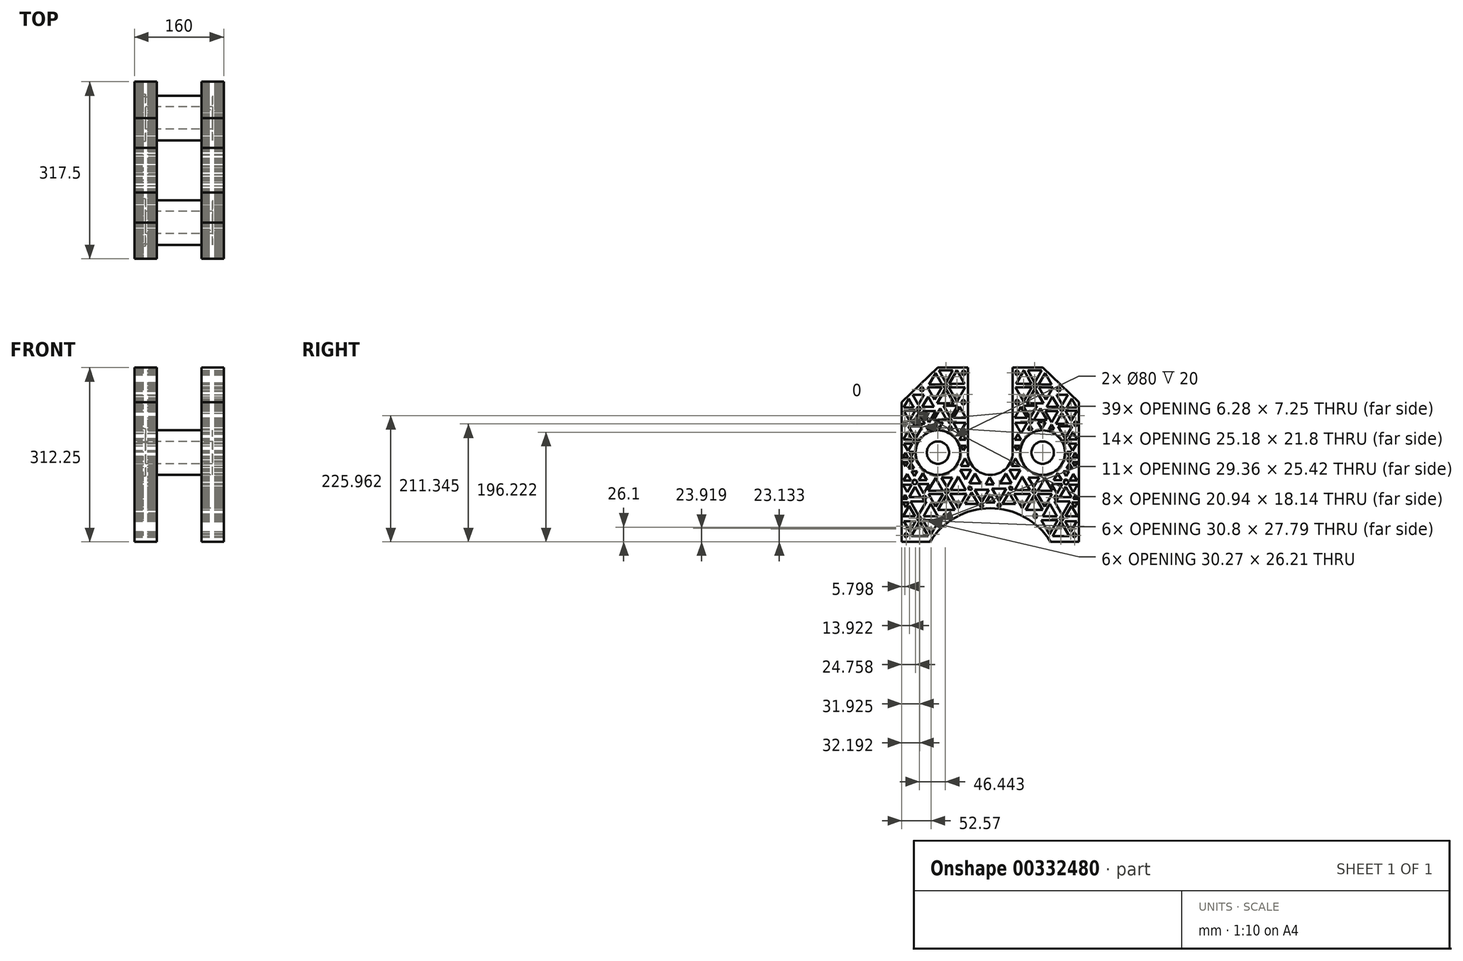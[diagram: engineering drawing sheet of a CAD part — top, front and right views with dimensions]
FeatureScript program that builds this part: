
annotation { "Feature Type Name" : "Feature", "Feature Type Description" : "" }
export const myFeature = defineFeature(function(context is Context, id is Id, definition is map)
    precondition{}
    {
        {
            var Q0;
            Q0=qCreatedBy(makeId("Right.planeOp"),FACE);
            var sketch = newSketch(context, id + "F0", { "sketchPlane" : qUnion([Q0])});
            skLineSegment(sketch, "E0", {"start": v(-158.75, 0) * mm, "end": v(-158.75, 250) * mm});
            skLineSegment(sketch, "E1", {"start": v(-158.75, 250) * mm, "end": v(-93.75, 312.25) * mm});
            skLineSegment(sketch, "E2.MirrorCS", {"start": v(158.75, 250) * mm, "end": v(93.75, 312.25) * mm});
            skLineSegment(sketch, "E3.MirrorCS", {"start": v(158.75, 0) * mm, "end": v(158.75, 250) * mm});
            skLineSegment(sketch, "E4", {"start": v(-158.75, 0) * mm, "end": v(-107.95, 0) * mm});
            skArc(sketch, "E5", {"start": v(107.95, 0) * mm, "mid": v(0, 60.1) * mm, "end": v(-107.95, 0) * mm});
            skLineSegment(sketch, "E6", {"start": v(107.95, 0) * mm, "end": v(158.75, 0) * mm});
            skLineSegment(sketch, "E7", {"start": v(-93.75, 312.25) * mm, "end": v(-40, 312.25) * mm});
            skLineSegment(sketch, "E8", {"start": v(-40, 312.25) * mm, "end": v(-40, 159.85) * mm});
            skArc(sketch, "E9", {"start": v(-40, 159.85) * mm, "mid": v(0, 119.85) * mm, "end": v(40, 159.85) * mm});
            skLineSegment(sketch, "E10", {"start": v(40, 159.85) * mm, "end": v(40, 312.25) * mm});
            skLineSegment(sketch, "E11", {"start": v(40, 312.25) * mm, "end": v(93.75, 312.25) * mm});
            skCircle(sketch, "E12", {"center": v(93.75, 159.85) * mm, "radius": 40 * mm});
            skCircle(sketch, "E13", {"center": v(-93.75, 159.85) * mm, "radius": 40 * mm});
            skSolve(sketch);
        }
        {
            var Q0;
            Q0=makeQuery(id+"F0.imprint","IMPRINT",FACE,{"disambiguationData":[TD([[makeQuery(id+"F0.imprint","IMPRINT",EDGE,{"derivedFrom":sQuery(id+"F0.wireOp",EDGE,"E0")}),-1.0]])]});
            extrude(context, id + "F1", {"entities" : qUnion([Q0]), "endBound" : BoundingType.SYMMETRIC, "depth" : 160 * mm});
        }
        {
            var Q0;
            Q0=makeQuery(id+"F1.opExtrude","SWEPT_FACE",FACE,{"disambiguationData":[OSD([sQuery(id+"F0.wireOp",EDGE,"E3.MirrorCS")])]});
            var sketch = newSketch(context, id + "F2", { "sketchPlane" : qUnion([Q0])});
            skLineSegment(sketch, "E14.bottom", {"start": v(-40, 0) * mm, "end": v(40, 0) * mm});
            skLineSegment(sketch, "E14.top", {"start": v(-40, 330.24) * mm, "end": v(40, 330.24) * mm});
            skLineSegment(sketch, "E14.left", {"start": v(-40, 0) * mm, "end": v(-40, 330.24) * mm});
            skLineSegment(sketch, "E14.right", {"start": v(40, 0) * mm, "end": v(40, 330.24) * mm});
            skSolve(sketch);
        }
        {
            var Q0;
            {var subQ0=sQuery(id+"F2.wireOp",EDGE,"E14.bottom");Q0=makeQuery(id+"F2.imprint","IMPRINT",FACE,{"disambiguationData":[TD([[makeQuery(id+"F2.imprint","IMPRINT",EDGE,{"derivedFrom":subQ0}),1.0]])]});}
            var Q1;
            {var subQ0=sQuery(id+"F2.wireOp",EDGE,"E14.top");Q1=makeQuery(id+"F2.imprint","IMPRINT",FACE,{"disambiguationData":[TD([[makeQuery(id+"F2.imprint","IMPRINT",EDGE,{"derivedFrom":subQ0}),-1.0]])]});}
            extrude(context, id + "F3", {"entities" : qUnion([Q0, Q1]), "operationType" : NewBodyOperationType.REMOVE, "oppositeDirection" : true, "depth" : 414.02 * mm});
        }
        {
            var Q0;
            Q0=makeQuery(id+"F1.opExtrude","CAP_FACE",FACE,{"disambiguationData":[OSD([sQuery(id+"F0.wireOp",EDGE,"E0"),sQuery(id+"F0.wireOp",EDGE,"E1"),sQuery(id+"F0.wireOp",EDGE,"E2.MirrorCS"),sQuery(id+"F0.wireOp",EDGE,"E3.MirrorCS"),sQuery(id+"F0.wireOp",EDGE,"E4"),sQuery(id+"F0.wireOp",EDGE,"E5"),sQuery(id+"F0.wireOp",EDGE,"E6"),sQuery(id+"F0.wireOp",EDGE,"E7"),sQuery(id+"F0.wireOp",EDGE,"E8"),sQuery(id+"F0.wireOp",EDGE,"E9"),sQuery(id+"F0.wireOp",EDGE,"E10"),sQuery(id+"F0.wireOp",EDGE,"E11"),sQuery(id+"F0.wireOp",EDGE,"E12"),sQuery(id+"F0.wireOp",EDGE,"E13")])],"isStart":true});
            var sketch = newSketch(context, id + "F4", { "sketchPlane" : qUnion([Q0])});
            skCircle(sketch, "E15", {"center": v(-93.75, 159.85) * mm, "radius": 42.5 * mm});
            skCircle(sketch, "E16", {"center": v(-93.75, 159.85) * mm, "radius": 20 * mm});
            skCircle(sketch, "E17", {"center": v(93.75, 159.85) * mm, "radius": 42.5 * mm});
            skCircle(sketch, "E18", {"center": v(93.75, 159.85) * mm, "radius": 20 * mm});
            skSolve(sketch);
        }
        {
            var Q0;
            Q0=makeQuery(id+"F4.imprint","IMPRINT",FACE,{"disambiguationData":[TD([[makeQuery(id+"F4.imprint","IMPRINT",EDGE,{"derivedFrom":sQuery(id+"F4.wireOp",EDGE,"E16")}),-1.0]])]});
            var Q1;
            Q1=makeQuery(id+"F4.imprint","IMPRINT",FACE,{"disambiguationData":[TD([[makeQuery(id+"F4.imprint","IMPRINT",EDGE,{"derivedFrom":sQuery(id+"F4.wireOp",EDGE,"E18")}),-1.0]])]});
            extrude(context, id + "F5", {"entities" : qUnion([Q0, Q1]), "operationType" : NewBodyOperationType.ADD, "oppositeDirection" : true, "depth" : 140 * mm});
        }
        {
            var Q0;
            {var subQ0=sQuery(id+"F0.wireOp",EDGE,"E13");var subQ1=sQuery(id+"F0.wireOp",EDGE,"E12");Q0=makeQuery(id+"F5.boolean.opBoolean","MERGE",FACE,{"derivedFrom":[makeQuery(id+"F1.opExtrude","CAP_FACE",FACE,{"disambiguationData":[OSD([sQuery(id+"F0.wireOp",EDGE,"E0"),sQuery(id+"F0.wireOp",EDGE,"E1"),sQuery(id+"F0.wireOp",EDGE,"E2.MirrorCS"),sQuery(id+"F0.wireOp",EDGE,"E3.MirrorCS"),sQuery(id+"F0.wireOp",EDGE,"E4"),sQuery(id+"F0.wireOp",EDGE,"E5"),sQuery(id+"F0.wireOp",EDGE,"E6"),sQuery(id+"F0.wireOp",EDGE,"E7"),sQuery(id+"F0.wireOp",EDGE,"E8"),sQuery(id+"F0.wireOp",EDGE,"E9"),sQuery(id+"F0.wireOp",EDGE,"E10"),sQuery(id+"F0.wireOp",EDGE,"E11"),subQ1,subQ0])],"isStart":true}),makeQuery(id+"F5.opExtrude","CAP_FACE",FACE,{"disambiguationData":[OSD([subQ1,sQuery(id+"F4.wireOp",EDGE,"E16")])],"isStart":true}),makeQuery(id+"F5.opExtrude","CAP_FACE",FACE,{"disambiguationData":[OSD([subQ0,sQuery(id+"F4.wireOp",EDGE,"E18")])],"isStart":true})]});}
            var sketch = newSketch(context, id + "F6", { "sketchPlane" : qUnion([Q0])});
            skCircle(sketch, "E19", {"center": v(-93.75, 159.85) * mm, "radius": 42.5 * mm});
            skCircle(sketch, "E20", {"center": v(93.75, 159.85) * mm, "radius": 42.5 * mm});
            skSolve(sketch);
        }
        {
            var Q0;
            Q0=makeQuery(id+"F6.imprint","IMPRINT",FACE,{"disambiguationData":[TD([[makeQuery(id+"F6.imprint","IMPRINT",EDGE,{"derivedFrom":sQuery(id+"F6.wireOp",EDGE,"E19")}),1.0]])]});
            var Q1;
            Q1=makeQuery(id+"F6.imprint","IMPRINT",FACE,{"disambiguationData":[TD([[makeQuery(id+"F6.imprint","IMPRINT",EDGE,{"derivedFrom":sQuery(id+"F6.wireOp",EDGE,"E20")}),1.0]])]});
            extrude(context, id + "F7", {"entities" : qUnion([Q0, Q1]), "operationType" : NewBodyOperationType.REMOVE, "oppositeDirection" : true, "depth" : 20 * mm});
        }
        {
            var Q0;
            Q0=makeQuery(id+"F1.opExtrude","CAP_FACE",FACE,{"disambiguationData":[OSD([sQuery(id+"F0.wireOp",EDGE,"E0"),sQuery(id+"F0.wireOp",EDGE,"E1"),sQuery(id+"F0.wireOp",EDGE,"E2.MirrorCS"),sQuery(id+"F0.wireOp",EDGE,"E3.MirrorCS"),sQuery(id+"F0.wireOp",EDGE,"E4"),sQuery(id+"F0.wireOp",EDGE,"E5"),sQuery(id+"F0.wireOp",EDGE,"E6"),sQuery(id+"F0.wireOp",EDGE,"E7"),sQuery(id+"F0.wireOp",EDGE,"E8"),sQuery(id+"F0.wireOp",EDGE,"E9"),sQuery(id+"F0.wireOp",EDGE,"E10"),sQuery(id+"F0.wireOp",EDGE,"E11"),sQuery(id+"F0.wireOp",EDGE,"E12"),sQuery(id+"F0.wireOp",EDGE,"E13")])],"isStart":false});
            var sketch = newSketch(context, id + "F8", { "sketchPlane" : qUnion([Q0])});
            skCircle(sketch, "E21.cCircle", {"center": v(-106.18, 30.34) * mm, "radius": 8.47 * mm, "construction": true});
            skLineSegment(sketch, "E21.0", {"start": v(-91.5, 38.81) * mm, "end": v(-106.18, 13.39) * mm});
            skLineSegment(sketch, "E21.1", {"start": v(-106.18, 13.39) * mm, "end": v(-120.86, 38.81) * mm});
            skLineSegment(sketch, "E21.2", {"start": v(-120.86, 38.81) * mm, "end": v(-91.5, 38.81) * mm});
            skPoint(sketch, "E21.0.midPoint", {"position": v(-98.84, 26.1) * mm});
            skCircle(sketch, "E22.cCircle", {"center": v(-126.56, 18.76) * mm, "radius": 8.74 * mm, "construction": true});
            skLineSegment(sketch, "E22.0", {"start": v(-126.56, 36.24) * mm, "end": v(-111.42, 10.03) * mm});
            skLineSegment(sketch, "E22.1", {"start": v(-111.42, 10.03) * mm, "end": v(-141.7, 10.03) * mm});
            skLineSegment(sketch, "E22.2", {"start": v(-141.7, 10.03) * mm, "end": v(-126.56, 36.24) * mm});
            skPoint(sketch, "E22.0.midPoint", {"position": v(-119, 23.13) * mm});
            skCircle(sketch, "E23.cCircle", {"center": v(-144.4, 30.7) * mm, "radius": 6.05 * mm, "construction": true});
            skLineSegment(sketch, "E23.0", {"start": v(-133.92, 36.75) * mm, "end": v(-144.4, 18.62) * mm});
            skLineSegment(sketch, "E23.1", {"start": v(-144.4, 18.62) * mm, "end": v(-154.86, 36.75) * mm});
            skLineSegment(sketch, "E23.2", {"start": v(-154.86, 36.75) * mm, "end": v(-133.92, 36.75) * mm});
            skPoint(sketch, "E23.0.midPoint", {"position": v(-139.16, 27.69) * mm});
            skCircle(sketch, "E24.cCircle", {"center": v(-128.66, 64.11) * mm, "radius": 8.12 * mm, "construction": true});
            skLineSegment(sketch, "E24.0", {"start": v(-114.59, 72.24) * mm, "end": v(-128.66, 47.87) * mm});
            skLineSegment(sketch, "E24.1", {"start": v(-128.66, 47.87) * mm, "end": v(-142.73, 72.24) * mm});
            skLineSegment(sketch, "E24.2", {"start": v(-142.73, 72.24) * mm, "end": v(-114.59, 72.24) * mm});
            skPoint(sketch, "E24.0.midPoint", {"position": v(-121.62, 60.05) * mm});
            skCircle(sketch, "E25.cCircle", {"center": v(-145.4, 51.88) * mm, "radius": 6.25 * mm, "construction": true});
            skLineSegment(sketch, "E25.0", {"start": v(-145.4, 64.4) * mm, "end": v(-134.57, 45.63) * mm});
            skLineSegment(sketch, "E25.1", {"start": v(-134.57, 45.63) * mm, "end": v(-156.23, 45.63) * mm});
            skLineSegment(sketch, "E25.2", {"start": v(-156.23, 45.63) * mm, "end": v(-145.4, 64.4) * mm});
            skPoint(sketch, "E25.0.midPoint", {"position": v(-139.98, 55.01) * mm});
            skCircle(sketch, "E26.cCircle", {"center": v(-106.43, 53.23) * mm, "radius": 7.34 * mm, "construction": true});
            skLineSegment(sketch, "E26.0", {"start": v(-106.43, 67.9) * mm, "end": v(-93.72, 45.9) * mm});
            skLineSegment(sketch, "E26.1", {"start": v(-93.72, 45.9) * mm, "end": v(-119.14, 45.9) * mm});
            skLineSegment(sketch, "E26.2", {"start": v(-119.14, 45.9) * mm, "end": v(-106.43, 67.9) * mm});
            skPoint(sketch, "E26.0.midPoint", {"position": v(-100.08, 56.9) * mm});
            skCircle(sketch, "E27.cCircle", {"center": v(-57.15, 77.52) * mm, "radius": 8.47 * mm, "construction": true});
            skLineSegment(sketch, "E27.0", {"start": v(-42.47, 86) * mm, "end": v(-57.15, 60.57) * mm});
            skLineSegment(sketch, "E27.1", {"start": v(-57.15, 60.57) * mm, "end": v(-71.82, 86) * mm});
            skLineSegment(sketch, "E27.2", {"start": v(-71.82, 86) * mm, "end": v(-42.47, 86) * mm});
            skPoint(sketch, "E27.0.midPoint", {"position": v(-49.8, 73.28) * mm});
            skCircle(sketch, "E28.cCircle", {"center": v(-78.58, 65.64) * mm, "radius": 8.74 * mm, "construction": true});
            skLineSegment(sketch, "E28.0", {"start": v(-78.58, 83.12) * mm, "end": v(-63.45, 56.9) * mm});
            skLineSegment(sketch, "E28.1", {"start": v(-63.45, 56.9) * mm, "end": v(-93.72, 56.9) * mm});
            skLineSegment(sketch, "E28.2", {"start": v(-93.72, 56.9) * mm, "end": v(-78.58, 83.12) * mm});
            skPoint(sketch, "E28.0.midPoint", {"position": v(-71.02, 70) * mm});
            skCircle(sketch, "E29.cCircle", {"center": v(-97.56, 77.84) * mm, "radius": 7.63 * mm, "construction": true});
            skLineSegment(sketch, "E29.0", {"start": v(-84.34, 85.47) * mm, "end": v(-97.56, 62.57) * mm});
            skLineSegment(sketch, "E29.1", {"start": v(-97.56, 62.57) * mm, "end": v(-110.78, 85.47) * mm});
            skLineSegment(sketch, "E29.2", {"start": v(-110.78, 85.47) * mm, "end": v(-84.34, 85.47) * mm});
            skPoint(sketch, "E29.0.midPoint", {"position": v(-90.95, 74.02) * mm});
            skCircle(sketch, "E30.cCircle", {"center": v(-77.79, 109.6) * mm, "radius": 5.61 * mm, "construction": true});
            skLineSegment(sketch, "E30.0", {"start": v(-68.07, 115.21) * mm, "end": v(-77.79, 98.37) * mm});
            skLineSegment(sketch, "E30.1", {"start": v(-77.79, 98.37) * mm, "end": v(-87.51, 115.21) * mm});
            skLineSegment(sketch, "E30.2", {"start": v(-87.51, 115.21) * mm, "end": v(-68.07, 115.21) * mm});
            skPoint(sketch, "E30.0.midPoint", {"position": v(-72.93, 106.8) * mm});
            skCircle(sketch, "E31.cCircle", {"center": v(-97.92, 99.18) * mm, "radius": 7.55 * mm, "construction": true});
            skLineSegment(sketch, "E31.0", {"start": v(-97.92, 114.3) * mm, "end": v(-84.83, 91.63) * mm});
            skLineSegment(sketch, "E31.1", {"start": v(-84.83, 91.63) * mm, "end": v(-111, 91.63) * mm});
            skLineSegment(sketch, "E31.2", {"start": v(-111, 91.63) * mm, "end": v(-97.92, 114.3) * mm});
            skPoint(sketch, "E31.0.midPoint", {"position": v(-91.37, 102.96) * mm});
            skCircle(sketch, "E32.cCircle", {"center": v(-57.4, 100.41) * mm, "radius": 7.95 * mm, "construction": true});
            skLineSegment(sketch, "E32.0", {"start": v(-57.4, 116.32) * mm, "end": v(-43.62, 92.46) * mm});
            skLineSegment(sketch, "E32.1", {"start": v(-43.62, 92.46) * mm, "end": v(-71.17, 92.46) * mm});
            skLineSegment(sketch, "E32.2", {"start": v(-71.17, 92.46) * mm, "end": v(-57.4, 116.32) * mm});
            skPoint(sketch, "E32.0.midPoint", {"position": v(-50.51, 104.39) * mm});
            skCircle(sketch, "E33.cCircle", {"center": v(-119.35, 97.8) * mm, "radius": 5.63 * mm, "construction": true});
            skLineSegment(sketch, "E33.0", {"start": v(-109.59, 103.44) * mm, "end": v(-119.35, 86.53) * mm});
            skLineSegment(sketch, "E33.1", {"start": v(-119.35, 86.53) * mm, "end": v(-129.1, 103.44) * mm});
            skLineSegment(sketch, "E33.2", {"start": v(-129.1, 103.44) * mm, "end": v(-109.59, 103.44) * mm});
            skPoint(sketch, "E33.0.midPoint", {"position": v(-114.47, 94.98) * mm});
            skCircle(sketch, "E34.cCircle", {"center": v(-134.95, 86.23) * mm, "radius": 5.94 * mm, "construction": true});
            skLineSegment(sketch, "E34.0", {"start": v(-134.95, 98.11) * mm, "end": v(-124.66, 80.29) * mm});
            skLineSegment(sketch, "E34.1", {"start": v(-124.66, 80.29) * mm, "end": v(-145.24, 80.29) * mm});
            skLineSegment(sketch, "E34.2", {"start": v(-145.24, 80.29) * mm, "end": v(-134.95, 98.11) * mm});
            skPoint(sketch, "E34.0.midPoint", {"position": v(-129.8, 89.2) * mm});
            skCircle(sketch, "E35.cCircle", {"center": v(-148.63, 97.6) * mm, "radius": 4.36 * mm, "construction": true});
            skLineSegment(sketch, "E35.0", {"start": v(-141.07, 101.95) * mm, "end": v(-148.63, 88.87) * mm});
            skLineSegment(sketch, "E35.1", {"start": v(-148.63, 88.87) * mm, "end": v(-156.18, 101.95) * mm});
            skLineSegment(sketch, "E35.2", {"start": v(-156.18, 101.95) * mm, "end": v(-141.07, 101.95) * mm});
            skPoint(sketch, "E35.0.midPoint", {"position": v(-144.85, 95.41) * mm});
            skCircle(sketch, "E36.cCircle", {"center": v(-135.92, 123.34) * mm, "radius": 3.06 * mm, "construction": true});
            skLineSegment(sketch, "E36.0", {"start": v(-130.63, 126.4) * mm, "end": v(-135.92, 117.23) * mm});
            skLineSegment(sketch, "E36.1", {"start": v(-135.92, 117.23) * mm, "end": v(-141.22, 126.4) * mm});
            skLineSegment(sketch, "E36.2", {"start": v(-141.22, 126.4) * mm, "end": v(-130.63, 126.4) * mm});
            skPoint(sketch, "E36.0.midPoint", {"position": v(-133.28, 121.82) * mm});
            skCircle(sketch, "E37.cCircle", {"center": v(-148.8, 113.42) * mm, "radius": 3.86 * mm, "construction": true});
            skLineSegment(sketch, "E37.0", {"start": v(-148.8, 121.14) * mm, "end": v(-142.12, 109.55) * mm});
            skLineSegment(sketch, "E37.1", {"start": v(-142.12, 109.55) * mm, "end": v(-155.5, 109.55) * mm});
            skLineSegment(sketch, "E37.2", {"start": v(-155.5, 109.55) * mm, "end": v(-148.8, 121.14) * mm});
            skPoint(sketch, "E37.0.midPoint", {"position": v(-145.46, 115.35) * mm});
            skCircle(sketch, "E38.cCircle", {"center": v(-120.77, 114.42) * mm, "radius": 4.19 * mm, "construction": true});
            skLineSegment(sketch, "E38.0", {"start": v(-120.77, 122.8) * mm, "end": v(-113.52, 110.24) * mm});
            skLineSegment(sketch, "E38.1", {"start": v(-113.52, 110.24) * mm, "end": v(-128.03, 110.24) * mm});
            skLineSegment(sketch, "E38.2", {"start": v(-128.03, 110.24) * mm, "end": v(-120.77, 122.8) * mm});
            skPoint(sketch, "E38.0.midPoint", {"position": v(-117.15, 116.52) * mm});
            skCircle(sketch, "E39.cCircle", {"center": v(-59.74, 268.47) * mm, "radius": 8.47 * mm, "construction": true});
            skLineSegment(sketch, "E39.0", {"start": v(-45.06, 276.94) * mm, "end": v(-59.74, 251.52) * mm});
            skLineSegment(sketch, "E39.1", {"start": v(-59.74, 251.52) * mm, "end": v(-74.42, 276.94) * mm});
            skLineSegment(sketch, "E39.2", {"start": v(-74.42, 276.94) * mm, "end": v(-45.06, 276.94) * mm});
            skPoint(sketch, "E39.0.midPoint", {"position": v(-52.4, 264.23) * mm});
            skCircle(sketch, "E40.cCircle", {"center": v(-80.12, 256.9) * mm, "radius": 8.74 * mm, "construction": true});
            skLineSegment(sketch, "E40.0", {"start": v(-80.12, 274.37) * mm, "end": v(-64.98, 248.16) * mm});
            skLineSegment(sketch, "E40.1", {"start": v(-64.98, 248.16) * mm, "end": v(-95.25, 248.16) * mm});
            skLineSegment(sketch, "E40.2", {"start": v(-95.25, 248.16) * mm, "end": v(-80.12, 274.37) * mm});
            skPoint(sketch, "E40.0.midPoint", {"position": v(-72.55, 261.26) * mm});
            skCircle(sketch, "E41.cCircle", {"center": v(-99.62, 269.66) * mm, "radius": 7.46 * mm, "construction": true});
            skLineSegment(sketch, "E41.0", {"start": v(-86.7, 277.12) * mm, "end": v(-99.62, 254.73) * mm});
            skLineSegment(sketch, "E41.1", {"start": v(-99.62, 254.73) * mm, "end": v(-112.54, 277.12) * mm});
            skLineSegment(sketch, "E41.2", {"start": v(-112.54, 277.12) * mm, "end": v(-86.7, 277.12) * mm});
            skPoint(sketch, "E41.0.midPoint", {"position": v(-93.15, 265.93) * mm});
            skCircle(sketch, "E42.cCircle", {"center": v(-79.64, 299.81) * mm, "radius": 7.27 * mm, "construction": true});
            skLineSegment(sketch, "E42.0", {"start": v(-67.05, 307.08) * mm, "end": v(-79.64, 285.28) * mm});
            skLineSegment(sketch, "E42.1", {"start": v(-79.64, 285.28) * mm, "end": v(-92.22, 307.08) * mm});
            skLineSegment(sketch, "E42.2", {"start": v(-92.22, 307.08) * mm, "end": v(-67.05, 307.08) * mm});
            skPoint(sketch, "E42.0.midPoint", {"position": v(-73.34, 296.18) * mm});
            skCircle(sketch, "E43.cCircle", {"center": v(-98.1, 288.5) * mm, "radius": 6.73 * mm, "construction": true});
            skLineSegment(sketch, "E43.0", {"start": v(-98.1, 301.97) * mm, "end": v(-86.44, 281.77) * mm});
            skLineSegment(sketch, "E43.1", {"start": v(-86.44, 281.77) * mm, "end": v(-109.77, 281.77) * mm});
            skLineSegment(sketch, "E43.2", {"start": v(-109.77, 281.77) * mm, "end": v(-98.1, 301.97) * mm});
            skPoint(sketch, "E43.0.midPoint", {"position": v(-92.27, 291.87) * mm});
            skCircle(sketch, "E44.cCircle", {"center": v(-59.99, 291.36) * mm, "radius": 7.95 * mm, "construction": true});
            skLineSegment(sketch, "E44.0", {"start": v(-59.99, 307.26) * mm, "end": v(-46.22, 283.41) * mm});
            skLineSegment(sketch, "E44.1", {"start": v(-46.22, 283.41) * mm, "end": v(-73.76, 283.41) * mm});
            skLineSegment(sketch, "E44.2", {"start": v(-73.76, 283.41) * mm, "end": v(-59.99, 307.26) * mm});
            skPoint(sketch, "E44.0.midPoint", {"position": v(-53.1, 295.34) * mm});
            skCircle(sketch, "E45.cCircle", {"center": v(-109.8, 227.44) * mm, "radius": 6.72 * mm, "construction": true});
            skLineSegment(sketch, "E45.0", {"start": v(-98.15, 234.16) * mm, "end": v(-109.8, 213.99) * mm});
            skLineSegment(sketch, "E45.1", {"start": v(-109.8, 213.99) * mm, "end": v(-121.44, 234.16) * mm});
            skLineSegment(sketch, "E45.2", {"start": v(-121.44, 234.16) * mm, "end": v(-98.15, 234.16) * mm});
            skPoint(sketch, "E45.0.midPoint", {"position": v(-103.97, 224.08) * mm});
            skCircle(sketch, "E46.cCircle", {"center": v(-128.26, 218.01) * mm, "radius": 6.33 * mm, "construction": true});
            skLineSegment(sketch, "E46.0", {"start": v(-128.26, 230.68) * mm, "end": v(-117.3, 211.68) * mm});
            skLineSegment(sketch, "E46.1", {"start": v(-117.3, 211.68) * mm, "end": v(-139.24, 211.68) * mm});
            skLineSegment(sketch, "E46.2", {"start": v(-139.24, 211.68) * mm, "end": v(-128.26, 230.68) * mm});
            skPoint(sketch, "E46.0.midPoint", {"position": v(-122.78, 221.18) * mm});
            skCircle(sketch, "E47.cCircle", {"center": v(-144.83, 228.98) * mm, "radius": 6.05 * mm, "construction": true});
            skLineSegment(sketch, "E47.0", {"start": v(-134.36, 235.03) * mm, "end": v(-144.83, 216.9) * mm});
            skLineSegment(sketch, "E47.1", {"start": v(-144.83, 216.9) * mm, "end": v(-155.3, 235.03) * mm});
            skLineSegment(sketch, "E47.2", {"start": v(-155.3, 235.03) * mm, "end": v(-134.36, 235.03) * mm});
            skPoint(sketch, "E47.0.midPoint", {"position": v(-139.6, 225.96) * mm});
            skCircle(sketch, "E48.cCircle", {"center": v(-128.98, 257.41) * mm, "radius": 5.98 * mm, "construction": true});
            skLineSegment(sketch, "E48.0", {"start": v(-118.63, 263.4) * mm, "end": v(-128.98, 245.46) * mm});
            skLineSegment(sketch, "E48.1", {"start": v(-128.98, 245.46) * mm, "end": v(-139.33, 263.4) * mm});
            skLineSegment(sketch, "E48.2", {"start": v(-139.33, 263.4) * mm, "end": v(-118.63, 263.4) * mm});
            skPoint(sketch, "E48.0.midPoint", {"position": v(-123.8, 254.43) * mm});
            skCircle(sketch, "E49.cCircle", {"center": v(-146.09, 246.1) * mm, "radius": 5.22 * mm, "construction": true});
            skLineSegment(sketch, "E49.0", {"start": v(-146.09, 256.53) * mm, "end": v(-137.05, 240.88) * mm});
            skLineSegment(sketch, "E49.1", {"start": v(-137.05, 240.88) * mm, "end": v(-155.12, 240.88) * mm});
            skLineSegment(sketch, "E49.2", {"start": v(-155.12, 240.88) * mm, "end": v(-146.09, 256.53) * mm});
            skPoint(sketch, "E49.0.midPoint", {"position": v(-141.57, 248.7) * mm});
            skCircle(sketch, "E50.cCircle", {"center": v(-111.3, 247.8) * mm, "radius": 6.04 * mm, "construction": true});
            skLineSegment(sketch, "E50.0", {"start": v(-111.3, 259.88) * mm, "end": v(-100.83, 241.75) * mm});
            skLineSegment(sketch, "E50.1", {"start": v(-100.83, 241.75) * mm, "end": v(-121.77, 241.75) * mm});
            skLineSegment(sketch, "E50.2", {"start": v(-121.77, 241.75) * mm, "end": v(-111.3, 259.88) * mm});
            skPoint(sketch, "E50.0.midPoint", {"position": v(-106.07, 250.81) * mm});
            skCircle(sketch, "E51.cCircle", {"center": v(-127.93, 41.93) * mm, "radius": 3.14 * mm, "construction": true});
            skLineSegment(sketch, "E51.0", {"start": v(-124.8, 43.74) * mm, "end": v(-124.8, 40.12) * mm});
            skLineSegment(sketch, "E51.1", {"start": v(-124.8, 40.12) * mm, "end": v(-127.93, 38.3) * mm});
            skLineSegment(sketch, "E51.2", {"start": v(-127.93, 38.3) * mm, "end": v(-131.07, 40.12) * mm});
            skLineSegment(sketch, "E51.3", {"start": v(-131.07, 40.12) * mm, "end": v(-131.07, 43.74) * mm});
            skLineSegment(sketch, "E51.4", {"start": v(-131.07, 43.74) * mm, "end": v(-127.93, 45.55) * mm});
            skLineSegment(sketch, "E51.5", {"start": v(-127.93, 45.55) * mm, "end": v(-124.8, 43.74) * mm});
            skPoint(sketch, "E51.0.midPoint", {"position": v(-124.8, 41.93) * mm});
            skCircle(sketch, "E52.cCircle", {"center": v(-78.38, 90.8) * mm, "radius": 3.14 * mm, "construction": true});
            skLineSegment(sketch, "E52.0", {"start": v(-75.24, 92.6) * mm, "end": v(-75.24, 88.98) * mm});
            skLineSegment(sketch, "E52.1", {"start": v(-75.24, 88.98) * mm, "end": v(-78.38, 87.17) * mm});
            skLineSegment(sketch, "E52.2", {"start": v(-78.38, 87.17) * mm, "end": v(-81.51, 88.98) * mm});
            skLineSegment(sketch, "E52.3", {"start": v(-81.51, 88.98) * mm, "end": v(-81.51, 92.6) * mm});
            skLineSegment(sketch, "E52.4", {"start": v(-81.51, 92.6) * mm, "end": v(-78.38, 94.42) * mm});
            skLineSegment(sketch, "E52.5", {"start": v(-78.38, 94.42) * mm, "end": v(-75.24, 92.6) * mm});
            skPoint(sketch, "E52.0.midPoint", {"position": v(-75.24, 90.8) * mm});
            skCircle(sketch, "E53.cCircle", {"center": v(-135.55, 106.78) * mm, "radius": 3.82 * mm, "construction": true});
            skLineSegment(sketch, "E53.0", {"start": v(-131.73, 108.99) * mm, "end": v(-131.73, 104.57) * mm});
            skLineSegment(sketch, "E53.1", {"start": v(-131.73, 104.57) * mm, "end": v(-135.55, 102.37) * mm});
            skLineSegment(sketch, "E53.2", {"start": v(-135.55, 102.37) * mm, "end": v(-139.37, 104.57) * mm});
            skLineSegment(sketch, "E53.3", {"start": v(-139.37, 104.57) * mm, "end": v(-139.37, 108.99) * mm});
            skLineSegment(sketch, "E53.4", {"start": v(-139.37, 108.99) * mm, "end": v(-135.55, 111.2) * mm});
            skLineSegment(sketch, "E53.5", {"start": v(-135.55, 111.2) * mm, "end": v(-131.73, 108.99) * mm});
            skPoint(sketch, "E53.0.midPoint", {"position": v(-131.73, 106.78) * mm});
            skCircle(sketch, "E54.cCircle", {"center": v(-128.26, 238.37) * mm, "radius": 3.14 * mm, "construction": true});
            skLineSegment(sketch, "E54.0", {"start": v(-125.12, 240.18) * mm, "end": v(-125.12, 236.56) * mm});
            skLineSegment(sketch, "E54.1", {"start": v(-125.12, 236.56) * mm, "end": v(-128.26, 234.75) * mm});
            skLineSegment(sketch, "E54.2", {"start": v(-128.26, 234.75) * mm, "end": v(-131.4, 236.56) * mm});
            skLineSegment(sketch, "E54.3", {"start": v(-131.4, 236.56) * mm, "end": v(-131.4, 240.18) * mm});
            skLineSegment(sketch, "E54.4", {"start": v(-131.4, 240.18) * mm, "end": v(-128.26, 242) * mm});
            skLineSegment(sketch, "E54.5", {"start": v(-128.26, 242) * mm, "end": v(-125.12, 240.18) * mm});
            skPoint(sketch, "E54.0.midPoint", {"position": v(-125.12, 238.37) * mm});
            skCircle(sketch, "E55.cCircle", {"center": v(-80.47, 279.85) * mm, "radius": 3.14 * mm, "construction": true});
            skLineSegment(sketch, "E55.0", {"start": v(-77.33, 281.66) * mm, "end": v(-77.33, 278.04) * mm});
            skLineSegment(sketch, "E55.1", {"start": v(-77.33, 278.04) * mm, "end": v(-80.47, 276.23) * mm});
            skLineSegment(sketch, "E55.2", {"start": v(-80.47, 276.23) * mm, "end": v(-83.6, 278.04) * mm});
            skLineSegment(sketch, "E55.3", {"start": v(-83.6, 278.04) * mm, "end": v(-83.6, 281.66) * mm});
            skLineSegment(sketch, "E55.4", {"start": v(-83.6, 281.66) * mm, "end": v(-80.47, 283.47) * mm});
            skLineSegment(sketch, "E55.5", {"start": v(-80.47, 283.47) * mm, "end": v(-77.33, 281.66) * mm});
            skPoint(sketch, "E55.0.midPoint", {"position": v(-77.33, 279.85) * mm});
            skCircle(sketch, "E56.cCircle", {"center": v(-55.1, 206.8) * mm, "radius": 6.34 * mm, "construction": true});
            skLineSegment(sketch, "E56.0", {"start": v(-44.12, 213.14) * mm, "end": v(-55.1, 194.13) * mm});
            skLineSegment(sketch, "E56.1", {"start": v(-55.1, 194.13) * mm, "end": v(-66.06, 213.14) * mm});
            skLineSegment(sketch, "E56.2", {"start": v(-66.06, 213.14) * mm, "end": v(-44.12, 213.14) * mm});
            skPoint(sketch, "E56.0.midPoint", {"position": v(-49.6, 203.63) * mm});
            skCircle(sketch, "E57.cCircle", {"center": v(-71.28, 236.47) * mm, "radius": 7.27 * mm, "construction": true});
            skLineSegment(sketch, "E57.0", {"start": v(-58.69, 243.74) * mm, "end": v(-71.28, 221.93) * mm});
            skLineSegment(sketch, "E57.1", {"start": v(-71.28, 221.93) * mm, "end": v(-83.87, 243.74) * mm});
            skLineSegment(sketch, "E57.2", {"start": v(-83.87, 243.74) * mm, "end": v(-58.69, 243.74) * mm});
            skPoint(sketch, "E57.0.midPoint", {"position": v(-64.98, 232.83) * mm});
            skCircle(sketch, "E58.cCircle", {"center": v(-89.75, 225.16) * mm, "radius": 6.73 * mm, "construction": true});
            skLineSegment(sketch, "E58.0", {"start": v(-89.75, 238.63) * mm, "end": v(-78.08, 218.42) * mm});
            skLineSegment(sketch, "E58.1", {"start": v(-78.08, 218.42) * mm, "end": v(-101.41, 218.42) * mm});
            skLineSegment(sketch, "E58.2", {"start": v(-101.41, 218.42) * mm, "end": v(-89.75, 238.63) * mm});
            skPoint(sketch, "E58.0.midPoint", {"position": v(-83.92, 228.53) * mm});
            skCircle(sketch, "E59.cCircle", {"center": v(-54.84, 228.94) * mm, "radius": 6.48 * mm, "construction": true});
            skLineSegment(sketch, "E59.0", {"start": v(-54.84, 241.9) * mm, "end": v(-43.6, 222.46) * mm});
            skLineSegment(sketch, "E59.1", {"start": v(-43.6, 222.46) * mm, "end": v(-66.07, 222.46) * mm});
            skLineSegment(sketch, "E59.2", {"start": v(-66.07, 222.46) * mm, "end": v(-54.84, 241.9) * mm});
            skPoint(sketch, "E59.0.midPoint", {"position": v(-49.22, 232.18) * mm});
            skCircle(sketch, "E60.cCircle", {"center": v(-72.11, 216.5) * mm, "radius": 3.14 * mm, "construction": true});
            skLineSegment(sketch, "E60.0", {"start": v(-68.98, 218.31) * mm, "end": v(-68.98, 214.7) * mm});
            skLineSegment(sketch, "E60.1", {"start": v(-68.98, 214.7) * mm, "end": v(-72.11, 212.88) * mm});
            skLineSegment(sketch, "E60.2", {"start": v(-72.11, 212.88) * mm, "end": v(-75.25, 214.7) * mm});
            skLineSegment(sketch, "E60.3", {"start": v(-75.25, 214.7) * mm, "end": v(-75.25, 218.31) * mm});
            skLineSegment(sketch, "E60.4", {"start": v(-75.25, 218.31) * mm, "end": v(-72.11, 220.13) * mm});
            skLineSegment(sketch, "E60.5", {"start": v(-72.11, 220.13) * mm, "end": v(-68.98, 218.31) * mm});
            skPoint(sketch, "E60.0.midPoint", {"position": v(-68.98, 216.5) * mm});
            skCircle(sketch, "E61.cCircle", {"center": v(-147.37, 171.65) * mm, "radius": 4.24 * mm, "construction": true});
            skLineSegment(sketch, "E61.0", {"start": v(-140.03, 175.89) * mm, "end": v(-147.37, 163.17) * mm});
            skLineSegment(sketch, "E61.1", {"start": v(-147.37, 163.17) * mm, "end": v(-154.71, 175.89) * mm});
            skLineSegment(sketch, "E61.2", {"start": v(-154.71, 175.89) * mm, "end": v(-140.03, 175.89) * mm});
            skPoint(sketch, "E61.0.midPoint", {"position": v(-143.7, 169.53) * mm});
            skCircle(sketch, "E62.cCircle", {"center": v(-134, 199.86) * mm, "radius": 7.27 * mm, "construction": true});
            skLineSegment(sketch, "E62.0", {"start": v(-121.4, 207.12) * mm, "end": v(-134, 185.32) * mm});
            skLineSegment(sketch, "E62.1", {"start": v(-134, 185.32) * mm, "end": v(-146.58, 207.12) * mm});
            skLineSegment(sketch, "E62.2", {"start": v(-146.58, 207.12) * mm, "end": v(-121.4, 207.12) * mm});
            skPoint(sketch, "E62.0.midPoint", {"position": v(-127.7, 196.22) * mm});
            skCircle(sketch, "E63.cCircle", {"center": v(-148.04, 187.9) * mm, "radius": 4.45 * mm, "construction": true});
            skLineSegment(sketch, "E63.0", {"start": v(-148.04, 196.81) * mm, "end": v(-140.33, 183.46) * mm});
            skLineSegment(sketch, "E63.1", {"start": v(-140.33, 183.46) * mm, "end": v(-155.75, 183.46) * mm});
            skLineSegment(sketch, "E63.2", {"start": v(-155.75, 183.46) * mm, "end": v(-148.04, 196.81) * mm});
            skPoint(sketch, "E63.0.midPoint", {"position": v(-144.18, 190.13) * mm});
            skCircle(sketch, "E64.cCircle", {"center": v(-134.83, 179.9) * mm, "radius": 3.14 * mm, "construction": true});
            skLineSegment(sketch, "E64.0", {"start": v(-131.69, 181.7) * mm, "end": v(-131.69, 178.08) * mm});
            skLineSegment(sketch, "E64.1", {"start": v(-131.69, 178.08) * mm, "end": v(-134.83, 176.27) * mm});
            skLineSegment(sketch, "E64.2", {"start": v(-134.83, 176.27) * mm, "end": v(-137.97, 178.08) * mm});
            skLineSegment(sketch, "E64.3", {"start": v(-137.97, 178.08) * mm, "end": v(-137.97, 181.7) * mm});
            skLineSegment(sketch, "E64.4", {"start": v(-137.97, 181.7) * mm, "end": v(-134.83, 183.51) * mm});
            skLineSegment(sketch, "E64.5", {"start": v(-134.83, 183.51) * mm, "end": v(-131.69, 181.7) * mm});
            skCircle(sketch, "E65.cCircle", {"center": v(-151.7, 140.32) * mm, "radius": 2.6 * mm, "construction": true});
            skLineSegment(sketch, "E65.0", {"start": v(-147.2, 142.91) * mm, "end": v(-151.7, 135.13) * mm});
            skLineSegment(sketch, "E65.1", {"start": v(-151.7, 135.13) * mm, "end": v(-156.2, 142.91) * mm});
            skLineSegment(sketch, "E65.2", {"start": v(-156.2, 142.91) * mm, "end": v(-147.2, 142.91) * mm});
            skPoint(sketch, "E65.0.midPoint", {"position": v(-149.45, 139.02) * mm});
            skCircle(sketch, "E66.cCircle", {"center": v(-151.88, 153.6) * mm, "radius": 2.76 * mm, "construction": true});
            skLineSegment(sketch, "E66.0", {"start": v(-151.88, 159.12) * mm, "end": v(-147.1, 150.84) * mm});
            skLineSegment(sketch, "E66.1", {"start": v(-147.1, 150.84) * mm, "end": v(-156.66, 150.84) * mm});
            skLineSegment(sketch, "E66.2", {"start": v(-156.66, 150.84) * mm, "end": v(-151.88, 159.12) * mm});
            skPoint(sketch, "E66.0.midPoint", {"position": v(-149.5, 154.98) * mm});
            skCircle(sketch, "E67.cCircle", {"center": v(-141.52, 147.1) * mm, "radius": 3.14 * mm, "construction": true});
            skLineSegment(sketch, "E67.0", {"start": v(-138.38, 148.92) * mm, "end": v(-138.38, 145.3) * mm});
            skLineSegment(sketch, "E67.1", {"start": v(-138.38, 145.3) * mm, "end": v(-141.52, 143.48) * mm});
            skLineSegment(sketch, "E67.2", {"start": v(-141.52, 143.48) * mm, "end": v(-144.65, 145.3) * mm});
            skLineSegment(sketch, "E67.3", {"start": v(-144.65, 145.3) * mm, "end": v(-144.65, 148.92) * mm});
            skLineSegment(sketch, "E67.4", {"start": v(-144.65, 148.92) * mm, "end": v(-141.52, 150.73) * mm});
            skLineSegment(sketch, "E67.5", {"start": v(-141.52, 150.73) * mm, "end": v(-138.38, 148.92) * mm});
            skPoint(sketch, "E67.0.midPoint", {"position": v(-138.38, 147.1) * mm});
            skCircle(sketch, "E68.cCircle", {"center": v(-141.52, 158.69) * mm, "radius": 2.37 * mm, "construction": true});
            skLineSegment(sketch, "E68.0", {"start": v(-137.41, 161.06) * mm, "end": v(-141.52, 153.95) * mm});
            skLineSegment(sketch, "E68.1", {"start": v(-141.52, 153.95) * mm, "end": v(-145.62, 161.06) * mm});
            skLineSegment(sketch, "E68.2", {"start": v(-145.62, 161.06) * mm, "end": v(-137.41, 161.06) * mm});
            skPoint(sketch, "E68.0.midPoint", {"position": v(-139.46, 157.5) * mm});
            skCircle(sketch, "E69.cCircle", {"center": v(-141.66, 134) * mm, "radius": 2.81 * mm, "construction": true});
            skLineSegment(sketch, "E69.0", {"start": v(-141.66, 139.63) * mm, "end": v(-136.8, 131.2) * mm});
            skLineSegment(sketch, "E69.1", {"start": v(-136.8, 131.2) * mm, "end": v(-146.53, 131.2) * mm});
            skLineSegment(sketch, "E69.2", {"start": v(-146.53, 131.2) * mm, "end": v(-141.66, 139.63) * mm});
            skPoint(sketch, "E69.0.midPoint", {"position": v(-139.23, 135.41) * mm});
            skCircle(sketch, "E70.cCircle", {"center": v(-91.97, 210.43) * mm, "radius": 4 * mm, "construction": true});
            skLineSegment(sketch, "E70.0", {"start": v(-85.03, 214.44) * mm, "end": v(-91.97, 202.42) * mm});
            skLineSegment(sketch, "E70.1", {"start": v(-91.97, 202.42) * mm, "end": v(-98.92, 214.44) * mm});
            skLineSegment(sketch, "E70.2", {"start": v(-98.92, 214.44) * mm, "end": v(-85.03, 214.44) * mm});
            skPoint(sketch, "E70.0.midPoint", {"position": v(-88.5, 208.43) * mm});
            skCircle(sketch, "E71.cCircle", {"center": v(-109.55, 204.5) * mm, "radius": 2.55 * mm, "construction": true});
            skLineSegment(sketch, "E71.0", {"start": v(-109.55, 209.6) * mm, "end": v(-105.12, 201.94) * mm});
            skLineSegment(sketch, "E71.1", {"start": v(-105.12, 201.94) * mm, "end": v(-113.97, 201.94) * mm});
            skLineSegment(sketch, "E71.2", {"start": v(-113.97, 201.94) * mm, "end": v(-109.55, 209.6) * mm});
            skPoint(sketch, "E71.0.midPoint", {"position": v(-107.33, 205.77) * mm});
            skCircle(sketch, "E72.cCircle", {"center": v(-71.31, 203.07) * mm, "radius": 2.38 * mm, "construction": true});
            skLineSegment(sketch, "E72.0", {"start": v(-71.31, 207.82) * mm, "end": v(-67.2, 200.7) * mm});
            skLineSegment(sketch, "E72.1", {"start": v(-67.2, 200.7) * mm, "end": v(-75.43, 200.7) * mm});
            skLineSegment(sketch, "E72.2", {"start": v(-75.43, 200.7) * mm, "end": v(-71.31, 207.82) * mm});
            skPoint(sketch, "E72.0.midPoint", {"position": v(-69.26, 204.26) * mm});
            skCircle(sketch, "E73.cCircle", {"center": v(-15.04, 86) * mm, "radius": 7.27 * mm, "construction": true});
            skLineSegment(sketch, "E73.0", {"start": v(-2.46, 93.27) * mm, "end": v(-15.04, 71.46) * mm});
            skLineSegment(sketch, "E73.1", {"start": v(-15.04, 71.46) * mm, "end": v(-27.63, 93.27) * mm});
            skLineSegment(sketch, "E73.2", {"start": v(-27.63, 93.27) * mm, "end": v(-2.46, 93.27) * mm});
            skPoint(sketch, "E73.0.midPoint", {"position": v(-8.75, 82.37) * mm});
            skCircle(sketch, "E74.cCircle", {"center": v(-33.52, 74.7) * mm, "radius": 6.73 * mm, "construction": true});
            skLineSegment(sketch, "E74.0", {"start": v(-33.52, 88.16) * mm, "end": v(-21.85, 67.96) * mm});
            skLineSegment(sketch, "E74.1", {"start": v(-21.85, 67.96) * mm, "end": v(-45.18, 67.96) * mm});
            skLineSegment(sketch, "E74.2", {"start": v(-45.18, 67.96) * mm, "end": v(-33.52, 88.16) * mm});
            skPoint(sketch, "E74.0.midPoint", {"position": v(-27.68, 78.06) * mm});
            skCircle(sketch, "E75.cCircle", {"center": v(-15.92, 65.01) * mm, "radius": 2.77 * mm, "construction": true});
            skLineSegment(sketch, "E75.0", {"start": v(-12.81, 65.8) * mm, "end": v(-13.68, 62.72) * mm});
            skLineSegment(sketch, "E75.1", {"start": v(-13.68, 62.72) * mm, "end": v(-16.78, 61.93) * mm});
            skLineSegment(sketch, "E75.2", {"start": v(-16.78, 61.93) * mm, "end": v(-19.02, 64.22) * mm});
            skLineSegment(sketch, "E75.3", {"start": v(-19.02, 64.22) * mm, "end": v(-18.15, 67.3) * mm});
            skLineSegment(sketch, "E75.4", {"start": v(-18.15, 67.3) * mm, "end": v(-15.05, 68.1) * mm});
            skLineSegment(sketch, "E75.5", {"start": v(-15.05, 68.1) * mm, "end": v(-12.81, 65.8) * mm});
            skCircle(sketch, "E76.cCircle", {"center": v(-27.59, 110.42) * mm, "radius": 5.87 * mm, "construction": true});
            skLineSegment(sketch, "E76.0", {"start": v(-27.59, 122.17) * mm, "end": v(-17.41, 104.55) * mm});
            skLineSegment(sketch, "E76.1", {"start": v(-17.41, 104.55) * mm, "end": v(-37.77, 104.55) * mm});
            skLineSegment(sketch, "E76.2", {"start": v(-37.77, 104.55) * mm, "end": v(-27.59, 122.17) * mm});
            skPoint(sketch, "E76.0.midPoint", {"position": v(-22.5, 113.36) * mm});
            skCircle(sketch, "E77.cCircle", {"center": v(-44.06, 123.23) * mm, "radius": 5.7 * mm, "construction": true});
            skLineSegment(sketch, "E77.0", {"start": v(-34.19, 128.93) * mm, "end": v(-44.06, 111.84) * mm});
            skLineSegment(sketch, "E77.1", {"start": v(-44.06, 111.84) * mm, "end": v(-53.93, 128.93) * mm});
            skLineSegment(sketch, "E77.2", {"start": v(-53.93, 128.93) * mm, "end": v(-34.19, 128.93) * mm});
            skPoint(sketch, "E77.0.midPoint", {"position": v(-39.12, 120.38) * mm});
            skCircle(sketch, "E78.cCircle", {"center": v(-45.32, 140.43) * mm, "radius": 4.33 * mm, "construction": true});
            skLineSegment(sketch, "E78.0", {"start": v(-45.32, 149.1) * mm, "end": v(-37.82, 136.1) * mm});
            skLineSegment(sketch, "E78.1", {"start": v(-37.82, 136.1) * mm, "end": v(-52.83, 136.1) * mm});
            skLineSegment(sketch, "E78.2", {"start": v(-52.83, 136.1) * mm, "end": v(-45.32, 149.1) * mm});
            skPoint(sketch, "E78.0.midPoint", {"position": v(-41.57, 142.6) * mm});
            skCircle(sketch, "E79.cCircle", {"center": v(-48.03, 169.13) * mm, "radius": 2.7 * mm, "construction": true});
            skLineSegment(sketch, "E79.0", {"start": v(-43.37, 171.82) * mm, "end": v(-48.03, 163.74) * mm});
            skLineSegment(sketch, "E79.1", {"start": v(-48.03, 163.74) * mm, "end": v(-52.7, 171.82) * mm});
            skLineSegment(sketch, "E79.2", {"start": v(-52.7, 171.82) * mm, "end": v(-43.37, 171.82) * mm});
            skPoint(sketch, "E79.0.midPoint", {"position": v(-45.7, 167.78) * mm});
            skCircle(sketch, "E80.cCircle", {"center": v(-49.3, 186.32) * mm, "radius": 3.26 * mm, "construction": true});
            skLineSegment(sketch, "E80.0", {"start": v(-49.3, 192.84) * mm, "end": v(-43.65, 183.07) * mm});
            skLineSegment(sketch, "E80.1", {"start": v(-43.65, 183.07) * mm, "end": v(-54.94, 183.07) * mm});
            skLineSegment(sketch, "E80.2", {"start": v(-54.94, 183.07) * mm, "end": v(-49.3, 192.84) * mm});
            skPoint(sketch, "E80.0.midPoint", {"position": v(-46.48, 187.95) * mm});
            skCircle(sketch, "E81.cCircle", {"center": v(-150.99, 67.45) * mm, "radius": 2.92 * mm, "construction": true});
            skLineSegment(sketch, "E81.0", {"start": v(-145.93, 70.37) * mm, "end": v(-150.99, 61.6) * mm});
            skLineSegment(sketch, "E81.1", {"start": v(-150.99, 61.6) * mm, "end": v(-156.05, 70.37) * mm});
            skLineSegment(sketch, "E81.2", {"start": v(-156.05, 70.37) * mm, "end": v(-145.93, 70.37) * mm});
            skPoint(sketch, "E81.0.midPoint", {"position": v(-148.46, 65.98) * mm});
            skCircle(sketch, "E82.cCircle", {"center": v(-152.32, 79.3) * mm, "radius": 2.24 * mm, "construction": true});
            skLineSegment(sketch, "E82.0", {"start": v(-152.32, 83.78) * mm, "end": v(-148.45, 77.07) * mm});
            skLineSegment(sketch, "E82.1", {"start": v(-148.45, 77.07) * mm, "end": v(-156.2, 77.07) * mm});
            skLineSegment(sketch, "E82.2", {"start": v(-156.2, 77.07) * mm, "end": v(-152.32, 83.78) * mm});
            skPoint(sketch, "E82.0.midPoint", {"position": v(-150.38, 80.43) * mm});
            skCircle(sketch, "E83.cCircle", {"center": v(-118.08, 79.15) * mm, "radius": 3.14 * mm, "construction": true});
            skLineSegment(sketch, "E83.0", {"start": v(-114.94, 80.96) * mm, "end": v(-114.94, 77.34) * mm});
            skLineSegment(sketch, "E83.1", {"start": v(-114.94, 77.34) * mm, "end": v(-118.08, 75.53) * mm});
            skLineSegment(sketch, "E83.2", {"start": v(-118.08, 75.53) * mm, "end": v(-121.22, 77.34) * mm});
            skLineSegment(sketch, "E83.3", {"start": v(-121.22, 77.34) * mm, "end": v(-121.22, 80.96) * mm});
            skLineSegment(sketch, "E83.4", {"start": v(-121.22, 80.96) * mm, "end": v(-118.08, 82.77) * mm});
            skLineSegment(sketch, "E83.5", {"start": v(-118.08, 82.77) * mm, "end": v(-114.94, 80.96) * mm});
            skCircle(sketch, "E84.cCircle", {"center": v(-150.83, 11.7) * mm, "radius": 3.14 * mm, "construction": true});
            skLineSegment(sketch, "E84.0", {"start": v(-147.7, 13.52) * mm, "end": v(-147.7, 9.9) * mm});
            skLineSegment(sketch, "E84.1", {"start": v(-147.7, 9.9) * mm, "end": v(-150.83, 8.08) * mm});
            skLineSegment(sketch, "E84.2", {"start": v(-150.83, 8.08) * mm, "end": v(-153.97, 9.9) * mm});
            skLineSegment(sketch, "E84.3", {"start": v(-153.97, 9.9) * mm, "end": v(-153.97, 13.52) * mm});
            skLineSegment(sketch, "E84.4", {"start": v(-153.97, 13.52) * mm, "end": v(-150.83, 15.33) * mm});
            skLineSegment(sketch, "E84.5", {"start": v(-150.83, 15.33) * mm, "end": v(-147.7, 13.52) * mm});
            skCircle(sketch, "E85.cCircle", {"center": v(-80.84, 46.39) * mm, "radius": 3.14 * mm, "construction": true});
            skLineSegment(sketch, "E85.0", {"start": v(-77.7, 48.2) * mm, "end": v(-77.7, 44.57) * mm});
            skLineSegment(sketch, "E85.1", {"start": v(-77.7, 44.57) * mm, "end": v(-80.84, 42.76) * mm});
            skLineSegment(sketch, "E85.2", {"start": v(-80.84, 42.76) * mm, "end": v(-83.98, 44.57) * mm});
            skLineSegment(sketch, "E85.3", {"start": v(-83.98, 44.57) * mm, "end": v(-83.98, 48.2) * mm});
            skLineSegment(sketch, "E85.4", {"start": v(-83.98, 48.2) * mm, "end": v(-80.84, 50) * mm});
            skLineSegment(sketch, "E85.5", {"start": v(-80.84, 50) * mm, "end": v(-77.7, 48.2) * mm});
            skCircle(sketch, "E86.cCircle", {"center": v(-152.95, 211.34) * mm, "radius": 3.14 * mm, "construction": true});
            skLineSegment(sketch, "E86.0", {"start": v(-149.81, 213.16) * mm, "end": v(-149.81, 209.53) * mm});
            skLineSegment(sketch, "E86.1", {"start": v(-149.81, 209.53) * mm, "end": v(-152.95, 207.72) * mm});
            skLineSegment(sketch, "E86.2", {"start": v(-152.95, 207.72) * mm, "end": v(-156.1, 209.53) * mm});
            skLineSegment(sketch, "E86.3", {"start": v(-156.1, 209.53) * mm, "end": v(-156.1, 213.16) * mm});
            skLineSegment(sketch, "E86.4", {"start": v(-156.1, 213.16) * mm, "end": v(-152.95, 214.97) * mm});
            skLineSegment(sketch, "E86.5", {"start": v(-152.95, 214.97) * mm, "end": v(-149.81, 213.16) * mm});
            skCircle(sketch, "E87.cCircle", {"center": v(-48.16, 250.1) * mm, "radius": 3.14 * mm, "construction": true});
            skLineSegment(sketch, "E87.0", {"start": v(-45.02, 251.92) * mm, "end": v(-45.02, 248.3) * mm});
            skLineSegment(sketch, "E87.1", {"start": v(-45.02, 248.3) * mm, "end": v(-48.16, 246.48) * mm});
            skLineSegment(sketch, "E87.2", {"start": v(-48.16, 246.48) * mm, "end": v(-51.3, 248.3) * mm});
            skLineSegment(sketch, "E87.3", {"start": v(-51.3, 248.3) * mm, "end": v(-51.3, 251.92) * mm});
            skLineSegment(sketch, "E87.4", {"start": v(-51.3, 251.92) * mm, "end": v(-48.16, 253.73) * mm});
            skLineSegment(sketch, "E87.5", {"start": v(-48.16, 253.73) * mm, "end": v(-45.02, 251.92) * mm});
            skCircle(sketch, "E88.cCircle", {"center": v(-122.4, 273.2) * mm, "radius": 3.14 * mm, "construction": true});
            skLineSegment(sketch, "E88.0", {"start": v(-119.27, 275.01) * mm, "end": v(-119.27, 271.39) * mm});
            skLineSegment(sketch, "E88.1", {"start": v(-119.27, 271.39) * mm, "end": v(-122.4, 269.58) * mm});
            skLineSegment(sketch, "E88.2", {"start": v(-122.4, 269.58) * mm, "end": v(-125.54, 271.39) * mm});
            skLineSegment(sketch, "E88.3", {"start": v(-125.54, 271.39) * mm, "end": v(-125.54, 275.01) * mm});
            skLineSegment(sketch, "E88.4", {"start": v(-125.54, 275.01) * mm, "end": v(-122.4, 276.82) * mm});
            skLineSegment(sketch, "E88.5", {"start": v(-122.4, 276.82) * mm, "end": v(-119.27, 275.01) * mm});
            skCircle(sketch, "E89.cCircle", {"center": v(-47.93, 302.93) * mm, "radius": 3.14 * mm, "construction": true});
            skLineSegment(sketch, "E89.0", {"start": v(-44.79, 304.74) * mm, "end": v(-44.79, 301.11) * mm});
            skLineSegment(sketch, "E89.1", {"start": v(-44.79, 301.11) * mm, "end": v(-47.93, 299.3) * mm});
            skLineSegment(sketch, "E89.2", {"start": v(-47.93, 299.3) * mm, "end": v(-51.07, 301.11) * mm});
            skLineSegment(sketch, "E89.3", {"start": v(-51.07, 301.11) * mm, "end": v(-51.07, 304.74) * mm});
            skLineSegment(sketch, "E89.4", {"start": v(-51.07, 304.74) * mm, "end": v(-47.93, 306.55) * mm});
            skLineSegment(sketch, "E89.5", {"start": v(-47.93, 306.55) * mm, "end": v(-44.79, 304.74) * mm});
            skLineSegment(sketch, "E90.MirrorCS", {"start": v(77.33, 281.66) * mm, "end": v(77.33, 278.04) * mm});
            skLineSegment(sketch, "E91.MirrorCS", {"start": v(83.6, 278.04) * mm, "end": v(83.6, 281.66) * mm});
            skLineSegment(sketch, "E92.MirrorCS", {"start": v(80.47, 276.23) * mm, "end": v(83.6, 278.04) * mm});
            skLineSegment(sketch, "E93.MirrorCS", {"start": v(83.6, 281.66) * mm, "end": v(80.47, 283.47) * mm});
            skLineSegment(sketch, "E94.MirrorCS", {"start": v(144.65, 145.3) * mm, "end": v(144.65, 148.92) * mm});
            skLineSegment(sketch, "E95.MirrorCS", {"start": v(137.41, 161.06) * mm, "end": v(141.52, 153.95) * mm});
            skLineSegment(sketch, "E96.MirrorCS", {"start": v(138.38, 145.3) * mm, "end": v(141.52, 143.48) * mm});
            skLineSegment(sketch, "E97.MirrorCS", {"start": v(138.38, 148.92) * mm, "end": v(138.38, 145.3) * mm});
            skLineSegment(sketch, "E98.MirrorCS", {"start": v(141.52, 143.48) * mm, "end": v(144.65, 145.3) * mm});
            skLineSegment(sketch, "E99.MirrorCS", {"start": v(77.33, 278.04) * mm, "end": v(80.47, 276.23) * mm});
            skCircle(sketch, "E100.MirrorC", {"center": v(80.47, 279.85) * mm, "radius": 3.14 * mm, "construction": true});
            skLineSegment(sketch, "E101.MirrorCS", {"start": v(80.47, 283.47) * mm, "end": v(77.33, 281.66) * mm});
            skLineSegment(sketch, "E102.MirrorCS", {"start": v(144.65, 148.92) * mm, "end": v(141.52, 150.73) * mm});
            skLineSegment(sketch, "E103.MirrorCS", {"start": v(141.52, 150.73) * mm, "end": v(138.38, 148.92) * mm});
            skCircle(sketch, "E104.MirrorC", {"center": v(141.52, 147.1) * mm, "radius": 3.14 * mm, "construction": true});
            skLineSegment(sketch, "E105.MirrorCS", {"start": v(141.52, 153.95) * mm, "end": v(145.62, 161.06) * mm});
            skCircle(sketch, "E106.MirrorC", {"center": v(141.52, 158.69) * mm, "radius": 2.37 * mm, "construction": true});
            skLineSegment(sketch, "E107.MirrorCS", {"start": v(124.8, 40.12) * mm, "end": v(127.93, 38.3) * mm});
            skLineSegment(sketch, "E108.MirrorCS", {"start": v(72.11, 220.13) * mm, "end": v(68.98, 218.31) * mm});
            skLineSegment(sketch, "E109.MirrorCS", {"start": v(134.83, 176.27) * mm, "end": v(137.97, 178.08) * mm});
            skLineSegment(sketch, "E110.MirrorCS", {"start": v(137.97, 181.7) * mm, "end": v(134.83, 183.51) * mm});
            skLineSegment(sketch, "E111.MirrorCS", {"start": v(127.93, 45.55) * mm, "end": v(124.8, 43.74) * mm});
            skLineSegment(sketch, "E112.MirrorCS", {"start": v(68.98, 214.7) * mm, "end": v(72.11, 212.88) * mm});
            skLineSegment(sketch, "E113.MirrorCS", {"start": v(131.07, 43.74) * mm, "end": v(127.93, 45.55) * mm});
            skLineSegment(sketch, "E114.MirrorCS", {"start": v(75.25, 218.31) * mm, "end": v(72.11, 220.13) * mm});
            skLineSegment(sketch, "E115.MirrorCS", {"start": v(127.93, 38.3) * mm, "end": v(131.07, 40.12) * mm});
            skLineSegment(sketch, "E116.MirrorCS", {"start": v(114.94, 77.34) * mm, "end": v(118.08, 75.53) * mm});
            skLineSegment(sketch, "E117.MirrorCS", {"start": v(147.2, 142.91) * mm, "end": v(151.7, 135.13) * mm});
            skLineSegment(sketch, "E118.MirrorCS", {"start": v(121.22, 80.96) * mm, "end": v(118.08, 82.77) * mm});
            skLineSegment(sketch, "E119.MirrorCS", {"start": v(131.69, 181.7) * mm, "end": v(131.69, 178.08) * mm});
            skLineSegment(sketch, "E120.MirrorCS", {"start": v(119.27, 275.01) * mm, "end": v(119.27, 271.39) * mm});
            skLineSegment(sketch, "E121.MirrorCS", {"start": v(121.22, 77.34) * mm, "end": v(121.22, 80.96) * mm});
            skLineSegment(sketch, "E122.MirrorCS", {"start": v(151.88, 159.12) * mm, "end": v(147.1, 150.84) * mm});
            skLineSegment(sketch, "E123.MirrorCS", {"start": v(134.83, 183.51) * mm, "end": v(131.69, 181.7) * mm});
            skLineSegment(sketch, "E124.MirrorCS", {"start": v(118.08, 75.53) * mm, "end": v(121.22, 77.34) * mm});
            skLineSegment(sketch, "E125.MirrorCS", {"start": v(147.1, 150.84) * mm, "end": v(156.66, 150.84) * mm});
            skLineSegment(sketch, "E126.MirrorCS", {"start": v(72.11, 212.88) * mm, "end": v(75.25, 214.7) * mm});
            skLineSegment(sketch, "E127.MirrorCS", {"start": v(78.38, 87.17) * mm, "end": v(81.51, 88.98) * mm});
            skLineSegment(sketch, "E128.MirrorCS", {"start": v(137.97, 178.08) * mm, "end": v(137.97, 181.7) * mm});
            skLineSegment(sketch, "E129.MirrorCS", {"start": v(77.7, 48.2) * mm, "end": v(77.7, 44.57) * mm});
            skLineSegment(sketch, "E130.MirrorCS", {"start": v(156.2, 77.07) * mm, "end": v(152.32, 83.78) * mm});
            skLineSegment(sketch, "E131.MirrorCS", {"start": v(12.81, 65.8) * mm, "end": v(13.68, 62.72) * mm});
            skLineSegment(sketch, "E132.MirrorCS", {"start": v(75.24, 88.98) * mm, "end": v(78.38, 87.17) * mm});
            skLineSegment(sketch, "E133.MirrorCS", {"start": v(16.78, 61.93) * mm, "end": v(19.02, 64.22) * mm});
            skCircle(sketch, "E134.MirrorC", {"center": v(118.08, 79.15) * mm, "radius": 3.14 * mm, "construction": true});
            skLineSegment(sketch, "E135.MirrorCS", {"start": v(19.02, 64.22) * mm, "end": v(18.15, 67.3) * mm});
            skLineSegment(sketch, "E136.MirrorCS", {"start": v(114.94, 80.96) * mm, "end": v(114.94, 77.34) * mm});
            skLineSegment(sketch, "E137.MirrorCS", {"start": v(128.26, 234.75) * mm, "end": v(131.4, 236.56) * mm});
            skLineSegment(sketch, "E138.MirrorCS", {"start": v(44.79, 301.11) * mm, "end": v(47.93, 299.3) * mm});
            skLineSegment(sketch, "E139.MirrorCS", {"start": v(71.31, 207.82) * mm, "end": v(67.2, 200.7) * mm});
            skCircle(sketch, "E140.MirrorC", {"center": v(151.7, 140.32) * mm, "radius": 2.6 * mm, "construction": true});
            skLineSegment(sketch, "E141.MirrorCS", {"start": v(131.69, 178.08) * mm, "end": v(134.83, 176.27) * mm});
            skLineSegment(sketch, "E142.MirrorCS", {"start": v(18.15, 67.3) * mm, "end": v(15.05, 68.1) * mm});
            skLineSegment(sketch, "E143.MirrorCS", {"start": v(151.7, 135.13) * mm, "end": v(156.2, 142.91) * mm});
            skLineSegment(sketch, "E144.MirrorCS", {"start": v(139.37, 108.99) * mm, "end": v(135.55, 111.2) * mm});
            skLineSegment(sketch, "E145.MirrorCS", {"start": v(131.73, 108.99) * mm, "end": v(131.73, 104.57) * mm});
            skLineSegment(sketch, "E146.MirrorCS", {"start": v(122.4, 276.82) * mm, "end": v(119.27, 275.01) * mm});
            skLineSegment(sketch, "E147.MirrorCS", {"start": v(68.98, 218.31) * mm, "end": v(68.98, 214.7) * mm});
            skLineSegment(sketch, "E148.MirrorCS", {"start": v(156.66, 150.84) * mm, "end": v(151.88, 159.12) * mm});
            skCircle(sketch, "E149.MirrorC", {"center": v(127.93, 41.93) * mm, "radius": 3.14 * mm, "construction": true});
            skLineSegment(sketch, "E150.MirrorCS", {"start": v(156.2, 142.91) * mm, "end": v(147.2, 142.91) * mm});
            skLineSegment(sketch, "E151.MirrorCS", {"start": v(119.27, 271.39) * mm, "end": v(122.4, 269.58) * mm});
            skCircle(sketch, "E152.MirrorC", {"center": v(134.83, 179.9) * mm, "radius": 3.14 * mm, "construction": true});
            skCircle(sketch, "E153.MirrorC", {"center": v(72.11, 216.5) * mm, "radius": 3.14 * mm, "construction": true});
            skLineSegment(sketch, "E154.MirrorCS", {"start": v(139.37, 104.57) * mm, "end": v(139.37, 108.99) * mm});
            skLineSegment(sketch, "E155.MirrorCS", {"start": v(78.38, 94.42) * mm, "end": v(75.24, 92.6) * mm});
            skLineSegment(sketch, "E156.MirrorCS", {"start": v(125.54, 271.39) * mm, "end": v(125.54, 275.01) * mm});
            skLineSegment(sketch, "E157.MirrorCS", {"start": v(15.05, 68.1) * mm, "end": v(12.81, 65.8) * mm});
            skLineSegment(sketch, "E158.MirrorCS", {"start": v(75.25, 214.7) * mm, "end": v(75.25, 218.31) * mm});
            skLineSegment(sketch, "E159.MirrorCS", {"start": v(125.12, 236.56) * mm, "end": v(128.26, 234.75) * mm});
            skLineSegment(sketch, "E160.MirrorCS", {"start": v(81.51, 92.6) * mm, "end": v(78.38, 94.42) * mm});
            skLineSegment(sketch, "E161.MirrorCS", {"start": v(131.07, 40.12) * mm, "end": v(131.07, 43.74) * mm});
            skLineSegment(sketch, "E162.MirrorCS", {"start": v(122.4, 269.58) * mm, "end": v(125.54, 271.39) * mm});
            skLineSegment(sketch, "E163.MirrorCS", {"start": v(124.8, 43.74) * mm, "end": v(124.8, 40.12) * mm});
            skLineSegment(sketch, "E164.MirrorCS", {"start": v(118.08, 82.77) * mm, "end": v(114.94, 80.96) * mm});
            skLineSegment(sketch, "E165.MirrorCS", {"start": v(149.81, 213.16) * mm, "end": v(149.81, 209.53) * mm});
            skLineSegment(sketch, "E166.MirrorCS", {"start": v(109.8, 213.99) * mm, "end": v(121.44, 234.16) * mm});
            skLineSegment(sketch, "E167.MirrorCS", {"start": v(119.35, 86.53) * mm, "end": v(129.1, 103.44) * mm});
            skLineSegment(sketch, "E168.MirrorCS", {"start": v(131.4, 240.18) * mm, "end": v(128.26, 242) * mm});
            skCircle(sketch, "E169.MirrorC", {"center": v(147.37, 171.65) * mm, "radius": 4.24 * mm, "construction": true});
            skLineSegment(sketch, "E170.MirrorCS", {"start": v(13.68, 62.72) * mm, "end": v(16.78, 61.93) * mm});
            skLineSegment(sketch, "E171.MirrorCS", {"start": v(45.02, 248.3) * mm, "end": v(48.16, 246.48) * mm});
            skLineSegment(sketch, "E172.MirrorCS", {"start": v(148.45, 77.07) * mm, "end": v(156.2, 77.07) * mm});
            skLineSegment(sketch, "E173.MirrorCS", {"start": v(131.4, 236.56) * mm, "end": v(131.4, 240.18) * mm});
            skLineSegment(sketch, "E174.MirrorCS", {"start": v(109.59, 103.44) * mm, "end": v(119.35, 86.53) * mm});
            skLineSegment(sketch, "E175.MirrorCS", {"start": v(148.8, 121.14) * mm, "end": v(142.12, 109.55) * mm});
            skLineSegment(sketch, "E176.MirrorCS", {"start": v(81.51, 88.98) * mm, "end": v(81.51, 92.6) * mm});
            skLineSegment(sketch, "E177.MirrorCS", {"start": v(113.97, 201.94) * mm, "end": v(109.55, 209.6) * mm});
            skLineSegment(sketch, "E178.MirrorCS", {"start": v(140.03, 175.89) * mm, "end": v(147.37, 163.17) * mm});
            skLineSegment(sketch, "E179.MirrorCS", {"start": v(77.7, 44.57) * mm, "end": v(80.84, 42.76) * mm});
            skLineSegment(sketch, "E180.MirrorCS", {"start": v(51.3, 248.3) * mm, "end": v(51.3, 251.92) * mm});
            skLineSegment(sketch, "E181.MirrorCS", {"start": v(47.93, 299.3) * mm, "end": v(51.07, 301.11) * mm});
            skLineSegment(sketch, "E182.MirrorCS", {"start": v(45.02, 251.92) * mm, "end": v(45.02, 248.3) * mm});
            skCircle(sketch, "E183.MirrorC", {"center": v(15.92, 65.01) * mm, "radius": 2.77 * mm, "construction": true});
            skLineSegment(sketch, "E184.MirrorCS", {"start": v(152.32, 83.78) * mm, "end": v(148.45, 77.07) * mm});
            skLineSegment(sketch, "E185.MirrorCS", {"start": v(75.24, 92.6) * mm, "end": v(75.24, 88.98) * mm});
            skCircle(sketch, "E186.MirrorC", {"center": v(119.35, 97.8) * mm, "radius": 5.63 * mm, "construction": true});
            skLineSegment(sketch, "E187.MirrorCS", {"start": v(80.84, 42.76) * mm, "end": v(83.98, 44.57) * mm});
            skLineSegment(sketch, "E188.MirrorCS", {"start": v(128.26, 242) * mm, "end": v(125.12, 240.18) * mm});
            skCircle(sketch, "E189.MirrorC", {"center": v(152.32, 79.3) * mm, "radius": 2.24 * mm, "construction": true});
            skLineSegment(sketch, "E190.MirrorCS", {"start": v(125.12, 240.18) * mm, "end": v(125.12, 236.56) * mm});
            skLineSegment(sketch, "E191.MirrorCS", {"start": v(135.92, 117.23) * mm, "end": v(141.22, 126.4) * mm});
            skCircle(sketch, "E192.MirrorC", {"center": v(109.55, 204.5) * mm, "radius": 2.55 * mm, "construction": true});
            skLineSegment(sketch, "E193.MirrorCS", {"start": v(83.98, 44.57) * mm, "end": v(83.98, 48.2) * mm});
            skLineSegment(sketch, "E194.MirrorCS", {"start": v(117.3, 211.68) * mm, "end": v(139.24, 211.68) * mm});
            skLineSegment(sketch, "E195.MirrorCS", {"start": v(145.62, 161.06) * mm, "end": v(137.41, 161.06) * mm});
            skLineSegment(sketch, "E196.MirrorCS", {"start": v(67.2, 200.7) * mm, "end": v(75.43, 200.7) * mm});
            skLineSegment(sketch, "E197.MirrorCS", {"start": v(156.1, 213.16) * mm, "end": v(152.95, 214.97) * mm});
            skCircle(sketch, "E198.MirrorC", {"center": v(128.26, 238.37) * mm, "radius": 3.14 * mm, "construction": true});
            skLineSegment(sketch, "E199.MirrorCS", {"start": v(130.63, 126.4) * mm, "end": v(135.92, 117.23) * mm});
            skLineSegment(sketch, "E200.MirrorCS", {"start": v(147.7, 9.9) * mm, "end": v(150.83, 8.08) * mm});
            skLineSegment(sketch, "E201.MirrorCS", {"start": v(156.1, 209.53) * mm, "end": v(156.1, 213.16) * mm});
            skLineSegment(sketch, "E202.MirrorCS", {"start": v(145.93, 70.37) * mm, "end": v(150.99, 61.6) * mm});
            skLineSegment(sketch, "E203.MirrorCS", {"start": v(129.1, 103.44) * mm, "end": v(109.59, 103.44) * mm});
            skCircle(sketch, "E204.MirrorC", {"center": v(78.38, 90.8) * mm, "radius": 3.14 * mm, "construction": true});
            skLineSegment(sketch, "E205.MirrorCS", {"start": v(131.73, 104.57) * mm, "end": v(135.55, 102.37) * mm});
            skLineSegment(sketch, "E206.MirrorCS", {"start": v(134.95, 98.11) * mm, "end": v(124.66, 80.29) * mm});
            skCircle(sketch, "E207.MirrorC", {"center": v(141.66, 134) * mm, "radius": 2.81 * mm, "construction": true});
            skLineSegment(sketch, "E208.MirrorCS", {"start": v(150.99, 61.6) * mm, "end": v(156.05, 70.37) * mm});
            skCircle(sketch, "E209.MirrorC", {"center": v(150.99, 67.45) * mm, "radius": 2.92 * mm, "construction": true});
            skCircle(sketch, "E210.MirrorC", {"center": v(71.31, 203.07) * mm, "radius": 2.38 * mm, "construction": true});
            skLineSegment(sketch, "E211.MirrorCS", {"start": v(75.43, 200.7) * mm, "end": v(71.31, 207.82) * mm});
            skLineSegment(sketch, "E212.MirrorCS", {"start": v(80.84, 50) * mm, "end": v(77.7, 48.2) * mm});
            skCircle(sketch, "E213.MirrorC", {"center": v(135.55, 106.78) * mm, "radius": 3.82 * mm, "construction": true});
            skLineSegment(sketch, "E214.MirrorCS", {"start": v(44.79, 304.74) * mm, "end": v(44.79, 301.11) * mm});
            skLineSegment(sketch, "E215.MirrorCS", {"start": v(135.55, 111.2) * mm, "end": v(131.73, 108.99) * mm});
            skLineSegment(sketch, "E216.MirrorCS", {"start": v(152.95, 214.97) * mm, "end": v(149.81, 213.16) * mm});
            skCircle(sketch, "E217.MirrorC", {"center": v(122.4, 273.2) * mm, "radius": 3.14 * mm, "construction": true});
            skLineSegment(sketch, "E218.MirrorCS", {"start": v(136.8, 131.2) * mm, "end": v(146.53, 131.2) * mm});
            skLineSegment(sketch, "E219.MirrorCS", {"start": v(149.81, 209.53) * mm, "end": v(152.95, 207.72) * mm});
            skLineSegment(sketch, "E220.MirrorCS", {"start": v(83.98, 48.2) * mm, "end": v(80.84, 50) * mm});
            skLineSegment(sketch, "E221.MirrorCS", {"start": v(146.53, 131.2) * mm, "end": v(141.66, 139.63) * mm});
            skLineSegment(sketch, "E222.MirrorCS", {"start": v(141.66, 139.63) * mm, "end": v(136.8, 131.2) * mm});
            skLineSegment(sketch, "E223.MirrorCS", {"start": v(125.54, 275.01) * mm, "end": v(122.4, 276.82) * mm});
            skCircle(sketch, "E224.MirrorC", {"center": v(151.88, 153.6) * mm, "radius": 2.76 * mm, "construction": true});
            skLineSegment(sketch, "E225.MirrorCS", {"start": v(156.05, 70.37) * mm, "end": v(145.93, 70.37) * mm});
            skLineSegment(sketch, "E226.MirrorCS", {"start": v(135.55, 102.37) * mm, "end": v(139.37, 104.57) * mm});
            skLineSegment(sketch, "E227.MirrorCS", {"start": v(128.26, 230.68) * mm, "end": v(117.3, 211.68) * mm});
            skLineSegment(sketch, "E228.MirrorCS", {"start": v(145.24, 80.29) * mm, "end": v(134.95, 98.11) * mm});
            skLineSegment(sketch, "E229.MirrorCS", {"start": v(97.56, 62.57) * mm, "end": v(110.78, 85.47) * mm});
            skLineSegment(sketch, "E230.MirrorCS", {"start": v(83.87, 243.74) * mm, "end": v(58.69, 243.74) * mm});
            skLineSegment(sketch, "E231.MirrorCS", {"start": v(137.05, 240.88) * mm, "end": v(155.12, 240.88) * mm});
            skLineSegment(sketch, "E232.MirrorCS", {"start": v(51.07, 304.74) * mm, "end": v(47.93, 306.55) * mm});
            skLineSegment(sketch, "E233.MirrorCS", {"start": v(48.16, 246.48) * mm, "end": v(51.3, 248.3) * mm});
            skLineSegment(sketch, "E234.MirrorCS", {"start": v(51.07, 301.11) * mm, "end": v(51.07, 304.74) * mm});
            skCircle(sketch, "E235.MirrorC", {"center": v(80.84, 46.39) * mm, "radius": 3.14 * mm, "construction": true});
            skLineSegment(sketch, "E236.MirrorCS", {"start": v(98.15, 234.16) * mm, "end": v(109.8, 213.99) * mm});
            skLineSegment(sketch, "E237.MirrorCS", {"start": v(145.4, 64.4) * mm, "end": v(134.57, 45.63) * mm});
            skLineSegment(sketch, "E238.MirrorCS", {"start": v(128.66, 47.87) * mm, "end": v(142.73, 72.24) * mm});
            skLineSegment(sketch, "E239.MirrorCS", {"start": v(142.73, 72.24) * mm, "end": v(114.59, 72.24) * mm});
            skLineSegment(sketch, "E240.MirrorCS", {"start": v(89.75, 238.63) * mm, "end": v(78.08, 218.42) * mm});
            skLineSegment(sketch, "E241.MirrorCS", {"start": v(47.93, 306.55) * mm, "end": v(44.79, 304.74) * mm});
            skLineSegment(sketch, "E242.MirrorCS", {"start": v(43.37, 171.82) * mm, "end": v(48.03, 163.74) * mm});
            skLineSegment(sketch, "E243.MirrorCS", {"start": v(150.83, 15.33) * mm, "end": v(147.7, 13.52) * mm});
            skLineSegment(sketch, "E244.MirrorCS", {"start": v(58.69, 243.74) * mm, "end": v(71.28, 221.93) * mm});
            skCircle(sketch, "E245.MirrorC", {"center": v(109.8, 227.44) * mm, "radius": 6.72 * mm, "construction": true});
            skCircle(sketch, "E246.MirrorC", {"center": v(48.16, 250.1) * mm, "radius": 3.14 * mm, "construction": true});
            skLineSegment(sketch, "E247.MirrorCS", {"start": v(153.97, 13.52) * mm, "end": v(150.83, 15.33) * mm});
            skLineSegment(sketch, "E248.MirrorCS", {"start": v(128.98, 245.46) * mm, "end": v(139.33, 263.4) * mm});
            skLineSegment(sketch, "E249.MirrorCS", {"start": v(43.62, 92.46) * mm, "end": v(71.17, 92.46) * mm});
            skLineSegment(sketch, "E250.MirrorCS", {"start": v(118.63, 263.4) * mm, "end": v(128.98, 245.46) * mm});
            skLineSegment(sketch, "E251.MirrorCS", {"start": v(139.24, 211.68) * mm, "end": v(128.26, 230.68) * mm});
            skLineSegment(sketch, "E252.MirrorCS", {"start": v(48.16, 253.73) * mm, "end": v(45.02, 251.92) * mm});
            skLineSegment(sketch, "E253.MirrorCS", {"start": v(113.52, 110.24) * mm, "end": v(128.03, 110.24) * mm});
            skLineSegment(sketch, "E254.MirrorCS", {"start": v(124.66, 80.29) * mm, "end": v(145.24, 80.29) * mm});
            skLineSegment(sketch, "E255.MirrorCS", {"start": v(57.4, 116.32) * mm, "end": v(43.62, 92.46) * mm});
            skLineSegment(sketch, "E256.MirrorCS", {"start": v(150.83, 8.08) * mm, "end": v(153.97, 9.9) * mm});
            skLineSegment(sketch, "E257.MirrorCS", {"start": v(110.78, 85.47) * mm, "end": v(84.34, 85.47) * mm});
            skCircle(sketch, "E258.MirrorC", {"center": v(152.95, 211.34) * mm, "radius": 3.14 * mm, "construction": true});
            skLineSegment(sketch, "E259.MirrorCS", {"start": v(141.22, 126.4) * mm, "end": v(130.63, 126.4) * mm});
            skCircle(sketch, "E260.MirrorC", {"center": v(91.97, 210.43) * mm, "radius": 4 * mm, "construction": true});
            skCircle(sketch, "E261.MirrorC", {"center": v(128.26, 218.01) * mm, "radius": 6.33 * mm, "construction": true});
            skLineSegment(sketch, "E262.MirrorCS", {"start": v(34.19, 128.93) * mm, "end": v(44.06, 111.84) * mm});
            skLineSegment(sketch, "E263.MirrorCS", {"start": v(98.92, 214.44) * mm, "end": v(85.03, 214.44) * mm});
            skLineSegment(sketch, "E264.MirrorCS", {"start": v(121.4, 207.12) * mm, "end": v(134, 185.32) * mm});
            skLineSegment(sketch, "E265.MirrorCS", {"start": v(140.33, 183.46) * mm, "end": v(155.75, 183.46) * mm});
            skLineSegment(sketch, "E266.MirrorCS", {"start": v(100.83, 241.75) * mm, "end": v(121.77, 241.75) * mm});
            skCircle(sketch, "E267.MirrorC", {"center": v(134.95, 86.23) * mm, "radius": 5.94 * mm, "construction": true});
            skLineSegment(sketch, "E268.MirrorCS", {"start": v(121.44, 234.16) * mm, "end": v(98.15, 234.16) * mm});
            skLineSegment(sketch, "E269.MirrorCS", {"start": v(78.08, 218.42) * mm, "end": v(101.41, 218.42) * mm});
            skLineSegment(sketch, "E270.MirrorCS", {"start": v(141.07, 101.95) * mm, "end": v(148.63, 88.87) * mm});
            skLineSegment(sketch, "E271.MirrorCS", {"start": v(134, 185.32) * mm, "end": v(146.58, 207.12) * mm});
            skCircle(sketch, "E272.MirrorC", {"center": v(55.1, 206.8) * mm, "radius": 6.34 * mm, "construction": true});
            skCircle(sketch, "E273.MirrorC", {"center": v(47.93, 302.93) * mm, "radius": 3.14 * mm, "construction": true});
            skLineSegment(sketch, "E274.MirrorCS", {"start": v(51.3, 251.92) * mm, "end": v(48.16, 253.73) * mm});
            skLineSegment(sketch, "E275.MirrorCS", {"start": v(101.41, 218.42) * mm, "end": v(89.75, 238.63) * mm});
            skCircle(sketch, "E276.MirrorC", {"center": v(89.75, 225.16) * mm, "radius": 6.73 * mm, "construction": true});
            skLineSegment(sketch, "E277.MirrorCS", {"start": v(148.04, 196.81) * mm, "end": v(140.33, 183.46) * mm});
            skLineSegment(sketch, "E278.MirrorCS", {"start": v(146.58, 207.12) * mm, "end": v(121.4, 207.12) * mm});
            skLineSegment(sketch, "E279.MirrorCS", {"start": v(152.95, 207.72) * mm, "end": v(156.1, 209.53) * mm});
            skLineSegment(sketch, "E280.MirrorCS", {"start": v(133.92, 36.75) * mm, "end": v(144.4, 18.62) * mm});
            skLineSegment(sketch, "E281.MirrorCS", {"start": v(134.36, 235.03) * mm, "end": v(144.83, 216.9) * mm});
            skLineSegment(sketch, "E282.MirrorCS", {"start": v(66.07, 222.46) * mm, "end": v(54.84, 241.9) * mm});
            skLineSegment(sketch, "E283.MirrorCS", {"start": v(153.97, 9.9) * mm, "end": v(153.97, 13.52) * mm});
            skLineSegment(sketch, "E284.MirrorCS", {"start": v(121.77, 241.75) * mm, "end": v(111.3, 259.88) * mm});
            skCircle(sketch, "E285.MirrorC", {"center": v(135.92, 123.34) * mm, "radius": 3.06 * mm, "construction": true});
            skLineSegment(sketch, "E286.MirrorCS", {"start": v(147.7, 13.52) * mm, "end": v(147.7, 9.9) * mm});
            skLineSegment(sketch, "E287.MirrorCS", {"start": v(134.57, 45.63) * mm, "end": v(156.23, 45.63) * mm});
            skLineSegment(sketch, "E288.MirrorCS", {"start": v(99.62, 254.73) * mm, "end": v(112.54, 277.12) * mm});
            skLineSegment(sketch, "E289.MirrorCS", {"start": v(142.12, 109.55) * mm, "end": v(155.5, 109.55) * mm});
            skLineSegment(sketch, "E290.MirrorCS", {"start": v(52.83, 136.1) * mm, "end": v(45.32, 149.1) * mm});
            skLineSegment(sketch, "E291.MirrorCS", {"start": v(37.82, 136.1) * mm, "end": v(52.83, 136.1) * mm});
            skLineSegment(sketch, "E292.MirrorCS", {"start": v(109.55, 209.6) * mm, "end": v(105.12, 201.94) * mm});
            skLineSegment(sketch, "E293.MirrorCS", {"start": v(146.09, 256.53) * mm, "end": v(137.05, 240.88) * mm});
            skLineSegment(sketch, "E294.MirrorCS", {"start": v(71.28, 221.93) * mm, "end": v(83.87, 243.74) * mm});
            skLineSegment(sketch, "E295.MirrorCS", {"start": v(86.7, 277.12) * mm, "end": v(99.62, 254.73) * mm});
            skLineSegment(sketch, "E296.MirrorCS", {"start": v(84.34, 85.47) * mm, "end": v(97.56, 62.57) * mm});
            skLineSegment(sketch, "E297.MirrorCS", {"start": v(114.59, 72.24) * mm, "end": v(128.66, 47.87) * mm});
            skLineSegment(sketch, "E298.MirrorCS", {"start": v(155.12, 240.88) * mm, "end": v(146.09, 256.53) * mm});
            skLineSegment(sketch, "E299.MirrorCS", {"start": v(154.86, 36.75) * mm, "end": v(133.92, 36.75) * mm});
            skCircle(sketch, "E300.MirrorC", {"center": v(128.66, 64.11) * mm, "radius": 8.12 * mm, "construction": true});
            skCircle(sketch, "E301.MirrorC", {"center": v(48.03, 169.13) * mm, "radius": 2.7 * mm, "construction": true});
            skLineSegment(sketch, "E302.MirrorCS", {"start": v(45.32, 149.1) * mm, "end": v(37.82, 136.1) * mm});
            skCircle(sketch, "E303.MirrorC", {"center": v(146.09, 246.1) * mm, "radius": 5.22 * mm, "construction": true});
            skLineSegment(sketch, "E304.MirrorCS", {"start": v(147.37, 163.17) * mm, "end": v(154.71, 175.89) * mm});
            skCircle(sketch, "E305.MirrorC", {"center": v(148.8, 113.42) * mm, "radius": 3.86 * mm, "construction": true});
            skCircle(sketch, "E306.MirrorC", {"center": v(145.4, 51.88) * mm, "radius": 6.25 * mm, "construction": true});
            skCircle(sketch, "E307.MirrorC", {"center": v(97.56, 77.84) * mm, "radius": 7.63 * mm, "construction": true});
            skLineSegment(sketch, "E308.MirrorCS", {"start": v(59.99, 307.26) * mm, "end": v(46.22, 283.41) * mm});
            skCircle(sketch, "E309.MirrorC", {"center": v(45.32, 140.43) * mm, "radius": 4.33 * mm, "construction": true});
            skLineSegment(sketch, "E310.MirrorCS", {"start": v(66.06, 213.14) * mm, "end": v(44.12, 213.14) * mm});
            skLineSegment(sketch, "E311.MirrorCS", {"start": v(71.17, 92.46) * mm, "end": v(57.4, 116.32) * mm});
            skLineSegment(sketch, "E312.MirrorCS", {"start": v(64.98, 248.16) * mm, "end": v(95.25, 248.16) * mm});
            skLineSegment(sketch, "E313.MirrorCS", {"start": v(155.75, 183.46) * mm, "end": v(148.04, 196.81) * mm});
            skLineSegment(sketch, "E314.MirrorCS", {"start": v(85.03, 214.44) * mm, "end": v(91.97, 202.42) * mm});
            skLineSegment(sketch, "E315.MirrorCS", {"start": v(155.3, 235.03) * mm, "end": v(134.36, 235.03) * mm});
            skLineSegment(sketch, "E316.MirrorCS", {"start": v(80.12, 274.37) * mm, "end": v(64.98, 248.16) * mm});
            skLineSegment(sketch, "E317.MirrorCS", {"start": v(48.03, 163.74) * mm, "end": v(52.7, 171.82) * mm});
            skCircle(sketch, "E318.MirrorC", {"center": v(49.3, 186.32) * mm, "radius": 3.26 * mm, "construction": true});
            skLineSegment(sketch, "E319.MirrorCS", {"start": v(111.3, 259.88) * mm, "end": v(100.83, 241.75) * mm});
            skCircle(sketch, "E320.MirrorC", {"center": v(134, 199.86) * mm, "radius": 7.27 * mm, "construction": true});
            skLineSegment(sketch, "E321.MirrorCS", {"start": v(44.06, 111.84) * mm, "end": v(53.93, 128.93) * mm});
            skCircle(sketch, "E322.MirrorC", {"center": v(148.63, 97.6) * mm, "radius": 4.36 * mm, "construction": true});
            skLineSegment(sketch, "E323.MirrorCS", {"start": v(49.3, 192.84) * mm, "end": v(43.65, 183.07) * mm});
            skLineSegment(sketch, "E324.MirrorCS", {"start": v(54.84, 241.9) * mm, "end": v(43.6, 222.46) * mm});
            skLineSegment(sketch, "E325.MirrorCS", {"start": v(67.05, 307.08) * mm, "end": v(79.64, 285.28) * mm});
            skLineSegment(sketch, "E326.MirrorCS", {"start": v(55.1, 194.13) * mm, "end": v(66.06, 213.14) * mm});
            skLineSegment(sketch, "E327.MirrorCS", {"start": v(106.43, 67.9) * mm, "end": v(93.72, 45.9) * mm});
            skCircle(sketch, "E328.MirrorC", {"center": v(54.84, 228.94) * mm, "radius": 6.48 * mm, "construction": true});
            skCircle(sketch, "E329.MirrorC", {"center": v(71.28, 236.47) * mm, "radius": 7.27 * mm, "construction": true});
            skLineSegment(sketch, "E330.MirrorCS", {"start": v(71.82, 86) * mm, "end": v(42.47, 86) * mm});
            skLineSegment(sketch, "E331.MirrorCS", {"start": v(141.7, 10.03) * mm, "end": v(126.56, 36.24) * mm});
            skLineSegment(sketch, "E332.MirrorCS", {"start": v(91.97, 202.42) * mm, "end": v(98.92, 214.44) * mm});
            skCircle(sketch, "E333.MirrorC", {"center": v(97.92, 99.18) * mm, "radius": 7.55 * mm, "construction": true});
            skCircle(sketch, "E334.MirrorC", {"center": v(144.83, 228.98) * mm, "radius": 6.05 * mm, "construction": true});
            skLineSegment(sketch, "E335.MirrorCS", {"start": v(52.7, 171.82) * mm, "end": v(43.37, 171.82) * mm});
            skCircle(sketch, "E336.MirrorC", {"center": v(144.4, 30.7) * mm, "radius": 6.05 * mm, "construction": true});
            skLineSegment(sketch, "E337.MirrorCS", {"start": v(95.25, 248.16) * mm, "end": v(80.12, 274.37) * mm});
            skLineSegment(sketch, "E338.MirrorCS", {"start": v(119.14, 45.9) * mm, "end": v(106.43, 67.9) * mm});
            skLineSegment(sketch, "E339.MirrorCS", {"start": v(93.72, 56.9) * mm, "end": v(78.58, 83.12) * mm});
            skCircle(sketch, "E340.MirrorC", {"center": v(148.04, 187.9) * mm, "radius": 4.45 * mm, "construction": true});
            skLineSegment(sketch, "E341.MirrorCS", {"start": v(44.12, 213.14) * mm, "end": v(55.1, 194.13) * mm});
            skLineSegment(sketch, "E342.MirrorCS", {"start": v(33.52, 88.16) * mm, "end": v(21.85, 67.96) * mm});
            skLineSegment(sketch, "E343.MirrorCS", {"start": v(86.44, 281.77) * mm, "end": v(109.77, 281.77) * mm});
            skCircle(sketch, "E344.MirrorC", {"center": v(128.98, 257.41) * mm, "radius": 5.98 * mm, "construction": true});
            skLineSegment(sketch, "E345.MirrorCS", {"start": v(112.54, 277.12) * mm, "end": v(86.7, 277.12) * mm});
            skLineSegment(sketch, "E346.MirrorCS", {"start": v(155.5, 109.55) * mm, "end": v(148.8, 121.14) * mm});
            skLineSegment(sketch, "E347.MirrorCS", {"start": v(68.07, 115.21) * mm, "end": v(77.79, 98.37) * mm});
            skLineSegment(sketch, "E348.MirrorCS", {"start": v(139.33, 263.4) * mm, "end": v(118.63, 263.4) * mm});
            skLineSegment(sketch, "E349.MirrorCS", {"start": v(84.83, 91.63) * mm, "end": v(111, 91.63) * mm});
            skLineSegment(sketch, "E350.MirrorCS", {"start": v(148.63, 88.87) * mm, "end": v(156.18, 101.95) * mm});
            skCircle(sketch, "E351.MirrorC", {"center": v(150.83, 11.7) * mm, "radius": 3.14 * mm, "construction": true});
            skLineSegment(sketch, "E352.MirrorCS", {"start": v(59.74, 251.52) * mm, "end": v(74.42, 276.94) * mm});
            skLineSegment(sketch, "E353.MirrorCS", {"start": v(98.1, 301.97) * mm, "end": v(86.44, 281.77) * mm});
            skCircle(sketch, "E354.MirrorC", {"center": v(111.3, 247.8) * mm, "radius": 6.04 * mm, "construction": true});
            skCircle(sketch, "E355.MirrorC", {"center": v(57.4, 100.41) * mm, "radius": 7.95 * mm, "construction": true});
            skLineSegment(sketch, "E356.MirrorCS", {"start": v(54.94, 183.07) * mm, "end": v(49.3, 192.84) * mm});
            skCircle(sketch, "E357.MirrorC", {"center": v(44.06, 123.23) * mm, "radius": 5.7 * mm, "construction": true});
            skLineSegment(sketch, "E358.MirrorCS", {"start": v(43.6, 222.46) * mm, "end": v(66.07, 222.46) * mm});
            skLineSegment(sketch, "E359.MirrorCS", {"start": v(120.77, 122.8) * mm, "end": v(113.52, 110.24) * mm});
            skLineSegment(sketch, "E360.MirrorCS", {"start": v(53.93, 128.93) * mm, "end": v(34.19, 128.93) * mm});
            skLineSegment(sketch, "E361.MirrorCS", {"start": v(17.41, 104.55) * mm, "end": v(37.77, 104.55) * mm});
            skLineSegment(sketch, "E362.MirrorCS", {"start": v(43.65, 183.07) * mm, "end": v(54.94, 183.07) * mm});
            skLineSegment(sketch, "E363.MirrorCS", {"start": v(105.12, 201.94) * mm, "end": v(113.97, 201.94) * mm});
            skCircle(sketch, "E364.MirrorC", {"center": v(106.18, 30.34) * mm, "radius": 8.47 * mm, "construction": true});
            skLineSegment(sketch, "E365.MirrorCS", {"start": v(91.5, 38.81) * mm, "end": v(106.18, 13.39) * mm});
            skLineSegment(sketch, "E366.MirrorCS", {"start": v(106.18, 13.39) * mm, "end": v(120.86, 38.81) * mm});
            skLineSegment(sketch, "E367.MirrorCS", {"start": v(120.86, 38.81) * mm, "end": v(91.5, 38.81) * mm});
            skCircle(sketch, "E368.MirrorC", {"center": v(126.56, 18.76) * mm, "radius": 8.74 * mm, "construction": true});
            skLineSegment(sketch, "E369.MirrorCS", {"start": v(126.56, 36.24) * mm, "end": v(111.42, 10.03) * mm});
            skCircle(sketch, "E370.MirrorC", {"center": v(99.62, 269.66) * mm, "radius": 7.46 * mm, "construction": true});
            skLineSegment(sketch, "E371.MirrorCS", {"start": v(78.58, 83.12) * mm, "end": v(63.45, 56.9) * mm});
            skLineSegment(sketch, "E372.MirrorCS", {"start": v(45.18, 67.96) * mm, "end": v(33.52, 88.16) * mm});
            skLineSegment(sketch, "E373.MirrorCS", {"start": v(46.22, 283.41) * mm, "end": v(73.76, 283.41) * mm});
            skLineSegment(sketch, "E374.MirrorCS", {"start": v(63.45, 56.9) * mm, "end": v(93.72, 56.9) * mm});
            skCircle(sketch, "E375.MirrorC", {"center": v(77.79, 109.6) * mm, "radius": 5.61 * mm, "construction": true});
            skCircle(sketch, "E376.MirrorC", {"center": v(106.43, 53.23) * mm, "radius": 7.34 * mm, "construction": true});
            skLineSegment(sketch, "E377.MirrorCS", {"start": v(154.71, 175.89) * mm, "end": v(140.03, 175.89) * mm});
            skLineSegment(sketch, "E378.MirrorCS", {"start": v(93.72, 45.9) * mm, "end": v(119.14, 45.9) * mm});
            skLineSegment(sketch, "E379.MirrorCS", {"start": v(79.64, 285.28) * mm, "end": v(92.22, 307.08) * mm});
            skCircle(sketch, "E380.MirrorC", {"center": v(27.59, 110.42) * mm, "radius": 5.87 * mm, "construction": true});
            skCircle(sketch, "E381.MirrorC", {"center": v(59.74, 268.47) * mm, "radius": 8.47 * mm, "construction": true});
            skLineSegment(sketch, "E382.MirrorCS", {"start": v(92.22, 307.08) * mm, "end": v(67.05, 307.08) * mm});
            skLineSegment(sketch, "E383.MirrorCS", {"start": v(156.23, 45.63) * mm, "end": v(145.4, 64.4) * mm});
            skLineSegment(sketch, "E384.MirrorCS", {"start": v(77.79, 98.37) * mm, "end": v(87.51, 115.21) * mm});
            skCircle(sketch, "E385.MirrorC", {"center": v(33.52, 74.7) * mm, "radius": 6.73 * mm, "construction": true});
            skLineSegment(sketch, "E386.MirrorCS", {"start": v(111, 91.63) * mm, "end": v(97.92, 114.3) * mm});
            skCircle(sketch, "E387.MirrorC", {"center": v(79.64, 299.81) * mm, "radius": 7.27 * mm, "construction": true});
            skCircle(sketch, "E388.MirrorC", {"center": v(57.15, 77.52) * mm, "radius": 8.47 * mm, "construction": true});
            skCircle(sketch, "E389.MirrorC", {"center": v(98.1, 288.5) * mm, "radius": 6.73 * mm, "construction": true});
            skLineSegment(sketch, "E390.MirrorCS", {"start": v(27.59, 122.17) * mm, "end": v(17.41, 104.55) * mm});
            skLineSegment(sketch, "E391.MirrorCS", {"start": v(128.03, 110.24) * mm, "end": v(120.77, 122.8) * mm});
            skLineSegment(sketch, "E392.MirrorCS", {"start": v(45.06, 276.94) * mm, "end": v(59.74, 251.52) * mm});
            skLineSegment(sketch, "E393.MirrorCS", {"start": v(97.92, 114.3) * mm, "end": v(84.83, 91.63) * mm});
            skCircle(sketch, "E394.MirrorC", {"center": v(120.77, 114.42) * mm, "radius": 4.19 * mm, "construction": true});
            skCircle(sketch, "E395.MirrorC", {"center": v(59.99, 291.36) * mm, "radius": 7.95 * mm, "construction": true});
            skLineSegment(sketch, "E396.MirrorCS", {"start": v(74.42, 276.94) * mm, "end": v(45.06, 276.94) * mm});
            skLineSegment(sketch, "E397.MirrorCS", {"start": v(156.18, 101.95) * mm, "end": v(141.07, 101.95) * mm});
            skLineSegment(sketch, "E398.MirrorCS", {"start": v(144.4, 18.62) * mm, "end": v(154.86, 36.75) * mm});
            skLineSegment(sketch, "E399.MirrorCS", {"start": v(144.83, 216.9) * mm, "end": v(155.3, 235.03) * mm});
            skLineSegment(sketch, "E400.MirrorCS", {"start": v(57.15, 60.57) * mm, "end": v(71.82, 86) * mm});
            skLineSegment(sketch, "E401.MirrorCS", {"start": v(37.77, 104.55) * mm, "end": v(27.59, 122.17) * mm});
            skCircle(sketch, "E402.MirrorC", {"center": v(80.12, 256.9) * mm, "radius": 8.74 * mm, "construction": true});
            skCircle(sketch, "E403.MirrorC", {"center": v(78.58, 65.64) * mm, "radius": 8.74 * mm, "construction": true});
            skLineSegment(sketch, "E404.MirrorCS", {"start": v(111.42, 10.03) * mm, "end": v(141.7, 10.03) * mm});
            skLineSegment(sketch, "E405.MirrorCS", {"start": v(109.77, 281.77) * mm, "end": v(98.1, 301.97) * mm});
            skLineSegment(sketch, "E406.MirrorCS", {"start": v(73.76, 283.41) * mm, "end": v(59.99, 307.26) * mm});
            skLineSegment(sketch, "E407.MirrorCS", {"start": v(21.85, 67.96) * mm, "end": v(45.18, 67.96) * mm});
            skLineSegment(sketch, "E408.MirrorCS", {"start": v(87.51, 115.21) * mm, "end": v(68.07, 115.21) * mm});
            skLineSegment(sketch, "E409.MirrorCS", {"start": v(42.47, 86) * mm, "end": v(57.15, 60.57) * mm});
            skPoint(sketch, "E410.MirrorP", {"position": v(50.51, 104.39) * mm});
            skPoint(sketch, "E411.MirrorP", {"position": v(138.38, 147.1) * mm});
            skPoint(sketch, "E412.MirrorP", {"position": v(45.7, 167.78) * mm});
            skPoint(sketch, "E413.MirrorP", {"position": v(107.33, 205.77) * mm});
            skPoint(sketch, "E414.MirrorP", {"position": v(125.12, 238.37) * mm});
            skPoint(sketch, "E415.MirrorP", {"position": v(127.7, 196.22) * mm});
            skPoint(sketch, "E416.MirrorP", {"position": v(119, 23.13) * mm});
            skPoint(sketch, "E417.MirrorP", {"position": v(72.93, 106.8) * mm});
            skPoint(sketch, "E418.MirrorP", {"position": v(117.15, 116.52) * mm});
            skPoint(sketch, "E419.MirrorP", {"position": v(122.78, 221.18) * mm});
            skPoint(sketch, "E420.MirrorP", {"position": v(91.37, 102.96) * mm});
            skPoint(sketch, "E421.MirrorP", {"position": v(139.16, 27.69) * mm});
            skPoint(sketch, "E422.MirrorP", {"position": v(77.33, 279.85) * mm});
            skPoint(sketch, "E423.MirrorP", {"position": v(144.18, 190.13) * mm});
            skPoint(sketch, "E424.MirrorP", {"position": v(103.97, 224.08) * mm});
            skPoint(sketch, "E425.MirrorP", {"position": v(68.98, 216.5) * mm});
            skPoint(sketch, "E426.MirrorP", {"position": v(39.12, 120.38) * mm});
            skPoint(sketch, "E427.MirrorP", {"position": v(49.6, 203.63) * mm});
            skPoint(sketch, "E428.MirrorP", {"position": v(90.95, 74.02) * mm});
            skPoint(sketch, "E429.MirrorP", {"position": v(148.46, 65.98) * mm});
            skPoint(sketch, "E430.MirrorP", {"position": v(149.45, 139.02) * mm});
            skPoint(sketch, "E431.MirrorP", {"position": v(150.38, 80.43) * mm});
            skPoint(sketch, "E432.MirrorP", {"position": v(145.46, 115.35) * mm});
            skPoint(sketch, "E433.MirrorP", {"position": v(27.68, 78.06) * mm});
            skPoint(sketch, "E434.MirrorP", {"position": v(22.5, 113.36) * mm});
            skPoint(sketch, "E435.MirrorP", {"position": v(75.24, 90.8) * mm});
            skPoint(sketch, "E436.MirrorP", {"position": v(71.02, 70) * mm});
            skPoint(sketch, "E437.MirrorP", {"position": v(133.28, 121.82) * mm});
            skPoint(sketch, "E438.MirrorP", {"position": v(53.1, 295.34) * mm});
            skPoint(sketch, "E439.MirrorP", {"position": v(139.6, 225.96) * mm});
            skPoint(sketch, "E440.MirrorP", {"position": v(69.26, 204.26) * mm});
            skPoint(sketch, "E441.MirrorP", {"position": v(46.48, 187.95) * mm});
            skPoint(sketch, "E442.MirrorP", {"position": v(49.8, 73.28) * mm});
            skPoint(sketch, "E443.MirrorP", {"position": v(114.47, 94.98) * mm});
            skPoint(sketch, "E444.MirrorP", {"position": v(93.15, 265.93) * mm});
            skPoint(sketch, "E445.MirrorP", {"position": v(64.98, 232.83) * mm});
            skPoint(sketch, "E446.MirrorP", {"position": v(121.62, 60.05) * mm});
            skPoint(sketch, "E447.MirrorP", {"position": v(139.23, 135.41) * mm});
            skPoint(sketch, "E448.MirrorP", {"position": v(149.5, 154.98) * mm});
            skPoint(sketch, "E449.MirrorP", {"position": v(131.73, 106.78) * mm});
            skPoint(sketch, "E450.MirrorP", {"position": v(88.5, 208.43) * mm});
            skPoint(sketch, "E451.MirrorP", {"position": v(92.27, 291.87) * mm});
            skPoint(sketch, "E452.MirrorP", {"position": v(124.8, 41.93) * mm});
            skPoint(sketch, "E453.MirrorP", {"position": v(49.22, 232.18) * mm});
            skPoint(sketch, "E454.MirrorP", {"position": v(143.7, 169.53) * mm});
            skPoint(sketch, "E455.MirrorP", {"position": v(41.57, 142.6) * mm});
            skPoint(sketch, "E456.MirrorP", {"position": v(139.98, 55.01) * mm});
            skPoint(sketch, "E457.MirrorP", {"position": v(139.46, 157.5) * mm});
            skPoint(sketch, "E458.MirrorP", {"position": v(123.8, 254.43) * mm});
            skPoint(sketch, "E459.MirrorP", {"position": v(52.4, 264.23) * mm});
            skPoint(sketch, "E460.MirrorP", {"position": v(144.85, 95.41) * mm});
            skPoint(sketch, "E461.MirrorP", {"position": v(73.34, 296.18) * mm});
            skPoint(sketch, "E462.MirrorP", {"position": v(83.92, 228.53) * mm});
            skPoint(sketch, "E463.MirrorP", {"position": v(100.08, 56.9) * mm});
            skPoint(sketch, "E464.MirrorP", {"position": v(72.55, 261.26) * mm});
            skPoint(sketch, "E465.MirrorP", {"position": v(129.8, 89.2) * mm});
            skPoint(sketch, "E466.MirrorP", {"position": v(98.84, 26.1) * mm});
            skPoint(sketch, "E467.MirrorP", {"position": v(141.57, 248.7) * mm});
            skPoint(sketch, "E468.MirrorP", {"position": v(106.07, 250.81) * mm});
            skCircle(sketch, "E469.cCircle", {"center": v(16, 87.89) * mm, "radius": 7.27 * mm, "construction": true});
            skLineSegment(sketch, "E469.0", {"start": v(28.58, 95.16) * mm, "end": v(16, 73.35) * mm});
            skLineSegment(sketch, "E469.1", {"start": v(16, 73.35) * mm, "end": v(3.4, 95.16) * mm});
            skLineSegment(sketch, "E469.2", {"start": v(3.4, 95.16) * mm, "end": v(28.58, 95.16) * mm});
            skPoint(sketch, "E469.0.midPoint", {"position": v(22.29, 84.26) * mm});
            skCircle(sketch, "E470.cCircle", {"center": v(-35.97, 95.51) * mm, "radius": 2.77 * mm, "construction": true});
            skLineSegment(sketch, "E470.0", {"start": v(-32.87, 96.3) * mm, "end": v(-33.73, 93.22) * mm});
            skLineSegment(sketch, "E470.1", {"start": v(-33.73, 93.22) * mm, "end": v(-36.83, 92.43) * mm});
            skLineSegment(sketch, "E470.2", {"start": v(-36.83, 92.43) * mm, "end": v(-39.07, 94.72) * mm});
            skLineSegment(sketch, "E470.3", {"start": v(-39.07, 94.72) * mm, "end": v(-38.2, 97.8) * mm});
            skLineSegment(sketch, "E470.4", {"start": v(-38.2, 97.8) * mm, "end": v(-35.1, 98.6) * mm});
            skLineSegment(sketch, "E470.5", {"start": v(-35.1, 98.6) * mm, "end": v(-32.87, 96.3) * mm});
            skCircle(sketch, "E471.cCircle", {"center": v(37.18, 95.51) * mm, "radius": 2.77 * mm, "construction": true});
            skLineSegment(sketch, "E471.0", {"start": v(40.28, 96.3) * mm, "end": v(39.41, 93.22) * mm});
            skLineSegment(sketch, "E471.1", {"start": v(39.41, 93.22) * mm, "end": v(36.31, 92.43) * mm});
            skLineSegment(sketch, "E471.2", {"start": v(36.31, 92.43) * mm, "end": v(34.07, 94.72) * mm});
            skLineSegment(sketch, "E471.3", {"start": v(34.07, 94.72) * mm, "end": v(34.94, 97.8) * mm});
            skLineSegment(sketch, "E471.4", {"start": v(34.94, 97.8) * mm, "end": v(38.04, 98.6) * mm});
            skLineSegment(sketch, "E471.5", {"start": v(38.04, 98.6) * mm, "end": v(40.28, 96.3) * mm});
            skCircle(sketch, "E472.cCircle", {"center": v(-1.12, 107.07) * mm, "radius": 4.23 * mm, "construction": true});
            skLineSegment(sketch, "E472.0", {"start": v(-1.12, 115.53) * mm, "end": v(6.2, 102.84) * mm});
            skLineSegment(sketch, "E472.1", {"start": v(6.2, 102.84) * mm, "end": v(-8.44, 102.84) * mm});
            skLineSegment(sketch, "E472.2", {"start": v(-8.44, 102.84) * mm, "end": v(-1.12, 115.53) * mm});
            skPoint(sketch, "E472.0.midPoint", {"position": v(2.54, 109.18) * mm});
            skCircle(sketch, "E473.cCircle", {"center": v(0.58, 74.88) * mm, "radius": 4.57 * mm, "construction": true});
            skLineSegment(sketch, "E473.0", {"start": v(0.58, 84.02) * mm, "end": v(8.5, 70.3) * mm});
            skLineSegment(sketch, "E473.1", {"start": v(8.5, 70.3) * mm, "end": v(-7.34, 70.3) * mm});
            skLineSegment(sketch, "E473.2", {"start": v(-7.34, 70.3) * mm, "end": v(0.58, 84.02) * mm});
            skPoint(sketch, "E473.0.midPoint", {"position": v(4.53, 77.16) * mm});
            skSolve(sketch);
        }
        {
            var Q0;
            Q0=makeQuery(id+"F8.imprint","IMPRINT",FACE,{"disambiguationData":[TD([[makeQuery(id+"F8.imprint","IMPRINT",EDGE,{"derivedFrom":sQuery(id+"F8.wireOp",EDGE,"E49.0")}),-1.0]])]});
            var Q1;
            Q1=makeQuery(id+"F8.imprint","IMPRINT",FACE,{"disambiguationData":[TD([[makeQuery(id+"F8.imprint","IMPRINT",EDGE,{"derivedFrom":sQuery(id+"F8.wireOp",EDGE,"E48.0")}),-1.0]])]});
            var Q2;
            Q2=makeQuery(id+"F8.imprint","IMPRINT",FACE,{"disambiguationData":[TD([[makeQuery(id+"F8.imprint","IMPRINT",EDGE,{"derivedFrom":sQuery(id+"F8.wireOp",EDGE,"E42.0")}),-1.0]])]});
            var Q3;
            Q3=makeQuery(id+"F8.imprint","IMPRINT",FACE,{"disambiguationData":[TD([[makeQuery(id+"F8.imprint","IMPRINT",EDGE,{"derivedFrom":sQuery(id+"F8.wireOp",EDGE,"E44.0")}),-1.0]])]});
            var Q4;
            Q4=makeQuery(id+"F8.imprint","IMPRINT",FACE,{"disambiguationData":[TD([[makeQuery(id+"F8.imprint","IMPRINT",EDGE,{"derivedFrom":sQuery(id+"F8.wireOp",EDGE,"E39.0")}),-1.0]])]});
            var Q5;
            Q5=makeQuery(id+"F8.imprint","IMPRINT",FACE,{"disambiguationData":[TD([[makeQuery(id+"F8.imprint","IMPRINT",EDGE,{"derivedFrom":sQuery(id+"F8.wireOp",EDGE,"E40.0")}),-1.0]])]});
            var Q6;
            Q6=makeQuery(id+"F8.imprint","IMPRINT",FACE,{"disambiguationData":[TD([[makeQuery(id+"F8.imprint","IMPRINT",EDGE,{"derivedFrom":sQuery(id+"F8.wireOp",EDGE,"E41.0")}),-1.0]])]});
            var Q7;
            Q7=makeQuery(id+"F8.imprint","IMPRINT",FACE,{"disambiguationData":[TD([[makeQuery(id+"F8.imprint","IMPRINT",EDGE,{"derivedFrom":sQuery(id+"F8.wireOp",EDGE,"E43.0")}),-1.0]])]});
            var Q8;
            Q8=makeQuery(id+"F8.imprint","IMPRINT",FACE,{"disambiguationData":[TD([[makeQuery(id+"F8.imprint","IMPRINT",EDGE,{"derivedFrom":sQuery(id+"F8.wireOp",EDGE,"E88.0")}),-1.0]])]});
            var Q9;
            Q9=makeQuery(id+"F8.imprint","IMPRINT",FACE,{"disambiguationData":[TD([[makeQuery(id+"F8.imprint","IMPRINT",EDGE,{"derivedFrom":sQuery(id+"F8.wireOp",EDGE,"E55.0")}),-1.0]])]});
            var Q10;
            Q10=makeQuery(id+"F8.imprint","IMPRINT",FACE,{"disambiguationData":[TD([[makeQuery(id+"F8.imprint","IMPRINT",EDGE,{"derivedFrom":sQuery(id+"F8.wireOp",EDGE,"E89.0")}),-1.0]])]});
            var Q11;
            Q11=makeQuery(id+"F8.imprint","IMPRINT",FACE,{"disambiguationData":[TD([[makeQuery(id+"F8.imprint","IMPRINT",EDGE,{"derivedFrom":sQuery(id+"F8.wireOp",EDGE,"E87.0")}),-1.0]])]});
            var Q12;
            Q12=makeQuery(id+"F8.imprint","IMPRINT",FACE,{"disambiguationData":[TD([[makeQuery(id+"F8.imprint","IMPRINT",EDGE,{"derivedFrom":sQuery(id+"F8.wireOp",EDGE,"E57.0")}),-1.0]])]});
            var Q13;
            Q13=makeQuery(id+"F8.imprint","IMPRINT",FACE,{"disambiguationData":[TD([[makeQuery(id+"F8.imprint","IMPRINT",EDGE,{"derivedFrom":sQuery(id+"F8.wireOp",EDGE,"E58.0")}),-1.0]])]});
            var Q14;
            Q14=makeQuery(id+"F8.imprint","IMPRINT",FACE,{"disambiguationData":[TD([[makeQuery(id+"F8.imprint","IMPRINT",EDGE,{"derivedFrom":sQuery(id+"F8.wireOp",EDGE,"E50.0")}),-1.0]])]});
            var Q15;
            Q15=makeQuery(id+"F8.imprint","IMPRINT",FACE,{"disambiguationData":[TD([[makeQuery(id+"F8.imprint","IMPRINT",EDGE,{"derivedFrom":sQuery(id+"F8.wireOp",EDGE,"E54.0")}),-1.0]])]});
            var Q16;
            Q16=makeQuery(id+"F8.imprint","IMPRINT",FACE,{"disambiguationData":[TD([[makeQuery(id+"F8.imprint","IMPRINT",EDGE,{"derivedFrom":sQuery(id+"F8.wireOp",EDGE,"E47.0")}),-1.0]])]});
            var Q17;
            Q17=makeQuery(id+"F8.imprint","IMPRINT",FACE,{"disambiguationData":[TD([[makeQuery(id+"F8.imprint","IMPRINT",EDGE,{"derivedFrom":sQuery(id+"F8.wireOp",EDGE,"E86.0")}),-1.0]])]});
            var Q18;
            Q18=makeQuery(id+"F8.imprint","IMPRINT",FACE,{"disambiguationData":[TD([[makeQuery(id+"F8.imprint","IMPRINT",EDGE,{"derivedFrom":sQuery(id+"F8.wireOp",EDGE,"E59.0")}),-1.0]])]});
            var Q19;
            Q19=makeQuery(id+"F8.imprint","IMPRINT",FACE,{"disambiguationData":[TD([[makeQuery(id+"F8.imprint","IMPRINT",EDGE,{"derivedFrom":sQuery(id+"F8.wireOp",EDGE,"E60.0")}),-1.0]])]});
            var Q20;
            Q20=makeQuery(id+"F8.imprint","IMPRINT",FACE,{"disambiguationData":[TD([[makeQuery(id+"F8.imprint","IMPRINT",EDGE,{"derivedFrom":sQuery(id+"F8.wireOp",EDGE,"E46.0")}),-1.0]])]});
            var Q21;
            Q21=makeQuery(id+"F8.imprint","IMPRINT",FACE,{"disambiguationData":[TD([[makeQuery(id+"F8.imprint","IMPRINT",EDGE,{"derivedFrom":sQuery(id+"F8.wireOp",EDGE,"E62.0")}),-1.0]])]});
            var Q22;
            Q22=makeQuery(id+"F8.imprint","IMPRINT",FACE,{"disambiguationData":[TD([[makeQuery(id+"F8.imprint","IMPRINT",EDGE,{"derivedFrom":sQuery(id+"F8.wireOp",EDGE,"E70.0")}),-1.0]])]});
            var Q23;
            Q23=makeQuery(id+"F8.imprint","IMPRINT",FACE,{"disambiguationData":[TD([[makeQuery(id+"F8.imprint","IMPRINT",EDGE,{"derivedFrom":sQuery(id+"F8.wireOp",EDGE,"E71.0")}),-1.0]])]});
            var Q24;
            Q24=makeQuery(id+"F8.imprint","IMPRINT",FACE,{"disambiguationData":[TD([[makeQuery(id+"F8.imprint","IMPRINT",EDGE,{"derivedFrom":sQuery(id+"F8.wireOp",EDGE,"E72.0")}),-1.0]])]});
            var Q25;
            Q25=makeQuery(id+"F8.imprint","IMPRINT",FACE,{"disambiguationData":[TD([[makeQuery(id+"F8.imprint","IMPRINT",EDGE,{"derivedFrom":sQuery(id+"F8.wireOp",EDGE,"E56.0")}),-1.0]])]});
            var Q26;
            Q26=makeQuery(id+"F8.imprint","IMPRINT",FACE,{"disambiguationData":[TD([[makeQuery(id+"F8.imprint","IMPRINT",EDGE,{"derivedFrom":sQuery(id+"F8.wireOp",EDGE,"E80.0")}),-1.0]])]});
            var Q27;
            Q27=makeQuery(id+"F8.imprint","IMPRINT",FACE,{"disambiguationData":[TD([[makeQuery(id+"F8.imprint","IMPRINT",EDGE,{"derivedFrom":sQuery(id+"F8.wireOp",EDGE,"E79.0")}),-1.0]])]});
            var Q28;
            Q28=makeQuery(id+"F8.imprint","IMPRINT",FACE,{"disambiguationData":[TD([[makeQuery(id+"F8.imprint","IMPRINT",EDGE,{"derivedFrom":sQuery(id+"F8.wireOp",EDGE,"E64.0")}),-1.0]])]});
            var Q29;
            Q29=makeQuery(id+"F8.imprint","IMPRINT",FACE,{"disambiguationData":[TD([[makeQuery(id+"F8.imprint","IMPRINT",EDGE,{"derivedFrom":sQuery(id+"F8.wireOp",EDGE,"E63.0")}),-1.0]])]});
            var Q30;
            Q30=makeQuery(id+"F8.imprint","IMPRINT",FACE,{"disambiguationData":[TD([[makeQuery(id+"F8.imprint","IMPRINT",EDGE,{"derivedFrom":sQuery(id+"F8.wireOp",EDGE,"E61.0")}),-1.0]])]});
            var Q31;
            Q31=makeQuery(id+"F8.imprint","IMPRINT",FACE,{"disambiguationData":[TD([[makeQuery(id+"F8.imprint","IMPRINT",EDGE,{"derivedFrom":sQuery(id+"F8.wireOp",EDGE,"E68.0")}),-1.0]])]});
            var Q32;
            Q32=makeQuery(id+"F8.imprint","IMPRINT",FACE,{"disambiguationData":[TD([[makeQuery(id+"F8.imprint","IMPRINT",EDGE,{"derivedFrom":sQuery(id+"F8.wireOp",EDGE,"E66.0")}),-1.0]])]});
            var Q33;
            Q33=makeQuery(id+"F8.imprint","IMPRINT",FACE,{"disambiguationData":[TD([[makeQuery(id+"F8.imprint","IMPRINT",EDGE,{"derivedFrom":sQuery(id+"F8.wireOp",EDGE,"E65.0")}),-1.0]])]});
            var Q34;
            Q34=makeQuery(id+"F8.imprint","IMPRINT",FACE,{"disambiguationData":[TD([[makeQuery(id+"F8.imprint","IMPRINT",EDGE,{"derivedFrom":sQuery(id+"F8.wireOp",EDGE,"E67.0")}),-1.0]])]});
            var Q35;
            Q35=makeQuery(id+"F8.imprint","IMPRINT",FACE,{"disambiguationData":[TD([[makeQuery(id+"F8.imprint","IMPRINT",EDGE,{"derivedFrom":sQuery(id+"F8.wireOp",EDGE,"E69.0")}),-1.0]])]});
            var Q36;
            Q36=makeQuery(id+"F8.imprint","IMPRINT",FACE,{"disambiguationData":[TD([[makeQuery(id+"F8.imprint","IMPRINT",EDGE,{"derivedFrom":sQuery(id+"F8.wireOp",EDGE,"E36.0")}),-1.0]])]});
            var Q37;
            Q37=makeQuery(id+"F8.imprint","IMPRINT",FACE,{"disambiguationData":[TD([[makeQuery(id+"F8.imprint","IMPRINT",EDGE,{"derivedFrom":sQuery(id+"F8.wireOp",EDGE,"E37.0")}),-1.0]])]});
            var Q38;
            Q38=makeQuery(id+"F8.imprint","IMPRINT",FACE,{"disambiguationData":[TD([[makeQuery(id+"F8.imprint","IMPRINT",EDGE,{"derivedFrom":sQuery(id+"F8.wireOp",EDGE,"E38.0")}),-1.0]])]});
            var Q39;
            Q39=makeQuery(id+"F8.imprint","IMPRINT",FACE,{"disambiguationData":[TD([[makeQuery(id+"F8.imprint","IMPRINT",EDGE,{"derivedFrom":sQuery(id+"F8.wireOp",EDGE,"E30.0")}),-1.0]])]});
            var Q40;
            Q40=makeQuery(id+"F8.imprint","IMPRINT",FACE,{"disambiguationData":[TD([[makeQuery(id+"F8.imprint","IMPRINT",EDGE,{"derivedFrom":sQuery(id+"F8.wireOp",EDGE,"E31.0")}),-1.0]])]});
            var Q41;
            Q41=makeQuery(id+"F8.imprint","IMPRINT",FACE,{"disambiguationData":[TD([[makeQuery(id+"F8.imprint","IMPRINT",EDGE,{"derivedFrom":sQuery(id+"F8.wireOp",EDGE,"E78.0")}),-1.0]])]});
            var Q42;
            Q42=makeQuery(id+"F8.imprint","IMPRINT",FACE,{"disambiguationData":[TD([[makeQuery(id+"F8.imprint","IMPRINT",EDGE,{"derivedFrom":sQuery(id+"F8.wireOp",EDGE,"E77.0")}),-1.0]])]});
            var Q43;
            Q43=makeQuery(id+"F8.imprint","IMPRINT",FACE,{"disambiguationData":[TD([[makeQuery(id+"F8.imprint","IMPRINT",EDGE,{"derivedFrom":sQuery(id+"F8.wireOp",EDGE,"E76.0")}),-1.0]])]});
            var Q44;
            Q44=makeQuery(id+"F8.imprint","IMPRINT",FACE,{"disambiguationData":[TD([[makeQuery(id+"F8.imprint","IMPRINT",EDGE,{"derivedFrom":sQuery(id+"F8.wireOp",EDGE,"E472.0")}),-1.0]])]});
            var Q45;
            Q45=makeQuery(id+"F8.imprint","IMPRINT",FACE,{"disambiguationData":[TD([[makeQuery(id+"F8.imprint","IMPRINT",EDGE,{"derivedFrom":sQuery(id+"F8.wireOp",EDGE,"E32.0")}),-1.0]])]});
            var Q46;
            Q46=makeQuery(id+"F8.imprint","IMPRINT",FACE,{"disambiguationData":[TD([[makeQuery(id+"F8.imprint","IMPRINT",EDGE,{"derivedFrom":sQuery(id+"F8.wireOp",EDGE,"E470.0")}),-1.0]])]});
            var Q47;
            Q47=makeQuery(id+"F8.imprint","IMPRINT",FACE,{"disambiguationData":[TD([[makeQuery(id+"F8.imprint","IMPRINT",EDGE,{"derivedFrom":sQuery(id+"F8.wireOp",EDGE,"E52.0")}),-1.0]])]});
            var Q48;
            Q48=makeQuery(id+"F8.imprint","IMPRINT",FACE,{"disambiguationData":[TD([[makeQuery(id+"F8.imprint","IMPRINT",EDGE,{"derivedFrom":sQuery(id+"F8.wireOp",EDGE,"E33.0")}),-1.0]])]});
            var Q49;
            Q49=makeQuery(id+"F8.imprint","IMPRINT",FACE,{"disambiguationData":[TD([[makeQuery(id+"F8.imprint","IMPRINT",EDGE,{"derivedFrom":sQuery(id+"F8.wireOp",EDGE,"E53.0")}),-1.0]])]});
            var Q50;
            Q50=makeQuery(id+"F8.imprint","IMPRINT",FACE,{"disambiguationData":[TD([[makeQuery(id+"F8.imprint","IMPRINT",EDGE,{"derivedFrom":sQuery(id+"F8.wireOp",EDGE,"E27.0")}),-1.0]])]});
            var Q51;
            Q51=makeQuery(id+"F8.imprint","IMPRINT",FACE,{"disambiguationData":[TD([[makeQuery(id+"F8.imprint","IMPRINT",EDGE,{"derivedFrom":sQuery(id+"F8.wireOp",EDGE,"E29.0")}),-1.0]])]});
            var Q52;
            Q52=makeQuery(id+"F8.imprint","IMPRINT",FACE,{"disambiguationData":[TD([[makeQuery(id+"F8.imprint","IMPRINT",EDGE,{"derivedFrom":sQuery(id+"F8.wireOp",EDGE,"E34.0")}),-1.0]])]});
            var Q53;
            Q53=makeQuery(id+"F8.imprint","IMPRINT",FACE,{"disambiguationData":[TD([[makeQuery(id+"F8.imprint","IMPRINT",EDGE,{"derivedFrom":sQuery(id+"F8.wireOp",EDGE,"E45.0")}),-1.0]])]});
            var Q54;
            Q54=makeQuery(id+"F8.imprint","IMPRINT",FACE,{"disambiguationData":[TD([[makeQuery(id+"F8.imprint","IMPRINT",EDGE,{"derivedFrom":sQuery(id+"F8.wireOp",EDGE,"E83.0")}),-1.0]])]});
            var Q55;
            Q55=makeQuery(id+"F8.imprint","IMPRINT",FACE,{"disambiguationData":[TD([[makeQuery(id+"F8.imprint","IMPRINT",EDGE,{"derivedFrom":sQuery(id+"F8.wireOp",EDGE,"E35.0")}),-1.0]])]});
            var Q56;
            Q56=makeQuery(id+"F8.imprint","IMPRINT",FACE,{"disambiguationData":[TD([[makeQuery(id+"F8.imprint","IMPRINT",EDGE,{"derivedFrom":sQuery(id+"F8.wireOp",EDGE,"E82.0")}),-1.0]])]});
            var Q57;
            Q57=makeQuery(id+"F8.imprint","IMPRINT",FACE,{"disambiguationData":[TD([[makeQuery(id+"F8.imprint","IMPRINT",EDGE,{"derivedFrom":sQuery(id+"F8.wireOp",EDGE,"E81.0")}),-1.0]])]});
            var Q58;
            Q58=makeQuery(id+"F8.imprint","IMPRINT",FACE,{"disambiguationData":[TD([[makeQuery(id+"F8.imprint","IMPRINT",EDGE,{"derivedFrom":sQuery(id+"F8.wireOp",EDGE,"E24.0")}),-1.0]])]});
            var Q59;
            Q59=makeQuery(id+"F8.imprint","IMPRINT",FACE,{"disambiguationData":[TD([[makeQuery(id+"F8.imprint","IMPRINT",EDGE,{"derivedFrom":sQuery(id+"F8.wireOp",EDGE,"E26.0")}),-1.0]])]});
            var Q60;
            Q60=makeQuery(id+"F8.imprint","IMPRINT",FACE,{"disambiguationData":[TD([[makeQuery(id+"F8.imprint","IMPRINT",EDGE,{"derivedFrom":sQuery(id+"F8.wireOp",EDGE,"E28.0")}),-1.0]])]});
            var Q61;
            Q61=makeQuery(id+"F8.imprint","IMPRINT",FACE,{"disambiguationData":[TD([[makeQuery(id+"F8.imprint","IMPRINT",EDGE,{"derivedFrom":sQuery(id+"F8.wireOp",EDGE,"E74.0")}),-1.0]])]});
            var Q62;
            Q62=makeQuery(id+"F8.imprint","IMPRINT",FACE,{"disambiguationData":[TD([[makeQuery(id+"F8.imprint","IMPRINT",EDGE,{"derivedFrom":sQuery(id+"F8.wireOp",EDGE,"E73.0")}),-1.0]])]});
            var Q63;
            Q63=makeQuery(id+"F8.imprint","IMPRINT",FACE,{"disambiguationData":[TD([[makeQuery(id+"F8.imprint","IMPRINT",EDGE,{"derivedFrom":sQuery(id+"F8.wireOp",EDGE,"E469.0")}),-1.0]])]});
            var Q64;
            Q64=makeQuery(id+"F8.imprint","IMPRINT",FACE,{"disambiguationData":[TD([[makeQuery(id+"F8.imprint","IMPRINT",EDGE,{"derivedFrom":sQuery(id+"F8.wireOp",EDGE,"E361.MirrorCS")}),1.0]])]});
            var Q65;
            Q65=makeQuery(id+"F8.imprint","IMPRINT",FACE,{"disambiguationData":[TD([[makeQuery(id+"F8.imprint","IMPRINT",EDGE,{"derivedFrom":sQuery(id+"F8.wireOp",EDGE,"E262.MirrorCS")}),1.0]])]});
            var Q66;
            Q66=makeQuery(id+"F8.imprint","IMPRINT",FACE,{"disambiguationData":[TD([[makeQuery(id+"F8.imprint","IMPRINT",EDGE,{"derivedFrom":sQuery(id+"F8.wireOp",EDGE,"E290.MirrorCS")}),1.0]])]});
            var Q67;
            Q67=makeQuery(id+"F8.imprint","IMPRINT",FACE,{"disambiguationData":[TD([[makeQuery(id+"F8.imprint","IMPRINT",EDGE,{"derivedFrom":sQuery(id+"F8.wireOp",EDGE,"E242.MirrorCS")}),1.0]])]});
            var Q68;
            Q68=makeQuery(id+"F8.imprint","IMPRINT",FACE,{"disambiguationData":[TD([[makeQuery(id+"F8.imprint","IMPRINT",EDGE,{"derivedFrom":sQuery(id+"F8.wireOp",EDGE,"E323.MirrorCS")}),1.0]])]});
            var Q69;
            Q69=makeQuery(id+"F8.imprint","IMPRINT",FACE,{"disambiguationData":[TD([[makeQuery(id+"F8.imprint","IMPRINT",EDGE,{"derivedFrom":sQuery(id+"F8.wireOp",EDGE,"E310.MirrorCS")}),1.0]])]});
            var Q70;
            Q70=makeQuery(id+"F8.imprint","IMPRINT",FACE,{"disambiguationData":[TD([[makeQuery(id+"F8.imprint","IMPRINT",EDGE,{"derivedFrom":sQuery(id+"F8.wireOp",EDGE,"E282.MirrorCS")}),1.0]])]});
            var Q71;
            Q71=makeQuery(id+"F8.imprint","IMPRINT",FACE,{"disambiguationData":[TD([[makeQuery(id+"F8.imprint","IMPRINT",EDGE,{"derivedFrom":sQuery(id+"F8.wireOp",EDGE,"E171.MirrorCS")}),1.0]])]});
            var Q72;
            Q72=makeQuery(id+"F8.imprint","IMPRINT",FACE,{"disambiguationData":[TD([[makeQuery(id+"F8.imprint","IMPRINT",EDGE,{"derivedFrom":sQuery(id+"F8.wireOp",EDGE,"E352.MirrorCS")}),1.0]])]});
            var Q73;
            Q73=makeQuery(id+"F8.imprint","IMPRINT",FACE,{"disambiguationData":[TD([[makeQuery(id+"F8.imprint","IMPRINT",EDGE,{"derivedFrom":sQuery(id+"F8.wireOp",EDGE,"E230.MirrorCS")}),1.0]])]});
            var Q74;
            Q74=makeQuery(id+"F8.imprint","IMPRINT",FACE,{"disambiguationData":[TD([[makeQuery(id+"F8.imprint","IMPRINT",EDGE,{"derivedFrom":sQuery(id+"F8.wireOp",EDGE,"E312.MirrorCS")}),1.0]])]});
            var Q75;
            Q75=makeQuery(id+"F8.imprint","IMPRINT",FACE,{"disambiguationData":[TD([[makeQuery(id+"F8.imprint","IMPRINT",EDGE,{"derivedFrom":sQuery(id+"F8.wireOp",EDGE,"E240.MirrorCS")}),1.0]])]});
            var Q76;
            Q76=makeQuery(id+"F8.imprint","IMPRINT",FACE,{"disambiguationData":[TD([[makeQuery(id+"F8.imprint","IMPRINT",EDGE,{"derivedFrom":sQuery(id+"F8.wireOp",EDGE,"E108.MirrorCS")}),1.0]])]});
            var Q77;
            Q77=makeQuery(id+"F8.imprint","IMPRINT",FACE,{"disambiguationData":[TD([[makeQuery(id+"F8.imprint","IMPRINT",EDGE,{"derivedFrom":sQuery(id+"F8.wireOp",EDGE,"E139.MirrorCS")}),1.0]])]});
            var Q78;
            Q78=makeQuery(id+"F8.imprint","IMPRINT",FACE,{"disambiguationData":[TD([[makeQuery(id+"F8.imprint","IMPRINT",EDGE,{"derivedFrom":sQuery(id+"F8.wireOp",EDGE,"E473.0")}),-1.0]])]});
            var Q79;
            Q79=makeQuery(id+"F8.imprint","IMPRINT",FACE,{"disambiguationData":[TD([[makeQuery(id+"F8.imprint","IMPRINT",EDGE,{"derivedFrom":sQuery(id+"F8.wireOp",EDGE,"E75.0")}),-1.0]])]});
            var Q80;
            Q80=makeQuery(id+"F8.imprint","IMPRINT",FACE,{"disambiguationData":[TD([[makeQuery(id+"F8.imprint","IMPRINT",EDGE,{"derivedFrom":sQuery(id+"F8.wireOp",EDGE,"E131.MirrorCS")}),1.0]])]});
            var Q81;
            Q81=makeQuery(id+"F8.imprint","IMPRINT",FACE,{"disambiguationData":[TD([[makeQuery(id+"F8.imprint","IMPRINT",EDGE,{"derivedFrom":sQuery(id+"F8.wireOp",EDGE,"E342.MirrorCS")}),1.0]])]});
            var Q82;
            Q82=makeQuery(id+"F8.imprint","IMPRINT",FACE,{"disambiguationData":[TD([[makeQuery(id+"F8.imprint","IMPRINT",EDGE,{"derivedFrom":sQuery(id+"F8.wireOp",EDGE,"E471.0")}),-1.0]])]});
            var Q83;
            Q83=makeQuery(id+"F8.imprint","IMPRINT",FACE,{"disambiguationData":[TD([[makeQuery(id+"F8.imprint","IMPRINT",EDGE,{"derivedFrom":sQuery(id+"F8.wireOp",EDGE,"E249.MirrorCS")}),1.0]])]});
            var Q84;
            Q84=makeQuery(id+"F8.imprint","IMPRINT",FACE,{"disambiguationData":[TD([[makeQuery(id+"F8.imprint","IMPRINT",EDGE,{"derivedFrom":sQuery(id+"F8.wireOp",EDGE,"E330.MirrorCS")}),1.0]])]});
            var Q85;
            Q85=makeQuery(id+"F8.imprint","IMPRINT",FACE,{"disambiguationData":[TD([[makeQuery(id+"F8.imprint","IMPRINT",EDGE,{"derivedFrom":sQuery(id+"F8.wireOp",EDGE,"E347.MirrorCS")}),1.0]])]});
            var Q86;
            Q86=makeQuery(id+"F8.imprint","IMPRINT",FACE,{"disambiguationData":[TD([[makeQuery(id+"F8.imprint","IMPRINT",EDGE,{"derivedFrom":sQuery(id+"F8.wireOp",EDGE,"E249.MirrorCS")}),1.0]])]});
            var Q87;
            Q87=makeQuery(id+"F8.imprint","IMPRINT",FACE,{"disambiguationData":[TD([[makeQuery(id+"F8.imprint","IMPRINT",EDGE,{"derivedFrom":sQuery(id+"F8.wireOp",EDGE,"E127.MirrorCS")}),1.0]])]});
            var Q88;
            Q88=makeQuery(id+"F8.imprint","IMPRINT",FACE,{"disambiguationData":[TD([[makeQuery(id+"F8.imprint","IMPRINT",EDGE,{"derivedFrom":sQuery(id+"F8.wireOp",EDGE,"E349.MirrorCS")}),1.0]])]});
            var Q89;
            Q89=makeQuery(id+"F8.imprint","IMPRINT",FACE,{"disambiguationData":[TD([[makeQuery(id+"F8.imprint","IMPRINT",EDGE,{"derivedFrom":sQuery(id+"F8.wireOp",EDGE,"E229.MirrorCS")}),1.0]])]});
            var Q90;
            Q90=makeQuery(id+"F8.imprint","IMPRINT",FACE,{"disambiguationData":[TD([[makeQuery(id+"F8.imprint","IMPRINT",EDGE,{"derivedFrom":sQuery(id+"F8.wireOp",EDGE,"E339.MirrorCS")}),1.0]])]});
            var Q91;
            Q91=makeQuery(id+"F8.imprint","IMPRINT",FACE,{"disambiguationData":[TD([[makeQuery(id+"F8.imprint","IMPRINT",EDGE,{"derivedFrom":sQuery(id+"F8.wireOp",EDGE,"E23.0")}),-1.0]])]});
            var Q92;
            Q92=makeQuery(id+"F8.imprint","IMPRINT",FACE,{"disambiguationData":[TD([[makeQuery(id+"F8.imprint","IMPRINT",EDGE,{"derivedFrom":sQuery(id+"F8.wireOp",EDGE,"E84.0")}),-1.0]])]});
            var Q93;
            Q93=makeQuery(id+"F8.imprint","IMPRINT",FACE,{"disambiguationData":[TD([[makeQuery(id+"F8.imprint","IMPRINT",EDGE,{"derivedFrom":sQuery(id+"F8.wireOp",EDGE,"E25.0")}),-1.0]])]});
            var Q94;
            Q94=makeQuery(id+"F8.imprint","IMPRINT",FACE,{"disambiguationData":[TD([[makeQuery(id+"F8.imprint","IMPRINT",EDGE,{"derivedFrom":sQuery(id+"F8.wireOp",EDGE,"E51.0")}),-1.0]])]});
            var Q95;
            Q95=makeQuery(id+"F8.imprint","IMPRINT",FACE,{"disambiguationData":[TD([[makeQuery(id+"F8.imprint","IMPRINT",EDGE,{"derivedFrom":sQuery(id+"F8.wireOp",EDGE,"E22.0")}),-1.0]])]});
            var Q96;
            Q96=makeQuery(id+"F8.imprint","IMPRINT",FACE,{"disambiguationData":[TD([[makeQuery(id+"F8.imprint","IMPRINT",EDGE,{"derivedFrom":sQuery(id+"F8.wireOp",EDGE,"E21.0")}),-1.0]])]});
            var Q97;
            Q97=makeQuery(id+"F8.imprint","IMPRINT",FACE,{"disambiguationData":[TD([[makeQuery(id+"F8.imprint","IMPRINT",EDGE,{"derivedFrom":sQuery(id+"F8.wireOp",EDGE,"E85.0")}),-1.0]])]});
            var Q98;
            Q98=makeQuery(id+"F8.imprint","IMPRINT",FACE,{"disambiguationData":[TD([[makeQuery(id+"F8.imprint","IMPRINT",EDGE,{"derivedFrom":sQuery(id+"F8.wireOp",EDGE,"E129.MirrorCS")}),1.0]])]});
            var Q99;
            Q99=makeQuery(id+"F8.imprint","IMPRINT",FACE,{"disambiguationData":[TD([[makeQuery(id+"F8.imprint","IMPRINT",EDGE,{"derivedFrom":sQuery(id+"F8.wireOp",EDGE,"E327.MirrorCS")}),1.0]])]});
            var Q100;
            Q100=makeQuery(id+"F8.imprint","IMPRINT",FACE,{"disambiguationData":[TD([[makeQuery(id+"F8.imprint","IMPRINT",EDGE,{"derivedFrom":sQuery(id+"F8.wireOp",EDGE,"E365.MirrorCS")}),1.0]])]});
            var Q101;
            Q101=makeQuery(id+"F8.imprint","IMPRINT",FACE,{"disambiguationData":[TD([[makeQuery(id+"F8.imprint","IMPRINT",EDGE,{"derivedFrom":sQuery(id+"F8.wireOp",EDGE,"E331.MirrorCS")}),1.0]])]});
            var Q102;
            Q102=makeQuery(id+"F8.imprint","IMPRINT",FACE,{"disambiguationData":[TD([[makeQuery(id+"F8.imprint","IMPRINT",EDGE,{"derivedFrom":sQuery(id+"F8.wireOp",EDGE,"E280.MirrorCS")}),1.0]])]});
            var Q103;
            Q103=makeQuery(id+"F8.imprint","IMPRINT",FACE,{"disambiguationData":[TD([[makeQuery(id+"F8.imprint","IMPRINT",EDGE,{"derivedFrom":sQuery(id+"F8.wireOp",EDGE,"E200.MirrorCS")}),1.0]])]});
            var Q104;
            Q104=makeQuery(id+"F8.imprint","IMPRINT",FACE,{"disambiguationData":[TD([[makeQuery(id+"F8.imprint","IMPRINT",EDGE,{"derivedFrom":sQuery(id+"F8.wireOp",EDGE,"E107.MirrorCS")}),1.0]])]});
            var Q105;
            Q105=makeQuery(id+"F8.imprint","IMPRINT",FACE,{"disambiguationData":[TD([[makeQuery(id+"F8.imprint","IMPRINT",EDGE,{"derivedFrom":sQuery(id+"F8.wireOp",EDGE,"E238.MirrorCS")}),1.0]])]});
            var Q106;
            Q106=makeQuery(id+"F8.imprint","IMPRINT",FACE,{"disambiguationData":[TD([[makeQuery(id+"F8.imprint","IMPRINT",EDGE,{"derivedFrom":sQuery(id+"F8.wireOp",EDGE,"E237.MirrorCS")}),1.0]])]});
            var Q107;
            Q107=makeQuery(id+"F8.imprint","IMPRINT",FACE,{"disambiguationData":[TD([[makeQuery(id+"F8.imprint","IMPRINT",EDGE,{"derivedFrom":sQuery(id+"F8.wireOp",EDGE,"E202.MirrorCS")}),1.0]])]});
            var Q108;
            Q108=makeQuery(id+"F8.imprint","IMPRINT",FACE,{"disambiguationData":[TD([[makeQuery(id+"F8.imprint","IMPRINT",EDGE,{"derivedFrom":sQuery(id+"F8.wireOp",EDGE,"E130.MirrorCS")}),1.0]])]});
            var Q109;
            Q109=makeQuery(id+"F8.imprint","IMPRINT",FACE,{"disambiguationData":[TD([[makeQuery(id+"F8.imprint","IMPRINT",EDGE,{"derivedFrom":sQuery(id+"F8.wireOp",EDGE,"E206.MirrorCS")}),1.0]])]});
            var Q110;
            Q110=makeQuery(id+"F8.imprint","IMPRINT",FACE,{"disambiguationData":[TD([[makeQuery(id+"F8.imprint","IMPRINT",EDGE,{"derivedFrom":sQuery(id+"F8.wireOp",EDGE,"E116.MirrorCS")}),1.0]])]});
            var Q111;
            Q111=makeQuery(id+"F8.imprint","IMPRINT",FACE,{"disambiguationData":[TD([[makeQuery(id+"F8.imprint","IMPRINT",EDGE,{"derivedFrom":sQuery(id+"F8.wireOp",EDGE,"E167.MirrorCS")}),1.0]])]});
            var Q112;
            Q112=makeQuery(id+"F8.imprint","IMPRINT",FACE,{"disambiguationData":[TD([[makeQuery(id+"F8.imprint","IMPRINT",EDGE,{"derivedFrom":sQuery(id+"F8.wireOp",EDGE,"E253.MirrorCS")}),1.0]])]});
            var Q113;
            Q113=makeQuery(id+"F8.imprint","IMPRINT",FACE,{"disambiguationData":[TD([[makeQuery(id+"F8.imprint","IMPRINT",EDGE,{"derivedFrom":sQuery(id+"F8.wireOp",EDGE,"E191.MirrorCS")}),1.0]])]});
            var Q114;
            Q114=makeQuery(id+"F8.imprint","IMPRINT",FACE,{"disambiguationData":[TD([[makeQuery(id+"F8.imprint","IMPRINT",EDGE,{"derivedFrom":sQuery(id+"F8.wireOp",EDGE,"E144.MirrorCS")}),1.0]])]});
            var Q115;
            Q115=makeQuery(id+"F8.imprint","IMPRINT",FACE,{"disambiguationData":[TD([[makeQuery(id+"F8.imprint","IMPRINT",EDGE,{"derivedFrom":sQuery(id+"F8.wireOp",EDGE,"E175.MirrorCS")}),1.0]])]});
            var Q116;
            Q116=makeQuery(id+"F8.imprint","IMPRINT",FACE,{"disambiguationData":[TD([[makeQuery(id+"F8.imprint","IMPRINT",EDGE,{"derivedFrom":sQuery(id+"F8.wireOp",EDGE,"E270.MirrorCS")}),1.0]])]});
            var Q117;
            Q117=makeQuery(id+"F8.imprint","IMPRINT",FACE,{"disambiguationData":[TD([[makeQuery(id+"F8.imprint","IMPRINT",EDGE,{"derivedFrom":sQuery(id+"F8.wireOp",EDGE,"E218.MirrorCS")}),1.0]])]});
            var Q118;
            Q118=makeQuery(id+"F8.imprint","IMPRINT",FACE,{"disambiguationData":[TD([[makeQuery(id+"F8.imprint","IMPRINT",EDGE,{"derivedFrom":sQuery(id+"F8.wireOp",EDGE,"E94.MirrorCS")}),1.0]])]});
            var Q119;
            Q119=makeQuery(id+"F8.imprint","IMPRINT",FACE,{"disambiguationData":[TD([[makeQuery(id+"F8.imprint","IMPRINT",EDGE,{"derivedFrom":sQuery(id+"F8.wireOp",EDGE,"E122.MirrorCS")}),1.0]])]});
            var Q120;
            Q120=makeQuery(id+"F8.imprint","IMPRINT",FACE,{"disambiguationData":[TD([[makeQuery(id+"F8.imprint","IMPRINT",EDGE,{"derivedFrom":sQuery(id+"F8.wireOp",EDGE,"E117.MirrorCS")}),1.0]])]});
            var Q121;
            Q121=makeQuery(id+"F8.imprint","IMPRINT",FACE,{"disambiguationData":[TD([[makeQuery(id+"F8.imprint","IMPRINT",EDGE,{"derivedFrom":sQuery(id+"F8.wireOp",EDGE,"E95.MirrorCS")}),1.0]])]});
            var Q122;
            Q122=makeQuery(id+"F8.imprint","IMPRINT",FACE,{"disambiguationData":[TD([[makeQuery(id+"F8.imprint","IMPRINT",EDGE,{"derivedFrom":sQuery(id+"F8.wireOp",EDGE,"E178.MirrorCS")}),1.0]])]});
            var Q123;
            Q123=makeQuery(id+"F8.imprint","IMPRINT",FACE,{"disambiguationData":[TD([[makeQuery(id+"F8.imprint","IMPRINT",EDGE,{"derivedFrom":sQuery(id+"F8.wireOp",EDGE,"E109.MirrorCS")}),1.0]])]});
            var Q124;
            Q124=makeQuery(id+"F8.imprint","IMPRINT",FACE,{"disambiguationData":[TD([[makeQuery(id+"F8.imprint","IMPRINT",EDGE,{"derivedFrom":sQuery(id+"F8.wireOp",EDGE,"E264.MirrorCS")}),1.0]])]});
            var Q125;
            Q125=makeQuery(id+"F8.imprint","IMPRINT",FACE,{"disambiguationData":[TD([[makeQuery(id+"F8.imprint","IMPRINT",EDGE,{"derivedFrom":sQuery(id+"F8.wireOp",EDGE,"E265.MirrorCS")}),1.0]])]});
            var Q126;
            Q126=makeQuery(id+"F8.imprint","IMPRINT",FACE,{"disambiguationData":[TD([[makeQuery(id+"F8.imprint","IMPRINT",EDGE,{"derivedFrom":sQuery(id+"F8.wireOp",EDGE,"E177.MirrorCS")}),1.0]])]});
            var Q127;
            Q127=makeQuery(id+"F8.imprint","IMPRINT",FACE,{"disambiguationData":[TD([[makeQuery(id+"F8.imprint","IMPRINT",EDGE,{"derivedFrom":sQuery(id+"F8.wireOp",EDGE,"E263.MirrorCS")}),1.0]])]});
            var Q128;
            Q128=makeQuery(id+"F8.imprint","IMPRINT",FACE,{"disambiguationData":[TD([[makeQuery(id+"F8.imprint","IMPRINT",EDGE,{"derivedFrom":sQuery(id+"F8.wireOp",EDGE,"E166.MirrorCS")}),1.0]])]});
            var Q129;
            Q129=makeQuery(id+"F8.imprint","IMPRINT",FACE,{"disambiguationData":[TD([[makeQuery(id+"F8.imprint","IMPRINT",EDGE,{"derivedFrom":sQuery(id+"F8.wireOp",EDGE,"E194.MirrorCS")}),1.0]])]});
            var Q130;
            Q130=makeQuery(id+"F8.imprint","IMPRINT",FACE,{"disambiguationData":[TD([[makeQuery(id+"F8.imprint","IMPRINT",EDGE,{"derivedFrom":sQuery(id+"F8.wireOp",EDGE,"E281.MirrorCS")}),1.0]])]});
            var Q131;
            Q131=makeQuery(id+"F8.imprint","IMPRINT",FACE,{"disambiguationData":[TD([[makeQuery(id+"F8.imprint","IMPRINT",EDGE,{"derivedFrom":sQuery(id+"F8.wireOp",EDGE,"E165.MirrorCS")}),1.0]])]});
            var Q132;
            Q132=makeQuery(id+"F8.imprint","IMPRINT",FACE,{"disambiguationData":[TD([[makeQuery(id+"F8.imprint","IMPRINT",EDGE,{"derivedFrom":sQuery(id+"F8.wireOp",EDGE,"E231.MirrorCS")}),1.0]])]});
            var Q133;
            Q133=makeQuery(id+"F8.imprint","IMPRINT",FACE,{"disambiguationData":[TD([[makeQuery(id+"F8.imprint","IMPRINT",EDGE,{"derivedFrom":sQuery(id+"F8.wireOp",EDGE,"E248.MirrorCS")}),1.0]])]});
            var Q134;
            Q134=makeQuery(id+"F8.imprint","IMPRINT",FACE,{"disambiguationData":[TD([[makeQuery(id+"F8.imprint","IMPRINT",EDGE,{"derivedFrom":sQuery(id+"F8.wireOp",EDGE,"E266.MirrorCS")}),1.0]])]});
            var Q135;
            Q135=makeQuery(id+"F8.imprint","IMPRINT",FACE,{"disambiguationData":[TD([[makeQuery(id+"F8.imprint","IMPRINT",EDGE,{"derivedFrom":sQuery(id+"F8.wireOp",EDGE,"E288.MirrorCS")}),1.0]])]});
            var Q136;
            Q136=makeQuery(id+"F8.imprint","IMPRINT",FACE,{"disambiguationData":[TD([[makeQuery(id+"F8.imprint","IMPRINT",EDGE,{"derivedFrom":sQuery(id+"F8.wireOp",EDGE,"E120.MirrorCS")}),1.0]])]});
            var Q137;
            Q137=makeQuery(id+"F8.imprint","IMPRINT",FACE,{"disambiguationData":[TD([[makeQuery(id+"F8.imprint","IMPRINT",EDGE,{"derivedFrom":sQuery(id+"F8.wireOp",EDGE,"E137.MirrorCS")}),1.0]])]});
            var Q138;
            Q138=makeQuery(id+"F8.imprint","IMPRINT",FACE,{"disambiguationData":[TD([[makeQuery(id+"F8.imprint","IMPRINT",EDGE,{"derivedFrom":sQuery(id+"F8.wireOp",EDGE,"E343.MirrorCS")}),1.0]])]});
            var Q139;
            Q139=makeQuery(id+"F8.imprint","IMPRINT",FACE,{"disambiguationData":[TD([[makeQuery(id+"F8.imprint","IMPRINT",EDGE,{"derivedFrom":sQuery(id+"F8.wireOp",EDGE,"E325.MirrorCS")}),1.0]])]});
            var Q140;
            Q140=makeQuery(id+"F8.imprint","IMPRINT",FACE,{"disambiguationData":[TD([[makeQuery(id+"F8.imprint","IMPRINT",EDGE,{"derivedFrom":sQuery(id+"F8.wireOp",EDGE,"E308.MirrorCS")}),1.0]])]});
            var Q141;
            Q141=makeQuery(id+"F8.imprint","IMPRINT",FACE,{"disambiguationData":[TD([[makeQuery(id+"F8.imprint","IMPRINT",EDGE,{"derivedFrom":sQuery(id+"F8.wireOp",EDGE,"E138.MirrorCS")}),1.0]])]});
            var Q142;
            Q142=makeQuery(id+"F8.imprint","IMPRINT",FACE,{"disambiguationData":[TD([[makeQuery(id+"F8.imprint","IMPRINT",EDGE,{"derivedFrom":sQuery(id+"F8.wireOp",EDGE,"E90.MirrorCS")}),1.0]])]});
            extrude(context, id + "F9", {"entities" : qUnion([Q0, Q1, Q2, Q3, Q4, Q5, Q6, Q7, Q8, Q9, Q10, Q11, Q12, Q13, Q14, Q15, Q16, Q17, Q18, Q19, Q20, Q21, Q22, Q23, Q24, Q25, Q26, Q27, Q28, Q29, Q30, Q31, Q32, Q33, Q34, Q35, Q36, Q37, Q38, Q39, Q40, Q41, Q42, Q43, Q44, Q45, Q46, Q47, Q48, Q49, Q50, Q51, Q52, Q53, Q54, Q55, Q56, Q57, Q58, Q59, Q60, Q61, Q62, Q63, Q64, Q65, Q66, Q67, Q68, Q69, Q70, Q71, Q72, Q73, Q74, Q75, Q76, Q77, Q78, Q79, Q80, Q81, Q82, Q83, Q84, Q85, Q86, Q87, Q88, Q89, Q90, Q91, Q92, Q93, Q94, Q95, Q96, Q97, Q98, Q99, Q100, Q101, Q102, Q103, Q104, Q105, Q106, Q107, Q108, Q109, Q110, Q111, Q112, Q113, Q114, Q115, Q116, Q117, Q118, Q119, Q120, Q121, Q122, Q123, Q124, Q125, Q126, Q127, Q128, Q129, Q130, Q131, Q132, Q133, Q134, Q135, Q136, Q137, Q138, Q139, Q140, Q141, Q142]), "operationType" : NewBodyOperationType.REMOVE, "oppositeDirection" : true, "depth" : 200 * mm});
        }
        {
            var Q0;
            {var subQ0=sQuery(id+"F0.wireOp",EDGE,"E13");var subQ1=sQuery(id+"F0.wireOp",EDGE,"E12");Q0=makeQuery(id+"F5.boolean.opBoolean","MERGE",FACE,{"derivedFrom":[makeQuery(id+"F1.opExtrude","CAP_FACE",FACE,{"disambiguationData":[OSD([sQuery(id+"F0.wireOp",EDGE,"E0"),sQuery(id+"F0.wireOp",EDGE,"E1"),sQuery(id+"F0.wireOp",EDGE,"E2.MirrorCS"),sQuery(id+"F0.wireOp",EDGE,"E3.MirrorCS"),sQuery(id+"F0.wireOp",EDGE,"E4"),sQuery(id+"F0.wireOp",EDGE,"E5"),sQuery(id+"F0.wireOp",EDGE,"E6"),sQuery(id+"F0.wireOp",EDGE,"E7"),sQuery(id+"F0.wireOp",EDGE,"E8"),sQuery(id+"F0.wireOp",EDGE,"E9"),sQuery(id+"F0.wireOp",EDGE,"E10"),sQuery(id+"F0.wireOp",EDGE,"E11"),subQ1,subQ0])],"isStart":true}),makeQuery(id+"F5.opExtrude","CAP_FACE",FACE,{"disambiguationData":[OSD([subQ1,sQuery(id+"F4.wireOp",EDGE,"E16")])],"isStart":true}),makeQuery(id+"F5.opExtrude","CAP_FACE",FACE,{"disambiguationData":[OSD([subQ0,sQuery(id+"F4.wireOp",EDGE,"E18")])],"isStart":true})]});}
            var sketch = newSketch(context, id + "F10", { "sketchPlane" : qUnion([Q0])});
            skCircle(sketch, "E474.cCircle", {"center": v(-105.65, 31.9) * mm, "radius": 8.47 * mm, "construction": true});
            skLineSegment(sketch, "E474.0", {"start": v(-90.97, 40.38) * mm, "end": v(-105.65, 14.96) * mm});
            skLineSegment(sketch, "E474.1", {"start": v(-105.65, 14.96) * mm, "end": v(-120.32, 40.38) * mm});
            skLineSegment(sketch, "E474.2", {"start": v(-120.32, 40.38) * mm, "end": v(-90.97, 40.38) * mm});
            skPoint(sketch, "E474.0.midPoint", {"position": v(-98.3, 27.67) * mm});
            skCircle(sketch, "E475.cCircle", {"center": v(-126.02, 20.34) * mm, "radius": 8.74 * mm, "construction": true});
            skLineSegment(sketch, "E475.0", {"start": v(-126.02, 37.81) * mm, "end": v(-110.9, 11.6) * mm});
            skLineSegment(sketch, "E475.1", {"start": v(-110.9, 11.6) * mm, "end": v(-141.16, 11.6) * mm});
            skLineSegment(sketch, "E475.2", {"start": v(-141.16, 11.6) * mm, "end": v(-126.02, 37.81) * mm});
            skPoint(sketch, "E475.0.midPoint", {"position": v(-118.46, 24.7) * mm});
            skCircle(sketch, "E476.cCircle", {"center": v(-143.86, 32.28) * mm, "radius": 6.05 * mm, "construction": true});
            skLineSegment(sketch, "E476.0", {"start": v(-133.39, 38.33) * mm, "end": v(-143.86, 20.2) * mm});
            skLineSegment(sketch, "E476.1", {"start": v(-143.86, 20.2) * mm, "end": v(-154.33, 38.33) * mm});
            skLineSegment(sketch, "E476.2", {"start": v(-154.33, 38.33) * mm, "end": v(-133.39, 38.33) * mm});
            skPoint(sketch, "E476.0.midPoint", {"position": v(-138.62, 29.26) * mm});
            skCircle(sketch, "E477.cCircle", {"center": v(-128.12, 65.69) * mm, "radius": 8.12 * mm, "construction": true});
            skLineSegment(sketch, "E477.0", {"start": v(-114.05, 73.8) * mm, "end": v(-128.12, 49.44) * mm});
            skLineSegment(sketch, "E477.1", {"start": v(-128.12, 49.44) * mm, "end": v(-142.2, 73.8) * mm});
            skLineSegment(sketch, "E477.2", {"start": v(-142.2, 73.8) * mm, "end": v(-114.05, 73.8) * mm});
            skPoint(sketch, "E477.0.midPoint", {"position": v(-121.09, 61.62) * mm});
            skCircle(sketch, "E478.cCircle", {"center": v(-144.86, 53.46) * mm, "radius": 6.25 * mm, "construction": true});
            skLineSegment(sketch, "E478.0", {"start": v(-144.86, 65.96) * mm, "end": v(-134.03, 47.2) * mm});
            skLineSegment(sketch, "E478.1", {"start": v(-134.03, 47.2) * mm, "end": v(-155.7, 47.2) * mm});
            skLineSegment(sketch, "E478.2", {"start": v(-155.7, 47.2) * mm, "end": v(-144.86, 65.96) * mm});
            skPoint(sketch, "E478.0.midPoint", {"position": v(-139.45, 56.58) * mm});
            skCircle(sketch, "E479.cCircle", {"center": v(-105.9, 54.8) * mm, "radius": 7.34 * mm, "construction": true});
            skLineSegment(sketch, "E479.0", {"start": v(-105.9, 69.48) * mm, "end": v(-93.19, 47.47) * mm});
            skLineSegment(sketch, "E479.1", {"start": v(-93.19, 47.47) * mm, "end": v(-118.6, 47.47) * mm});
            skLineSegment(sketch, "E479.2", {"start": v(-118.6, 47.47) * mm, "end": v(-105.9, 69.48) * mm});
            skPoint(sketch, "E479.0.midPoint", {"position": v(-99.54, 58.47) * mm});
            skCircle(sketch, "E480.cCircle", {"center": v(-56.61, 79.1) * mm, "radius": 8.47 * mm, "construction": true});
            skLineSegment(sketch, "E480.0", {"start": v(-41.93, 87.57) * mm, "end": v(-56.61, 62.14) * mm});
            skLineSegment(sketch, "E480.1", {"start": v(-56.61, 62.14) * mm, "end": v(-71.3, 87.57) * mm});
            skLineSegment(sketch, "E480.2", {"start": v(-71.3, 87.57) * mm, "end": v(-41.93, 87.57) * mm});
            skPoint(sketch, "E480.0.midPoint", {"position": v(-49.27, 74.85) * mm});
            skCircle(sketch, "E481.cCircle", {"center": v(-78.05, 67.21) * mm, "radius": 8.74 * mm, "construction": true});
            skLineSegment(sketch, "E481.0", {"start": v(-78.05, 84.69) * mm, "end": v(-62.92, 58.47) * mm});
            skLineSegment(sketch, "E481.1", {"start": v(-62.92, 58.47) * mm, "end": v(-93.19, 58.47) * mm});
            skLineSegment(sketch, "E481.2", {"start": v(-93.19, 58.47) * mm, "end": v(-78.05, 84.69) * mm});
            skPoint(sketch, "E481.0.midPoint", {"position": v(-70.48, 71.58) * mm});
            skCircle(sketch, "E482.cCircle", {"center": v(-97.03, 79.4) * mm, "radius": 7.63 * mm, "construction": true});
            skLineSegment(sketch, "E482.0", {"start": v(-83.8, 87.04) * mm, "end": v(-97.03, 64.14) * mm});
            skLineSegment(sketch, "E482.1", {"start": v(-97.03, 64.14) * mm, "end": v(-110.25, 87.04) * mm});
            skLineSegment(sketch, "E482.2", {"start": v(-110.25, 87.04) * mm, "end": v(-83.8, 87.04) * mm});
            skPoint(sketch, "E482.0.midPoint", {"position": v(-90.41, 75.6) * mm});
            skCircle(sketch, "E483.cCircle", {"center": v(-77.25, 111.17) * mm, "radius": 5.61 * mm, "construction": true});
            skLineSegment(sketch, "E483.0", {"start": v(-67.53, 116.78) * mm, "end": v(-77.25, 99.95) * mm});
            skLineSegment(sketch, "E483.1", {"start": v(-77.25, 99.95) * mm, "end": v(-86.98, 116.78) * mm});
            skLineSegment(sketch, "E483.2", {"start": v(-86.98, 116.78) * mm, "end": v(-67.53, 116.78) * mm});
            skPoint(sketch, "E483.0.midPoint", {"position": v(-72.4, 108.36) * mm});
            skCircle(sketch, "E484.cCircle", {"center": v(-97.38, 100.76) * mm, "radius": 7.55 * mm, "construction": true});
            skLineSegment(sketch, "E484.0", {"start": v(-97.38, 115.86) * mm, "end": v(-84.3, 93.2) * mm});
            skLineSegment(sketch, "E484.1", {"start": v(-84.3, 93.2) * mm, "end": v(-110.47, 93.2) * mm});
            skLineSegment(sketch, "E484.2", {"start": v(-110.47, 93.2) * mm, "end": v(-97.38, 115.86) * mm});
            skPoint(sketch, "E484.0.midPoint", {"position": v(-90.84, 104.53) * mm});
            skCircle(sketch, "E485.cCircle", {"center": v(-56.86, 101.99) * mm, "radius": 7.95 * mm, "construction": true});
            skLineSegment(sketch, "E485.0", {"start": v(-56.86, 117.89) * mm, "end": v(-43.1, 94.04) * mm});
            skLineSegment(sketch, "E485.1", {"start": v(-43.1, 94.04) * mm, "end": v(-70.64, 94.04) * mm});
            skLineSegment(sketch, "E485.2", {"start": v(-70.64, 94.04) * mm, "end": v(-56.86, 117.89) * mm});
            skPoint(sketch, "E485.0.midPoint", {"position": v(-49.98, 105.96) * mm});
            skCircle(sketch, "E486.cCircle", {"center": v(-118.82, 99.37) * mm, "radius": 5.63 * mm, "construction": true});
            skLineSegment(sketch, "E486.0", {"start": v(-109.06, 105) * mm, "end": v(-118.82, 88.1) * mm});
            skLineSegment(sketch, "E486.1", {"start": v(-118.82, 88.1) * mm, "end": v(-128.58, 105) * mm});
            skLineSegment(sketch, "E486.2", {"start": v(-128.58, 105) * mm, "end": v(-109.06, 105) * mm});
            skPoint(sketch, "E486.0.midPoint", {"position": v(-113.94, 96.56) * mm});
            skCircle(sketch, "E487.cCircle", {"center": v(-134.41, 87.8) * mm, "radius": 5.94 * mm, "construction": true});
            skLineSegment(sketch, "E487.0", {"start": v(-134.41, 99.68) * mm, "end": v(-124.12, 81.86) * mm});
            skLineSegment(sketch, "E487.1", {"start": v(-124.12, 81.86) * mm, "end": v(-144.7, 81.86) * mm});
            skLineSegment(sketch, "E487.2", {"start": v(-144.7, 81.86) * mm, "end": v(-134.41, 99.68) * mm});
            skPoint(sketch, "E487.0.midPoint", {"position": v(-129.27, 90.77) * mm});
            skCircle(sketch, "E488.cCircle", {"center": v(-148.1, 99.17) * mm, "radius": 4.36 * mm, "construction": true});
            skLineSegment(sketch, "E488.0", {"start": v(-140.54, 103.53) * mm, "end": v(-148.1, 90.45) * mm});
            skLineSegment(sketch, "E488.1", {"start": v(-148.1, 90.45) * mm, "end": v(-155.64, 103.53) * mm});
            skLineSegment(sketch, "E488.2", {"start": v(-155.64, 103.53) * mm, "end": v(-140.54, 103.53) * mm});
            skPoint(sketch, "E488.0.midPoint", {"position": v(-144.32, 96.99) * mm});
            skCircle(sketch, "E489.cCircle", {"center": v(-135.4, 124.92) * mm, "radius": 3.06 * mm, "construction": true});
            skLineSegment(sketch, "E489.0", {"start": v(-130.1, 127.97) * mm, "end": v(-135.4, 118.8) * mm});
            skLineSegment(sketch, "E489.1", {"start": v(-135.4, 118.8) * mm, "end": v(-140.69, 127.97) * mm});
            skLineSegment(sketch, "E489.2", {"start": v(-140.69, 127.97) * mm, "end": v(-130.1, 127.97) * mm});
            skPoint(sketch, "E489.0.midPoint", {"position": v(-132.74, 123.39) * mm});
            skCircle(sketch, "E490.cCircle", {"center": v(-148.27, 114.99) * mm, "radius": 3.86 * mm, "construction": true});
            skLineSegment(sketch, "E490.0", {"start": v(-148.27, 122.72) * mm, "end": v(-141.58, 111.13) * mm});
            skLineSegment(sketch, "E490.1", {"start": v(-141.58, 111.13) * mm, "end": v(-154.96, 111.13) * mm});
            skLineSegment(sketch, "E490.2", {"start": v(-154.96, 111.13) * mm, "end": v(-148.27, 122.72) * mm});
            skPoint(sketch, "E490.0.midPoint", {"position": v(-144.93, 116.92) * mm});
            skCircle(sketch, "E491.cCircle", {"center": v(-120.24, 116) * mm, "radius": 4.19 * mm, "construction": true});
            skLineSegment(sketch, "E491.0", {"start": v(-120.24, 124.37) * mm, "end": v(-112.99, 111.8) * mm});
            skLineSegment(sketch, "E491.1", {"start": v(-112.99, 111.8) * mm, "end": v(-127.5, 111.8) * mm});
            skLineSegment(sketch, "E491.2", {"start": v(-127.5, 111.8) * mm, "end": v(-120.24, 124.37) * mm});
            skPoint(sketch, "E491.0.midPoint", {"position": v(-116.61, 118.1) * mm});
            skCircle(sketch, "E492.cCircle", {"center": v(-59.2, 270.04) * mm, "radius": 8.47 * mm, "construction": true});
            skLineSegment(sketch, "E492.0", {"start": v(-44.52, 278.51) * mm, "end": v(-59.2, 253.1) * mm});
            skLineSegment(sketch, "E492.1", {"start": v(-59.2, 253.1) * mm, "end": v(-73.88, 278.51) * mm});
            skLineSegment(sketch, "E492.2", {"start": v(-73.88, 278.51) * mm, "end": v(-44.52, 278.51) * mm});
            skPoint(sketch, "E492.0.midPoint", {"position": v(-51.86, 265.8) * mm});
            skCircle(sketch, "E493.cCircle", {"center": v(-79.58, 258.47) * mm, "radius": 8.74 * mm, "construction": true});
            skLineSegment(sketch, "E493.0", {"start": v(-79.58, 275.94) * mm, "end": v(-64.45, 249.73) * mm});
            skLineSegment(sketch, "E493.1", {"start": v(-64.45, 249.73) * mm, "end": v(-94.72, 249.73) * mm});
            skLineSegment(sketch, "E493.2", {"start": v(-94.72, 249.73) * mm, "end": v(-79.58, 275.94) * mm});
            skPoint(sketch, "E493.0.midPoint", {"position": v(-72.01, 262.84) * mm});
            skCircle(sketch, "E494.cCircle", {"center": v(-99.08, 271.23) * mm, "radius": 7.46 * mm, "construction": true});
            skLineSegment(sketch, "E494.0", {"start": v(-86.16, 278.7) * mm, "end": v(-99.08, 256.3) * mm});
            skLineSegment(sketch, "E494.1", {"start": v(-99.08, 256.3) * mm, "end": v(-112, 278.7) * mm});
            skLineSegment(sketch, "E494.2", {"start": v(-112, 278.7) * mm, "end": v(-86.16, 278.7) * mm});
            skPoint(sketch, "E494.0.midPoint", {"position": v(-92.62, 267.5) * mm});
            skCircle(sketch, "E495.cCircle", {"center": v(-79.1, 301.39) * mm, "radius": 7.27 * mm, "construction": true});
            skLineSegment(sketch, "E495.0", {"start": v(-66.51, 308.65) * mm, "end": v(-79.1, 286.85) * mm});
            skLineSegment(sketch, "E495.1", {"start": v(-79.1, 286.85) * mm, "end": v(-91.7, 308.65) * mm});
            skLineSegment(sketch, "E495.2", {"start": v(-91.7, 308.65) * mm, "end": v(-66.51, 308.65) * mm});
            skPoint(sketch, "E495.0.midPoint", {"position": v(-72.8, 297.75) * mm});
            skCircle(sketch, "E496.cCircle", {"center": v(-97.57, 290.08) * mm, "radius": 6.73 * mm, "construction": true});
            skLineSegment(sketch, "E496.0", {"start": v(-97.57, 303.55) * mm, "end": v(-85.9, 283.34) * mm});
            skLineSegment(sketch, "E496.1", {"start": v(-85.9, 283.34) * mm, "end": v(-109.24, 283.34) * mm});
            skLineSegment(sketch, "E496.2", {"start": v(-109.24, 283.34) * mm, "end": v(-97.57, 303.55) * mm});
            skPoint(sketch, "E496.0.midPoint", {"position": v(-91.74, 293.45) * mm});
            skCircle(sketch, "E497.cCircle", {"center": v(-59.45, 292.93) * mm, "radius": 7.95 * mm, "construction": true});
            skLineSegment(sketch, "E497.0", {"start": v(-59.45, 308.84) * mm, "end": v(-45.68, 284.98) * mm});
            skLineSegment(sketch, "E497.1", {"start": v(-45.68, 284.98) * mm, "end": v(-73.23, 284.98) * mm});
            skLineSegment(sketch, "E497.2", {"start": v(-73.23, 284.98) * mm, "end": v(-59.45, 308.84) * mm});
            skPoint(sketch, "E497.0.midPoint", {"position": v(-52.57, 296.91) * mm});
            skCircle(sketch, "E498.cCircle", {"center": v(-109.26, 229) * mm, "radius": 6.72 * mm, "construction": true});
            skLineSegment(sketch, "E498.0", {"start": v(-97.61, 235.73) * mm, "end": v(-109.26, 215.56) * mm});
            skLineSegment(sketch, "E498.1", {"start": v(-109.26, 215.56) * mm, "end": v(-120.9, 235.73) * mm});
            skLineSegment(sketch, "E498.2", {"start": v(-120.9, 235.73) * mm, "end": v(-97.61, 235.73) * mm});
            skPoint(sketch, "E498.0.midPoint", {"position": v(-103.44, 225.65) * mm});
            skCircle(sketch, "E499.cCircle", {"center": v(-127.73, 219.59) * mm, "radius": 6.33 * mm, "construction": true});
            skLineSegment(sketch, "E499.0", {"start": v(-127.73, 232.26) * mm, "end": v(-116.76, 213.25) * mm});
            skLineSegment(sketch, "E499.1", {"start": v(-116.76, 213.25) * mm, "end": v(-138.7, 213.25) * mm});
            skLineSegment(sketch, "E499.2", {"start": v(-138.7, 213.25) * mm, "end": v(-127.73, 232.26) * mm});
            skPoint(sketch, "E499.0.midPoint", {"position": v(-122.24, 222.75) * mm});
            skCircle(sketch, "E500.cCircle", {"center": v(-144.3, 230.56) * mm, "radius": 6.05 * mm, "construction": true});
            skLineSegment(sketch, "E500.0", {"start": v(-133.82, 236.6) * mm, "end": v(-144.3, 218.47) * mm});
            skLineSegment(sketch, "E500.1", {"start": v(-144.3, 218.47) * mm, "end": v(-154.77, 236.6) * mm});
            skLineSegment(sketch, "E500.2", {"start": v(-154.77, 236.6) * mm, "end": v(-133.82, 236.6) * mm});
            skPoint(sketch, "E500.0.midPoint", {"position": v(-139.06, 227.53) * mm});
            skCircle(sketch, "E501.cCircle", {"center": v(-128.44, 258.99) * mm, "radius": 5.98 * mm, "construction": true});
            skLineSegment(sketch, "E501.0", {"start": v(-118.1, 264.96) * mm, "end": v(-128.44, 247.03) * mm});
            skLineSegment(sketch, "E501.1", {"start": v(-128.44, 247.03) * mm, "end": v(-138.8, 264.96) * mm});
            skLineSegment(sketch, "E501.2", {"start": v(-138.8, 264.96) * mm, "end": v(-118.1, 264.96) * mm});
            skPoint(sketch, "E501.0.midPoint", {"position": v(-123.27, 256) * mm});
            skCircle(sketch, "E502.cCircle", {"center": v(-145.55, 247.67) * mm, "radius": 5.22 * mm, "construction": true});
            skLineSegment(sketch, "E502.0", {"start": v(-145.55, 258.1) * mm, "end": v(-136.52, 242.45) * mm});
            skLineSegment(sketch, "E502.1", {"start": v(-136.52, 242.45) * mm, "end": v(-154.59, 242.45) * mm});
            skLineSegment(sketch, "E502.2", {"start": v(-154.59, 242.45) * mm, "end": v(-145.55, 258.1) * mm});
            skPoint(sketch, "E502.0.midPoint", {"position": v(-141.04, 250.27) * mm});
            skCircle(sketch, "E503.cCircle", {"center": v(-110.77, 249.37) * mm, "radius": 6.04 * mm, "construction": true});
            skLineSegment(sketch, "E503.0", {"start": v(-110.77, 261.45) * mm, "end": v(-100.3, 243.32) * mm});
            skLineSegment(sketch, "E503.1", {"start": v(-100.3, 243.32) * mm, "end": v(-121.23, 243.32) * mm});
            skLineSegment(sketch, "E503.2", {"start": v(-121.23, 243.32) * mm, "end": v(-110.77, 261.45) * mm});
            skPoint(sketch, "E503.0.midPoint", {"position": v(-105.53, 252.39) * mm});
            skCircle(sketch, "E504.cCircle", {"center": v(-127.4, 43.5) * mm, "radius": 3.14 * mm, "construction": true});
            skLineSegment(sketch, "E504.0", {"start": v(-124.26, 45.31) * mm, "end": v(-124.26, 41.69) * mm});
            skLineSegment(sketch, "E504.1", {"start": v(-124.26, 41.69) * mm, "end": v(-127.4, 39.88) * mm});
            skLineSegment(sketch, "E504.2", {"start": v(-127.4, 39.88) * mm, "end": v(-130.54, 41.69) * mm});
            skLineSegment(sketch, "E504.3", {"start": v(-130.54, 41.69) * mm, "end": v(-130.54, 45.31) * mm});
            skLineSegment(sketch, "E504.4", {"start": v(-130.54, 45.31) * mm, "end": v(-127.4, 47.12) * mm});
            skLineSegment(sketch, "E504.5", {"start": v(-127.4, 47.12) * mm, "end": v(-124.26, 45.31) * mm});
            skPoint(sketch, "E504.0.midPoint", {"position": v(-124.26, 43.5) * mm});
            skCircle(sketch, "E505.cCircle", {"center": v(-77.84, 92.36) * mm, "radius": 3.14 * mm, "construction": true});
            skLineSegment(sketch, "E505.0", {"start": v(-74.7, 94.18) * mm, "end": v(-74.7, 90.55) * mm});
            skLineSegment(sketch, "E505.1", {"start": v(-74.7, 90.55) * mm, "end": v(-77.84, 88.74) * mm});
            skLineSegment(sketch, "E505.2", {"start": v(-77.84, 88.74) * mm, "end": v(-80.98, 90.55) * mm});
            skLineSegment(sketch, "E505.3", {"start": v(-80.98, 90.55) * mm, "end": v(-80.98, 94.18) * mm});
            skLineSegment(sketch, "E505.4", {"start": v(-80.98, 94.18) * mm, "end": v(-77.84, 95.99) * mm});
            skLineSegment(sketch, "E505.5", {"start": v(-77.84, 95.99) * mm, "end": v(-74.7, 94.18) * mm});
            skPoint(sketch, "E505.0.midPoint", {"position": v(-74.7, 92.36) * mm});
            skCircle(sketch, "E506.cCircle", {"center": v(-135.02, 108.35) * mm, "radius": 3.82 * mm, "construction": true});
            skLineSegment(sketch, "E506.0", {"start": v(-131.2, 110.56) * mm, "end": v(-131.2, 106.15) * mm});
            skLineSegment(sketch, "E506.1", {"start": v(-131.2, 106.15) * mm, "end": v(-135.02, 103.94) * mm});
            skLineSegment(sketch, "E506.2", {"start": v(-135.02, 103.94) * mm, "end": v(-138.84, 106.15) * mm});
            skLineSegment(sketch, "E506.3", {"start": v(-138.84, 106.15) * mm, "end": v(-138.84, 110.56) * mm});
            skLineSegment(sketch, "E506.4", {"start": v(-138.84, 110.56) * mm, "end": v(-135.02, 112.76) * mm});
            skLineSegment(sketch, "E506.5", {"start": v(-135.02, 112.76) * mm, "end": v(-131.2, 110.56) * mm});
            skPoint(sketch, "E506.0.midPoint", {"position": v(-131.2, 108.35) * mm});
            skCircle(sketch, "E507.cCircle", {"center": v(-127.72, 239.95) * mm, "radius": 3.14 * mm, "construction": true});
            skLineSegment(sketch, "E507.0", {"start": v(-124.59, 241.76) * mm, "end": v(-124.59, 238.13) * mm});
            skLineSegment(sketch, "E507.1", {"start": v(-124.59, 238.13) * mm, "end": v(-127.72, 236.32) * mm});
            skLineSegment(sketch, "E507.2", {"start": v(-127.72, 236.32) * mm, "end": v(-130.86, 238.13) * mm});
            skLineSegment(sketch, "E507.3", {"start": v(-130.86, 238.13) * mm, "end": v(-130.86, 241.76) * mm});
            skLineSegment(sketch, "E507.4", {"start": v(-130.86, 241.76) * mm, "end": v(-127.72, 243.57) * mm});
            skLineSegment(sketch, "E507.5", {"start": v(-127.72, 243.57) * mm, "end": v(-124.59, 241.76) * mm});
            skPoint(sketch, "E507.0.midPoint", {"position": v(-124.59, 239.95) * mm});
            skCircle(sketch, "E508.cCircle", {"center": v(-79.94, 281.42) * mm, "radius": 3.14 * mm, "construction": true});
            skLineSegment(sketch, "E508.0", {"start": v(-76.8, 283.23) * mm, "end": v(-76.8, 279.61) * mm});
            skLineSegment(sketch, "E508.1", {"start": v(-76.8, 279.61) * mm, "end": v(-79.94, 277.8) * mm});
            skLineSegment(sketch, "E508.2", {"start": v(-79.94, 277.8) * mm, "end": v(-83.08, 279.61) * mm});
            skLineSegment(sketch, "E508.3", {"start": v(-83.08, 279.61) * mm, "end": v(-83.08, 283.23) * mm});
            skLineSegment(sketch, "E508.4", {"start": v(-83.08, 283.23) * mm, "end": v(-79.94, 285.05) * mm});
            skLineSegment(sketch, "E508.5", {"start": v(-79.94, 285.05) * mm, "end": v(-76.8, 283.23) * mm});
            skPoint(sketch, "E508.0.midPoint", {"position": v(-76.8, 281.42) * mm});
            skCircle(sketch, "E509.cCircle", {"center": v(-54.56, 208.37) * mm, "radius": 6.34 * mm, "construction": true});
            skLineSegment(sketch, "E509.0", {"start": v(-43.58, 214.71) * mm, "end": v(-54.56, 195.7) * mm});
            skLineSegment(sketch, "E509.1", {"start": v(-54.56, 195.7) * mm, "end": v(-65.53, 214.71) * mm});
            skLineSegment(sketch, "E509.2", {"start": v(-65.53, 214.71) * mm, "end": v(-43.58, 214.71) * mm});
            skPoint(sketch, "E509.0.midPoint", {"position": v(-49.07, 205.2) * mm});
            skCircle(sketch, "E510.cCircle", {"center": v(-70.74, 238.04) * mm, "radius": 7.27 * mm, "construction": true});
            skLineSegment(sketch, "E510.0", {"start": v(-58.16, 245.3) * mm, "end": v(-70.74, 223.5) * mm});
            skLineSegment(sketch, "E510.1", {"start": v(-70.74, 223.5) * mm, "end": v(-83.33, 245.3) * mm});
            skLineSegment(sketch, "E510.2", {"start": v(-83.33, 245.3) * mm, "end": v(-58.16, 245.3) * mm});
            skPoint(sketch, "E510.0.midPoint", {"position": v(-64.45, 234.4) * mm});
            skCircle(sketch, "E511.cCircle", {"center": v(-89.22, 226.73) * mm, "radius": 6.73 * mm, "construction": true});
            skLineSegment(sketch, "E511.0", {"start": v(-89.22, 240.2) * mm, "end": v(-77.55, 220) * mm});
            skLineSegment(sketch, "E511.1", {"start": v(-77.55, 220) * mm, "end": v(-100.88, 220) * mm});
            skLineSegment(sketch, "E511.2", {"start": v(-100.88, 220) * mm, "end": v(-89.22, 240.2) * mm});
            skPoint(sketch, "E511.0.midPoint", {"position": v(-83.38, 230.1) * mm});
            skCircle(sketch, "E512.cCircle", {"center": v(-54.3, 230.51) * mm, "radius": 6.48 * mm, "construction": true});
            skLineSegment(sketch, "E512.0", {"start": v(-54.3, 243.48) * mm, "end": v(-43.08, 224.03) * mm});
            skLineSegment(sketch, "E512.1", {"start": v(-43.08, 224.03) * mm, "end": v(-65.53, 224.03) * mm});
            skLineSegment(sketch, "E512.2", {"start": v(-65.53, 224.03) * mm, "end": v(-54.3, 243.48) * mm});
            skPoint(sketch, "E512.0.midPoint", {"position": v(-48.69, 233.76) * mm});
            skCircle(sketch, "E513.cCircle", {"center": v(-71.58, 218.08) * mm, "radius": 3.14 * mm, "construction": true});
            skLineSegment(sketch, "E513.0", {"start": v(-68.44, 219.89) * mm, "end": v(-68.44, 216.26) * mm});
            skLineSegment(sketch, "E513.1", {"start": v(-68.44, 216.26) * mm, "end": v(-71.58, 214.45) * mm});
            skLineSegment(sketch, "E513.2", {"start": v(-71.58, 214.45) * mm, "end": v(-74.72, 216.26) * mm});
            skLineSegment(sketch, "E513.3", {"start": v(-74.72, 216.26) * mm, "end": v(-74.72, 219.89) * mm});
            skLineSegment(sketch, "E513.4", {"start": v(-74.72, 219.89) * mm, "end": v(-71.58, 221.7) * mm});
            skLineSegment(sketch, "E513.5", {"start": v(-71.58, 221.7) * mm, "end": v(-68.44, 219.89) * mm});
            skPoint(sketch, "E513.0.midPoint", {"position": v(-68.44, 218.08) * mm});
            skCircle(sketch, "E514.cCircle", {"center": v(-146.84, 173.22) * mm, "radius": 4.24 * mm, "construction": true});
            skLineSegment(sketch, "E514.0", {"start": v(-139.5, 177.46) * mm, "end": v(-146.84, 164.75) * mm});
            skLineSegment(sketch, "E514.1", {"start": v(-146.84, 164.75) * mm, "end": v(-154.18, 177.46) * mm});
            skLineSegment(sketch, "E514.2", {"start": v(-154.18, 177.46) * mm, "end": v(-139.5, 177.46) * mm});
            skPoint(sketch, "E514.0.midPoint", {"position": v(-143.17, 171.1) * mm});
            skCircle(sketch, "E515.cCircle", {"center": v(-133.46, 201.43) * mm, "radius": 7.27 * mm, "construction": true});
            skLineSegment(sketch, "E515.0", {"start": v(-120.87, 208.7) * mm, "end": v(-133.46, 186.9) * mm});
            skLineSegment(sketch, "E515.1", {"start": v(-133.46, 186.9) * mm, "end": v(-146.05, 208.7) * mm});
            skLineSegment(sketch, "E515.2", {"start": v(-146.05, 208.7) * mm, "end": v(-120.87, 208.7) * mm});
            skPoint(sketch, "E515.0.midPoint", {"position": v(-127.16, 197.8) * mm});
            skCircle(sketch, "E516.cCircle", {"center": v(-147.5, 189.48) * mm, "radius": 4.45 * mm, "construction": true});
            skLineSegment(sketch, "E516.0", {"start": v(-147.5, 198.39) * mm, "end": v(-139.8, 185.03) * mm});
            skLineSegment(sketch, "E516.1", {"start": v(-139.8, 185.03) * mm, "end": v(-155.22, 185.03) * mm});
            skLineSegment(sketch, "E516.2", {"start": v(-155.22, 185.03) * mm, "end": v(-147.5, 198.39) * mm});
            skPoint(sketch, "E516.0.midPoint", {"position": v(-143.65, 191.7) * mm});
            skCircle(sketch, "E517.cCircle", {"center": v(-134.3, 181.46) * mm, "radius": 3.14 * mm, "construction": true});
            skLineSegment(sketch, "E517.0", {"start": v(-131.16, 183.28) * mm, "end": v(-131.16, 179.65) * mm});
            skLineSegment(sketch, "E517.1", {"start": v(-131.16, 179.65) * mm, "end": v(-134.3, 177.84) * mm});
            skLineSegment(sketch, "E517.2", {"start": v(-134.3, 177.84) * mm, "end": v(-137.43, 179.65) * mm});
            skLineSegment(sketch, "E517.3", {"start": v(-137.43, 179.65) * mm, "end": v(-137.43, 183.28) * mm});
            skLineSegment(sketch, "E517.4", {"start": v(-137.43, 183.28) * mm, "end": v(-134.3, 185.09) * mm});
            skLineSegment(sketch, "E517.5", {"start": v(-134.3, 185.09) * mm, "end": v(-131.16, 183.28) * mm});
            skCircle(sketch, "E518.cCircle", {"center": v(-151.17, 141.9) * mm, "radius": 2.6 * mm, "construction": true});
            skLineSegment(sketch, "E518.0", {"start": v(-146.67, 144.49) * mm, "end": v(-151.17, 136.7) * mm});
            skLineSegment(sketch, "E518.1", {"start": v(-151.17, 136.7) * mm, "end": v(-155.66, 144.49) * mm});
            skLineSegment(sketch, "E518.2", {"start": v(-155.66, 144.49) * mm, "end": v(-146.67, 144.49) * mm});
            skPoint(sketch, "E518.0.midPoint", {"position": v(-148.92, 140.6) * mm});
            skCircle(sketch, "E519.cCircle", {"center": v(-151.35, 155.17) * mm, "radius": 2.76 * mm, "construction": true});
            skLineSegment(sketch, "E519.0", {"start": v(-151.35, 160.7) * mm, "end": v(-146.57, 152.41) * mm});
            skLineSegment(sketch, "E519.1", {"start": v(-146.57, 152.41) * mm, "end": v(-156.13, 152.41) * mm});
            skLineSegment(sketch, "E519.2", {"start": v(-156.13, 152.41) * mm, "end": v(-151.35, 160.7) * mm});
            skPoint(sketch, "E519.0.midPoint", {"position": v(-148.96, 156.55) * mm});
            skCircle(sketch, "E520.cCircle", {"center": v(-140.98, 148.68) * mm, "radius": 3.14 * mm, "construction": true});
            skLineSegment(sketch, "E520.0", {"start": v(-137.84, 150.5) * mm, "end": v(-137.84, 146.87) * mm});
            skLineSegment(sketch, "E520.1", {"start": v(-137.84, 146.87) * mm, "end": v(-140.98, 145.06) * mm});
            skLineSegment(sketch, "E520.2", {"start": v(-140.98, 145.06) * mm, "end": v(-144.12, 146.87) * mm});
            skLineSegment(sketch, "E520.3", {"start": v(-144.12, 146.87) * mm, "end": v(-144.12, 150.5) * mm});
            skLineSegment(sketch, "E520.4", {"start": v(-144.12, 150.5) * mm, "end": v(-140.98, 152.3) * mm});
            skLineSegment(sketch, "E520.5", {"start": v(-140.98, 152.3) * mm, "end": v(-137.84, 150.5) * mm});
            skPoint(sketch, "E520.0.midPoint", {"position": v(-137.84, 148.68) * mm});
            skCircle(sketch, "E521.cCircle", {"center": v(-140.98, 160.26) * mm, "radius": 2.37 * mm, "construction": true});
            skLineSegment(sketch, "E521.0", {"start": v(-136.88, 162.63) * mm, "end": v(-140.98, 155.52) * mm});
            skLineSegment(sketch, "E521.1", {"start": v(-140.98, 155.52) * mm, "end": v(-145.09, 162.63) * mm});
            skLineSegment(sketch, "E521.2", {"start": v(-145.09, 162.63) * mm, "end": v(-136.88, 162.63) * mm});
            skPoint(sketch, "E521.0.midPoint", {"position": v(-138.93, 159.08) * mm});
            skCircle(sketch, "E522.cCircle", {"center": v(-141.13, 135.58) * mm, "radius": 2.81 * mm, "construction": true});
            skLineSegment(sketch, "E522.0", {"start": v(-141.13, 141.2) * mm, "end": v(-136.26, 132.77) * mm});
            skLineSegment(sketch, "E522.1", {"start": v(-136.26, 132.77) * mm, "end": v(-146, 132.77) * mm});
            skLineSegment(sketch, "E522.2", {"start": v(-146, 132.77) * mm, "end": v(-141.13, 141.2) * mm});
            skPoint(sketch, "E522.0.midPoint", {"position": v(-138.7, 136.98) * mm});
            skCircle(sketch, "E523.cCircle", {"center": v(-91.44, 212) * mm, "radius": 4 * mm, "construction": true});
            skLineSegment(sketch, "E523.0", {"start": v(-84.5, 216.02) * mm, "end": v(-91.44, 203.99) * mm});
            skLineSegment(sketch, "E523.1", {"start": v(-91.44, 203.99) * mm, "end": v(-98.38, 216.02) * mm});
            skLineSegment(sketch, "E523.2", {"start": v(-98.38, 216.02) * mm, "end": v(-84.5, 216.02) * mm});
            skPoint(sketch, "E523.0.midPoint", {"position": v(-87.97, 210) * mm});
            skCircle(sketch, "E524.cCircle", {"center": v(-109.01, 206.07) * mm, "radius": 2.55 * mm, "construction": true});
            skLineSegment(sketch, "E524.0", {"start": v(-109.01, 211.18) * mm, "end": v(-104.59, 203.52) * mm});
            skLineSegment(sketch, "E524.1", {"start": v(-104.59, 203.52) * mm, "end": v(-113.44, 203.52) * mm});
            skLineSegment(sketch, "E524.2", {"start": v(-113.44, 203.52) * mm, "end": v(-109.01, 211.18) * mm});
            skPoint(sketch, "E524.0.midPoint", {"position": v(-106.8, 207.35) * mm});
            skCircle(sketch, "E525.cCircle", {"center": v(-70.78, 204.65) * mm, "radius": 2.38 * mm, "construction": true});
            skLineSegment(sketch, "E525.0", {"start": v(-70.78, 209.4) * mm, "end": v(-66.67, 202.27) * mm});
            skLineSegment(sketch, "E525.1", {"start": v(-66.67, 202.27) * mm, "end": v(-74.9, 202.27) * mm});
            skLineSegment(sketch, "E525.2", {"start": v(-74.9, 202.27) * mm, "end": v(-70.78, 209.4) * mm});
            skPoint(sketch, "E525.0.midPoint", {"position": v(-68.72, 205.83) * mm});
            skCircle(sketch, "E526.cCircle", {"center": v(-14.51, 87.57) * mm, "radius": 7.27 * mm, "construction": true});
            skLineSegment(sketch, "E526.0", {"start": v(-1.92, 94.84) * mm, "end": v(-14.51, 73.04) * mm});
            skLineSegment(sketch, "E526.1", {"start": v(-14.51, 73.04) * mm, "end": v(-27.1, 94.84) * mm});
            skLineSegment(sketch, "E526.2", {"start": v(-27.1, 94.84) * mm, "end": v(-1.92, 94.84) * mm});
            skPoint(sketch, "E526.0.midPoint", {"position": v(-8.22, 83.94) * mm});
            skCircle(sketch, "E527.cCircle", {"center": v(-32.98, 76.26) * mm, "radius": 6.73 * mm, "construction": true});
            skLineSegment(sketch, "E527.0", {"start": v(-32.98, 89.73) * mm, "end": v(-21.32, 69.53) * mm});
            skLineSegment(sketch, "E527.1", {"start": v(-21.32, 69.53) * mm, "end": v(-44.65, 69.53) * mm});
            skLineSegment(sketch, "E527.2", {"start": v(-44.65, 69.53) * mm, "end": v(-32.98, 89.73) * mm});
            skPoint(sketch, "E527.0.midPoint", {"position": v(-27.15, 79.63) * mm});
            skCircle(sketch, "E528.cCircle", {"center": v(-15.38, 66.59) * mm, "radius": 2.77 * mm, "construction": true});
            skLineSegment(sketch, "E528.0", {"start": v(-12.28, 67.38) * mm, "end": v(-13.15, 64.3) * mm});
            skLineSegment(sketch, "E528.1", {"start": v(-13.15, 64.3) * mm, "end": v(-16.25, 63.5) * mm});
            skLineSegment(sketch, "E528.2", {"start": v(-16.25, 63.5) * mm, "end": v(-18.48, 65.8) * mm});
            skLineSegment(sketch, "E528.3", {"start": v(-18.48, 65.8) * mm, "end": v(-17.62, 68.88) * mm});
            skLineSegment(sketch, "E528.4", {"start": v(-17.62, 68.88) * mm, "end": v(-14.52, 69.67) * mm});
            skLineSegment(sketch, "E528.5", {"start": v(-14.52, 69.67) * mm, "end": v(-12.28, 67.38) * mm});
            skCircle(sketch, "E529.cCircle", {"center": v(-27.06, 112) * mm, "radius": 5.87 * mm, "construction": true});
            skLineSegment(sketch, "E529.0", {"start": v(-27.06, 123.75) * mm, "end": v(-16.88, 106.12) * mm});
            skLineSegment(sketch, "E529.1", {"start": v(-16.88, 106.12) * mm, "end": v(-37.23, 106.12) * mm});
            skLineSegment(sketch, "E529.2", {"start": v(-37.23, 106.12) * mm, "end": v(-27.06, 123.75) * mm});
            skPoint(sketch, "E529.0.midPoint", {"position": v(-21.97, 114.93) * mm});
            skCircle(sketch, "E530.cCircle", {"center": v(-43.52, 124.8) * mm, "radius": 5.7 * mm, "construction": true});
            skLineSegment(sketch, "E530.0", {"start": v(-33.66, 130.5) * mm, "end": v(-43.52, 113.4) * mm});
            skLineSegment(sketch, "E530.1", {"start": v(-43.52, 113.4) * mm, "end": v(-53.4, 130.5) * mm});
            skLineSegment(sketch, "E530.2", {"start": v(-53.4, 130.5) * mm, "end": v(-33.66, 130.5) * mm});
            skPoint(sketch, "E530.0.midPoint", {"position": v(-38.6, 121.96) * mm});
            skCircle(sketch, "E531.cCircle", {"center": v(-44.79, 142) * mm, "radius": 4.33 * mm, "construction": true});
            skLineSegment(sketch, "E531.0", {"start": v(-44.79, 150.67) * mm, "end": v(-37.28, 137.66) * mm});
            skLineSegment(sketch, "E531.1", {"start": v(-37.28, 137.66) * mm, "end": v(-52.3, 137.66) * mm});
            skLineSegment(sketch, "E531.2", {"start": v(-52.3, 137.66) * mm, "end": v(-44.79, 150.67) * mm});
            skPoint(sketch, "E531.0.midPoint", {"position": v(-41.04, 144.17) * mm});
            skCircle(sketch, "E532.cCircle", {"center": v(-47.5, 170.7) * mm, "radius": 2.7 * mm, "construction": true});
            skLineSegment(sketch, "E532.0", {"start": v(-42.83, 173.4) * mm, "end": v(-47.5, 165.31) * mm});
            skLineSegment(sketch, "E532.1", {"start": v(-47.5, 165.31) * mm, "end": v(-52.17, 173.4) * mm});
            skLineSegment(sketch, "E532.2", {"start": v(-52.17, 173.4) * mm, "end": v(-42.83, 173.4) * mm});
            skPoint(sketch, "E532.0.midPoint", {"position": v(-45.17, 169.35) * mm});
            skCircle(sketch, "E533.cCircle", {"center": v(-48.77, 187.9) * mm, "radius": 3.26 * mm, "construction": true});
            skLineSegment(sketch, "E533.0", {"start": v(-48.77, 194.42) * mm, "end": v(-43.12, 184.64) * mm});
            skLineSegment(sketch, "E533.1", {"start": v(-43.12, 184.64) * mm, "end": v(-54.4, 184.64) * mm});
            skLineSegment(sketch, "E533.2", {"start": v(-54.4, 184.64) * mm, "end": v(-48.77, 194.42) * mm});
            skPoint(sketch, "E533.0.midPoint", {"position": v(-45.94, 189.53) * mm});
            skCircle(sketch, "E534.cCircle", {"center": v(-150.46, 69.02) * mm, "radius": 2.92 * mm, "construction": true});
            skLineSegment(sketch, "E534.0", {"start": v(-145.4, 71.94) * mm, "end": v(-150.46, 63.18) * mm});
            skLineSegment(sketch, "E534.1", {"start": v(-150.46, 63.18) * mm, "end": v(-155.51, 71.94) * mm});
            skLineSegment(sketch, "E534.2", {"start": v(-155.51, 71.94) * mm, "end": v(-145.4, 71.94) * mm});
            skPoint(sketch, "E534.0.midPoint", {"position": v(-147.93, 67.56) * mm});
            skCircle(sketch, "E535.cCircle", {"center": v(-151.79, 80.88) * mm, "radius": 2.24 * mm, "construction": true});
            skLineSegment(sketch, "E535.0", {"start": v(-151.79, 85.35) * mm, "end": v(-147.91, 78.64) * mm});
            skLineSegment(sketch, "E535.1", {"start": v(-147.91, 78.64) * mm, "end": v(-155.66, 78.64) * mm});
            skLineSegment(sketch, "E535.2", {"start": v(-155.66, 78.64) * mm, "end": v(-151.79, 85.35) * mm});
            skPoint(sketch, "E535.0.midPoint", {"position": v(-149.85, 82) * mm});
            skCircle(sketch, "E536.cCircle", {"center": v(-117.55, 80.72) * mm, "radius": 3.14 * mm, "construction": true});
            skLineSegment(sketch, "E536.0", {"start": v(-114.4, 82.54) * mm, "end": v(-114.4, 78.91) * mm});
            skLineSegment(sketch, "E536.1", {"start": v(-114.4, 78.91) * mm, "end": v(-117.55, 77.1) * mm});
            skLineSegment(sketch, "E536.2", {"start": v(-117.55, 77.1) * mm, "end": v(-120.69, 78.91) * mm});
            skLineSegment(sketch, "E536.3", {"start": v(-120.69, 78.91) * mm, "end": v(-120.69, 82.54) * mm});
            skLineSegment(sketch, "E536.4", {"start": v(-120.69, 82.54) * mm, "end": v(-117.55, 84.35) * mm});
            skLineSegment(sketch, "E536.5", {"start": v(-117.55, 84.35) * mm, "end": v(-114.4, 82.54) * mm});
            skCircle(sketch, "E537.cCircle", {"center": v(-150.3, 13.28) * mm, "radius": 3.14 * mm, "construction": true});
            skLineSegment(sketch, "E537.0", {"start": v(-147.16, 15.09) * mm, "end": v(-147.16, 11.47) * mm});
            skLineSegment(sketch, "E537.1", {"start": v(-147.16, 11.47) * mm, "end": v(-150.3, 9.65) * mm});
            skLineSegment(sketch, "E537.2", {"start": v(-150.3, 9.65) * mm, "end": v(-153.44, 11.47) * mm});
            skLineSegment(sketch, "E537.3", {"start": v(-153.44, 11.47) * mm, "end": v(-153.44, 15.09) * mm});
            skLineSegment(sketch, "E537.4", {"start": v(-153.44, 15.09) * mm, "end": v(-150.3, 16.9) * mm});
            skLineSegment(sketch, "E537.5", {"start": v(-150.3, 16.9) * mm, "end": v(-147.16, 15.09) * mm});
            skCircle(sketch, "E538.cCircle", {"center": v(-80.31, 47.96) * mm, "radius": 3.14 * mm, "construction": true});
            skLineSegment(sketch, "E538.0", {"start": v(-77.17, 49.77) * mm, "end": v(-77.17, 46.15) * mm});
            skLineSegment(sketch, "E538.1", {"start": v(-77.17, 46.15) * mm, "end": v(-80.31, 44.34) * mm});
            skLineSegment(sketch, "E538.2", {"start": v(-80.31, 44.34) * mm, "end": v(-83.45, 46.15) * mm});
            skLineSegment(sketch, "E538.3", {"start": v(-83.45, 46.15) * mm, "end": v(-83.45, 49.77) * mm});
            skLineSegment(sketch, "E538.4", {"start": v(-83.45, 49.77) * mm, "end": v(-80.31, 51.58) * mm});
            skLineSegment(sketch, "E538.5", {"start": v(-80.31, 51.58) * mm, "end": v(-77.17, 49.77) * mm});
            skCircle(sketch, "E539.cCircle", {"center": v(-152.42, 212.92) * mm, "radius": 3.14 * mm, "construction": true});
            skLineSegment(sketch, "E539.0", {"start": v(-149.28, 214.73) * mm, "end": v(-149.28, 211.1) * mm});
            skLineSegment(sketch, "E539.1", {"start": v(-149.28, 211.1) * mm, "end": v(-152.42, 209.3) * mm});
            skLineSegment(sketch, "E539.2", {"start": v(-152.42, 209.3) * mm, "end": v(-155.56, 211.1) * mm});
            skLineSegment(sketch, "E539.3", {"start": v(-155.56, 211.1) * mm, "end": v(-155.56, 214.73) * mm});
            skLineSegment(sketch, "E539.4", {"start": v(-155.56, 214.73) * mm, "end": v(-152.42, 216.54) * mm});
            skLineSegment(sketch, "E539.5", {"start": v(-152.42, 216.54) * mm, "end": v(-149.28, 214.73) * mm});
            skCircle(sketch, "E540.cCircle", {"center": v(-47.62, 251.68) * mm, "radius": 3.14 * mm, "construction": true});
            skLineSegment(sketch, "E540.0", {"start": v(-44.48, 253.5) * mm, "end": v(-44.48, 249.87) * mm});
            skLineSegment(sketch, "E540.1", {"start": v(-44.48, 249.87) * mm, "end": v(-47.62, 248.06) * mm});
            skLineSegment(sketch, "E540.2", {"start": v(-47.62, 248.06) * mm, "end": v(-50.76, 249.87) * mm});
            skLineSegment(sketch, "E540.3", {"start": v(-50.76, 249.87) * mm, "end": v(-50.76, 253.5) * mm});
            skLineSegment(sketch, "E540.4", {"start": v(-50.76, 253.5) * mm, "end": v(-47.62, 255.3) * mm});
            skLineSegment(sketch, "E540.5", {"start": v(-47.62, 255.3) * mm, "end": v(-44.48, 253.5) * mm});
            skCircle(sketch, "E541.cCircle", {"center": v(-121.87, 274.77) * mm, "radius": 3.14 * mm, "construction": true});
            skLineSegment(sketch, "E541.0", {"start": v(-118.73, 276.58) * mm, "end": v(-118.73, 272.96) * mm});
            skLineSegment(sketch, "E541.1", {"start": v(-118.73, 272.96) * mm, "end": v(-121.87, 271.15) * mm});
            skLineSegment(sketch, "E541.2", {"start": v(-121.87, 271.15) * mm, "end": v(-125.01, 272.96) * mm});
            skLineSegment(sketch, "E541.3", {"start": v(-125.01, 272.96) * mm, "end": v(-125.01, 276.58) * mm});
            skLineSegment(sketch, "E541.4", {"start": v(-125.01, 276.58) * mm, "end": v(-121.87, 278.4) * mm});
            skLineSegment(sketch, "E541.5", {"start": v(-121.87, 278.4) * mm, "end": v(-118.73, 276.58) * mm});
            skCircle(sketch, "E542.cCircle", {"center": v(-47.4, 304.5) * mm, "radius": 3.14 * mm, "construction": true});
            skLineSegment(sketch, "E542.0", {"start": v(-44.26, 306.31) * mm, "end": v(-44.26, 302.69) * mm});
            skLineSegment(sketch, "E542.1", {"start": v(-44.26, 302.69) * mm, "end": v(-47.4, 300.88) * mm});
            skLineSegment(sketch, "E542.2", {"start": v(-47.4, 300.88) * mm, "end": v(-50.53, 302.69) * mm});
            skLineSegment(sketch, "E542.3", {"start": v(-50.53, 302.69) * mm, "end": v(-50.53, 306.31) * mm});
            skLineSegment(sketch, "E542.4", {"start": v(-50.53, 306.31) * mm, "end": v(-47.4, 308.12) * mm});
            skLineSegment(sketch, "E542.5", {"start": v(-47.4, 308.12) * mm, "end": v(-44.26, 306.31) * mm});
            skLineSegment(sketch, "E543.MirrorCS", {"start": v(77.87, 283.23) * mm, "end": v(77.87, 279.61) * mm});
            skLineSegment(sketch, "E544.MirrorCS", {"start": v(84.14, 279.61) * mm, "end": v(84.14, 283.23) * mm});
            skLineSegment(sketch, "E545.MirrorCS", {"start": v(81, 277.8) * mm, "end": v(84.14, 279.61) * mm});
            skLineSegment(sketch, "E546.MirrorCS", {"start": v(84.14, 283.23) * mm, "end": v(81, 285.05) * mm});
            skLineSegment(sketch, "E547.MirrorCS", {"start": v(145.19, 146.87) * mm, "end": v(145.19, 150.5) * mm});
            skLineSegment(sketch, "E548.MirrorCS", {"start": v(137.94, 162.63) * mm, "end": v(142.05, 155.52) * mm});
            skLineSegment(sketch, "E549.MirrorCS", {"start": v(138.91, 146.87) * mm, "end": v(142.05, 145.06) * mm});
            skLineSegment(sketch, "E550.MirrorCS", {"start": v(138.91, 150.5) * mm, "end": v(138.91, 146.87) * mm});
            skLineSegment(sketch, "E551.MirrorCS", {"start": v(142.05, 145.06) * mm, "end": v(145.19, 146.87) * mm});
            skLineSegment(sketch, "E552.MirrorCS", {"start": v(77.87, 279.61) * mm, "end": v(81, 277.8) * mm});
            skCircle(sketch, "E553.MirrorC", {"center": v(81, 281.42) * mm, "radius": 3.14 * mm, "construction": true});
            skLineSegment(sketch, "E554.MirrorCS", {"start": v(81, 285.05) * mm, "end": v(77.87, 283.23) * mm});
            skLineSegment(sketch, "E555.MirrorCS", {"start": v(145.19, 150.5) * mm, "end": v(142.05, 152.3) * mm});
            skLineSegment(sketch, "E556.MirrorCS", {"start": v(142.05, 152.3) * mm, "end": v(138.91, 150.5) * mm});
            skCircle(sketch, "E557.MirrorC", {"center": v(142.05, 148.68) * mm, "radius": 3.14 * mm, "construction": true});
            skLineSegment(sketch, "E558.MirrorCS", {"start": v(142.05, 155.52) * mm, "end": v(146.15, 162.63) * mm});
            skCircle(sketch, "E559.MirrorC", {"center": v(142.05, 160.26) * mm, "radius": 2.37 * mm, "construction": true});
            skLineSegment(sketch, "E560.MirrorCS", {"start": v(125.33, 41.69) * mm, "end": v(128.47, 39.88) * mm});
            skLineSegment(sketch, "E561.MirrorCS", {"start": v(72.65, 221.7) * mm, "end": v(69.5, 219.89) * mm});
            skLineSegment(sketch, "E562.MirrorCS", {"start": v(135.36, 177.84) * mm, "end": v(138.5, 179.65) * mm});
            skLineSegment(sketch, "E563.MirrorCS", {"start": v(138.5, 183.28) * mm, "end": v(135.36, 185.09) * mm});
            skLineSegment(sketch, "E564.MirrorCS", {"start": v(128.47, 47.12) * mm, "end": v(125.33, 45.31) * mm});
            skLineSegment(sketch, "E565.MirrorCS", {"start": v(69.5, 216.26) * mm, "end": v(72.65, 214.45) * mm});
            skLineSegment(sketch, "E566.MirrorCS", {"start": v(131.6, 45.31) * mm, "end": v(128.47, 47.12) * mm});
            skLineSegment(sketch, "E567.MirrorCS", {"start": v(75.78, 219.89) * mm, "end": v(72.65, 221.7) * mm});
            skLineSegment(sketch, "E568.MirrorCS", {"start": v(128.47, 39.88) * mm, "end": v(131.6, 41.69) * mm});
            skLineSegment(sketch, "E569.MirrorCS", {"start": v(115.48, 78.91) * mm, "end": v(118.61, 77.1) * mm});
            skLineSegment(sketch, "E570.MirrorCS", {"start": v(147.74, 144.49) * mm, "end": v(152.23, 136.7) * mm});
            skLineSegment(sketch, "E571.MirrorCS", {"start": v(121.75, 82.54) * mm, "end": v(118.61, 84.35) * mm});
            skLineSegment(sketch, "E572.MirrorCS", {"start": v(132.22, 183.28) * mm, "end": v(132.22, 179.65) * mm});
            skLineSegment(sketch, "E573.MirrorCS", {"start": v(119.8, 276.58) * mm, "end": v(119.8, 272.96) * mm});
            skLineSegment(sketch, "E574.MirrorCS", {"start": v(121.75, 78.91) * mm, "end": v(121.75, 82.54) * mm});
            skLineSegment(sketch, "E575.MirrorCS", {"start": v(152.42, 160.7) * mm, "end": v(147.63, 152.41) * mm});
            skLineSegment(sketch, "E576.MirrorCS", {"start": v(135.36, 185.09) * mm, "end": v(132.22, 183.28) * mm});
            skLineSegment(sketch, "E577.MirrorCS", {"start": v(118.61, 77.1) * mm, "end": v(121.75, 78.91) * mm});
            skLineSegment(sketch, "E578.MirrorCS", {"start": v(147.63, 152.41) * mm, "end": v(157.2, 152.41) * mm});
            skLineSegment(sketch, "E579.MirrorCS", {"start": v(72.65, 214.45) * mm, "end": v(75.78, 216.26) * mm});
            skLineSegment(sketch, "E580.MirrorCS", {"start": v(78.9, 88.74) * mm, "end": v(82.05, 90.55) * mm});
            skLineSegment(sketch, "E581.MirrorCS", {"start": v(138.5, 179.65) * mm, "end": v(138.5, 183.28) * mm});
            skLineSegment(sketch, "E582.MirrorCS", {"start": v(78.24, 49.77) * mm, "end": v(78.24, 46.15) * mm});
            skLineSegment(sketch, "E583.MirrorCS", {"start": v(156.73, 78.64) * mm, "end": v(152.86, 85.35) * mm});
            skLineSegment(sketch, "E584.MirrorCS", {"start": v(13.35, 67.38) * mm, "end": v(14.21, 64.3) * mm});
            skLineSegment(sketch, "E585.MirrorCS", {"start": v(75.77, 90.55) * mm, "end": v(78.9, 88.74) * mm});
            skLineSegment(sketch, "E586.MirrorCS", {"start": v(17.31, 63.5) * mm, "end": v(19.55, 65.8) * mm});
            skCircle(sketch, "E587.MirrorC", {"center": v(118.61, 80.72) * mm, "radius": 3.14 * mm, "construction": true});
            skLineSegment(sketch, "E588.MirrorCS", {"start": v(19.55, 65.8) * mm, "end": v(18.69, 68.88) * mm});
            skLineSegment(sketch, "E589.MirrorCS", {"start": v(115.48, 82.54) * mm, "end": v(115.48, 78.91) * mm});
            skLineSegment(sketch, "E590.MirrorCS", {"start": v(128.8, 236.32) * mm, "end": v(131.93, 238.13) * mm});
            skLineSegment(sketch, "E591.MirrorCS", {"start": v(45.32, 302.69) * mm, "end": v(48.46, 300.88) * mm});
            skLineSegment(sketch, "E592.MirrorCS", {"start": v(71.85, 209.4) * mm, "end": v(67.73, 202.27) * mm});
            skCircle(sketch, "E593.MirrorC", {"center": v(152.23, 141.9) * mm, "radius": 2.6 * mm, "construction": true});
            skLineSegment(sketch, "E594.MirrorCS", {"start": v(132.22, 179.65) * mm, "end": v(135.36, 177.84) * mm});
            skLineSegment(sketch, "E595.MirrorCS", {"start": v(18.69, 68.88) * mm, "end": v(15.58, 69.67) * mm});
            skLineSegment(sketch, "E596.MirrorCS", {"start": v(152.23, 136.7) * mm, "end": v(156.73, 144.49) * mm});
            skLineSegment(sketch, "E597.MirrorCS", {"start": v(139.9, 110.56) * mm, "end": v(136.08, 112.76) * mm});
            skLineSegment(sketch, "E598.MirrorCS", {"start": v(132.26, 110.56) * mm, "end": v(132.26, 106.15) * mm});
            skLineSegment(sketch, "E599.MirrorCS", {"start": v(122.94, 278.4) * mm, "end": v(119.8, 276.58) * mm});
            skLineSegment(sketch, "E600.MirrorCS", {"start": v(69.5, 219.89) * mm, "end": v(69.5, 216.26) * mm});
            skLineSegment(sketch, "E601.MirrorCS", {"start": v(157.2, 152.41) * mm, "end": v(152.42, 160.7) * mm});
            skCircle(sketch, "E602.MirrorC", {"center": v(128.47, 43.5) * mm, "radius": 3.14 * mm, "construction": true});
            skLineSegment(sketch, "E603.MirrorCS", {"start": v(156.73, 144.49) * mm, "end": v(147.74, 144.49) * mm});
            skLineSegment(sketch, "E604.MirrorCS", {"start": v(119.8, 272.96) * mm, "end": v(122.94, 271.15) * mm});
            skCircle(sketch, "E605.MirrorC", {"center": v(135.36, 181.46) * mm, "radius": 3.14 * mm, "construction": true});
            skCircle(sketch, "E606.MirrorC", {"center": v(72.65, 218.08) * mm, "radius": 3.14 * mm, "construction": true});
            skLineSegment(sketch, "E607.MirrorCS", {"start": v(139.9, 106.15) * mm, "end": v(139.9, 110.56) * mm});
            skLineSegment(sketch, "E608.MirrorCS", {"start": v(78.9, 95.99) * mm, "end": v(75.77, 94.18) * mm});
            skLineSegment(sketch, "E609.MirrorCS", {"start": v(126.08, 272.96) * mm, "end": v(126.08, 276.58) * mm});
            skLineSegment(sketch, "E610.MirrorCS", {"start": v(15.58, 69.67) * mm, "end": v(13.35, 67.38) * mm});
            skLineSegment(sketch, "E611.MirrorCS", {"start": v(75.78, 216.26) * mm, "end": v(75.78, 219.89) * mm});
            skLineSegment(sketch, "E612.MirrorCS", {"start": v(125.65, 238.13) * mm, "end": v(128.8, 236.32) * mm});
            skLineSegment(sketch, "E613.MirrorCS", {"start": v(82.05, 94.18) * mm, "end": v(78.9, 95.99) * mm});
            skLineSegment(sketch, "E614.MirrorCS", {"start": v(131.6, 41.69) * mm, "end": v(131.6, 45.31) * mm});
            skLineSegment(sketch, "E615.MirrorCS", {"start": v(122.94, 271.15) * mm, "end": v(126.08, 272.96) * mm});
            skLineSegment(sketch, "E616.MirrorCS", {"start": v(125.33, 45.31) * mm, "end": v(125.33, 41.69) * mm});
            skLineSegment(sketch, "E617.MirrorCS", {"start": v(118.61, 84.35) * mm, "end": v(115.48, 82.54) * mm});
            skLineSegment(sketch, "E618.MirrorCS", {"start": v(150.35, 214.73) * mm, "end": v(150.35, 211.1) * mm});
            skLineSegment(sketch, "E619.MirrorCS", {"start": v(110.33, 215.56) * mm, "end": v(121.97, 235.73) * mm});
            skLineSegment(sketch, "E620.MirrorCS", {"start": v(119.88, 88.1) * mm, "end": v(129.64, 105) * mm});
            skLineSegment(sketch, "E621.MirrorCS", {"start": v(131.93, 241.76) * mm, "end": v(128.8, 243.57) * mm});
            skCircle(sketch, "E622.MirrorC", {"center": v(147.9, 173.22) * mm, "radius": 4.24 * mm, "construction": true});
            skLineSegment(sketch, "E623.MirrorCS", {"start": v(14.21, 64.3) * mm, "end": v(17.31, 63.5) * mm});
            skLineSegment(sketch, "E624.MirrorCS", {"start": v(45.55, 249.87) * mm, "end": v(48.69, 248.06) * mm});
            skLineSegment(sketch, "E625.MirrorCS", {"start": v(148.98, 78.64) * mm, "end": v(156.73, 78.64) * mm});
            skLineSegment(sketch, "E626.MirrorCS", {"start": v(131.93, 238.13) * mm, "end": v(131.93, 241.76) * mm});
            skLineSegment(sketch, "E627.MirrorCS", {"start": v(110.12, 105) * mm, "end": v(119.88, 88.1) * mm});
            skLineSegment(sketch, "E628.MirrorCS", {"start": v(149.34, 122.72) * mm, "end": v(142.65, 111.13) * mm});
            skLineSegment(sketch, "E629.MirrorCS", {"start": v(82.05, 90.55) * mm, "end": v(82.05, 94.18) * mm});
            skLineSegment(sketch, "E630.MirrorCS", {"start": v(114.5, 203.52) * mm, "end": v(110.08, 211.18) * mm});
            skLineSegment(sketch, "E631.MirrorCS", {"start": v(140.57, 177.46) * mm, "end": v(147.9, 164.75) * mm});
            skLineSegment(sketch, "E632.MirrorCS", {"start": v(78.24, 46.15) * mm, "end": v(81.38, 44.34) * mm});
            skLineSegment(sketch, "E633.MirrorCS", {"start": v(51.83, 249.87) * mm, "end": v(51.83, 253.5) * mm});
            skLineSegment(sketch, "E634.MirrorCS", {"start": v(48.46, 300.88) * mm, "end": v(51.6, 302.69) * mm});
            skLineSegment(sketch, "E635.MirrorCS", {"start": v(45.55, 253.5) * mm, "end": v(45.55, 249.87) * mm});
            skCircle(sketch, "E636.MirrorC", {"center": v(16.45, 66.59) * mm, "radius": 2.77 * mm, "construction": true});
            skLineSegment(sketch, "E637.MirrorCS", {"start": v(152.86, 85.35) * mm, "end": v(148.98, 78.64) * mm});
            skLineSegment(sketch, "E638.MirrorCS", {"start": v(75.77, 94.18) * mm, "end": v(75.77, 90.55) * mm});
            skCircle(sketch, "E639.MirrorC", {"center": v(119.88, 99.37) * mm, "radius": 5.63 * mm, "construction": true});
            skLineSegment(sketch, "E640.MirrorCS", {"start": v(81.38, 44.34) * mm, "end": v(84.52, 46.15) * mm});
            skLineSegment(sketch, "E641.MirrorCS", {"start": v(128.8, 243.57) * mm, "end": v(125.65, 241.76) * mm});
            skCircle(sketch, "E642.MirrorC", {"center": v(152.86, 80.88) * mm, "radius": 2.24 * mm, "construction": true});
            skLineSegment(sketch, "E643.MirrorCS", {"start": v(125.65, 241.76) * mm, "end": v(125.65, 238.13) * mm});
            skLineSegment(sketch, "E644.MirrorCS", {"start": v(136.46, 118.8) * mm, "end": v(141.75, 127.97) * mm});
            skCircle(sketch, "E645.MirrorC", {"center": v(110.08, 206.07) * mm, "radius": 2.55 * mm, "construction": true});
            skLineSegment(sketch, "E646.MirrorCS", {"start": v(84.52, 46.15) * mm, "end": v(84.52, 49.77) * mm});
            skLineSegment(sketch, "E647.MirrorCS", {"start": v(117.83, 213.25) * mm, "end": v(139.77, 213.25) * mm});
            skLineSegment(sketch, "E648.MirrorCS", {"start": v(146.15, 162.63) * mm, "end": v(137.94, 162.63) * mm});
            skLineSegment(sketch, "E649.MirrorCS", {"start": v(67.73, 202.27) * mm, "end": v(75.96, 202.27) * mm});
            skLineSegment(sketch, "E650.MirrorCS", {"start": v(156.62, 214.73) * mm, "end": v(153.49, 216.54) * mm});
            skCircle(sketch, "E651.MirrorC", {"center": v(128.8, 239.95) * mm, "radius": 3.14 * mm, "construction": true});
            skLineSegment(sketch, "E652.MirrorCS", {"start": v(131.16, 127.97) * mm, "end": v(136.46, 118.8) * mm});
            skLineSegment(sketch, "E653.MirrorCS", {"start": v(148.23, 11.47) * mm, "end": v(151.37, 9.65) * mm});
            skLineSegment(sketch, "E654.MirrorCS", {"start": v(156.62, 211.1) * mm, "end": v(156.62, 214.73) * mm});
            skLineSegment(sketch, "E655.MirrorCS", {"start": v(146.46, 71.94) * mm, "end": v(151.52, 63.18) * mm});
            skLineSegment(sketch, "E656.MirrorCS", {"start": v(129.64, 105) * mm, "end": v(110.12, 105) * mm});
            skCircle(sketch, "E657.MirrorC", {"center": v(78.9, 92.36) * mm, "radius": 3.14 * mm, "construction": true});
            skLineSegment(sketch, "E658.MirrorCS", {"start": v(132.26, 106.15) * mm, "end": v(136.08, 103.94) * mm});
            skLineSegment(sketch, "E659.MirrorCS", {"start": v(135.48, 99.68) * mm, "end": v(125.19, 81.86) * mm});
            skCircle(sketch, "E660.MirrorC", {"center": v(142.2, 135.58) * mm, "radius": 2.81 * mm, "construction": true});
            skLineSegment(sketch, "E661.MirrorCS", {"start": v(151.52, 63.18) * mm, "end": v(156.58, 71.94) * mm});
            skCircle(sketch, "E662.MirrorC", {"center": v(151.52, 69.02) * mm, "radius": 2.92 * mm, "construction": true});
            skCircle(sketch, "E663.MirrorC", {"center": v(71.85, 204.65) * mm, "radius": 2.38 * mm, "construction": true});
            skLineSegment(sketch, "E664.MirrorCS", {"start": v(75.96, 202.27) * mm, "end": v(71.85, 209.4) * mm});
            skLineSegment(sketch, "E665.MirrorCS", {"start": v(81.38, 51.58) * mm, "end": v(78.24, 49.77) * mm});
            skCircle(sketch, "E666.MirrorC", {"center": v(136.08, 108.35) * mm, "radius": 3.82 * mm, "construction": true});
            skLineSegment(sketch, "E667.MirrorCS", {"start": v(45.32, 306.31) * mm, "end": v(45.32, 302.69) * mm});
            skLineSegment(sketch, "E668.MirrorCS", {"start": v(136.08, 112.76) * mm, "end": v(132.26, 110.56) * mm});
            skLineSegment(sketch, "E669.MirrorCS", {"start": v(153.49, 216.54) * mm, "end": v(150.35, 214.73) * mm});
            skCircle(sketch, "E670.MirrorC", {"center": v(122.94, 274.77) * mm, "radius": 3.14 * mm, "construction": true});
            skLineSegment(sketch, "E671.MirrorCS", {"start": v(137.33, 132.77) * mm, "end": v(147.07, 132.77) * mm});
            skLineSegment(sketch, "E672.MirrorCS", {"start": v(150.35, 211.1) * mm, "end": v(153.49, 209.3) * mm});
            skLineSegment(sketch, "E673.MirrorCS", {"start": v(84.52, 49.77) * mm, "end": v(81.38, 51.58) * mm});
            skLineSegment(sketch, "E674.MirrorCS", {"start": v(147.07, 132.77) * mm, "end": v(142.2, 141.2) * mm});
            skLineSegment(sketch, "E675.MirrorCS", {"start": v(142.2, 141.2) * mm, "end": v(137.33, 132.77) * mm});
            skLineSegment(sketch, "E676.MirrorCS", {"start": v(126.08, 276.58) * mm, "end": v(122.94, 278.4) * mm});
            skCircle(sketch, "E677.MirrorC", {"center": v(152.42, 155.17) * mm, "radius": 2.76 * mm, "construction": true});
            skLineSegment(sketch, "E678.MirrorCS", {"start": v(156.58, 71.94) * mm, "end": v(146.46, 71.94) * mm});
            skLineSegment(sketch, "E679.MirrorCS", {"start": v(136.08, 103.94) * mm, "end": v(139.9, 106.15) * mm});
            skLineSegment(sketch, "E680.MirrorCS", {"start": v(128.8, 232.26) * mm, "end": v(117.83, 213.25) * mm});
            skLineSegment(sketch, "E681.MirrorCS", {"start": v(145.77, 81.86) * mm, "end": v(135.48, 99.68) * mm});
            skLineSegment(sketch, "E682.MirrorCS", {"start": v(98.1, 64.14) * mm, "end": v(111.32, 87.04) * mm});
            skLineSegment(sketch, "E683.MirrorCS", {"start": v(84.4, 245.3) * mm, "end": v(59.22, 245.3) * mm});
            skLineSegment(sketch, "E684.MirrorCS", {"start": v(137.58, 242.45) * mm, "end": v(155.65, 242.45) * mm});
            skLineSegment(sketch, "E685.MirrorCS", {"start": v(51.6, 306.31) * mm, "end": v(48.46, 308.12) * mm});
            skLineSegment(sketch, "E686.MirrorCS", {"start": v(48.69, 248.06) * mm, "end": v(51.83, 249.87) * mm});
            skLineSegment(sketch, "E687.MirrorCS", {"start": v(51.6, 302.69) * mm, "end": v(51.6, 306.31) * mm});
            skCircle(sketch, "E688.MirrorC", {"center": v(81.38, 47.96) * mm, "radius": 3.14 * mm, "construction": true});
            skLineSegment(sketch, "E689.MirrorCS", {"start": v(98.68, 235.73) * mm, "end": v(110.33, 215.56) * mm});
            skLineSegment(sketch, "E690.MirrorCS", {"start": v(145.93, 65.96) * mm, "end": v(135.1, 47.2) * mm});
            skLineSegment(sketch, "E691.MirrorCS", {"start": v(129.19, 49.44) * mm, "end": v(143.26, 73.8) * mm});
            skLineSegment(sketch, "E692.MirrorCS", {"start": v(143.26, 73.8) * mm, "end": v(115.12, 73.8) * mm});
            skLineSegment(sketch, "E693.MirrorCS", {"start": v(90.28, 240.2) * mm, "end": v(78.62, 220) * mm});
            skLineSegment(sketch, "E694.MirrorCS", {"start": v(48.46, 308.12) * mm, "end": v(45.32, 306.31) * mm});
            skLineSegment(sketch, "E695.MirrorCS", {"start": v(43.9, 173.4) * mm, "end": v(48.57, 165.31) * mm});
            skLineSegment(sketch, "E696.MirrorCS", {"start": v(151.37, 16.9) * mm, "end": v(148.23, 15.09) * mm});
            skLineSegment(sketch, "E697.MirrorCS", {"start": v(59.22, 245.3) * mm, "end": v(71.81, 223.5) * mm});
            skCircle(sketch, "E698.MirrorC", {"center": v(110.33, 229) * mm, "radius": 6.72 * mm, "construction": true});
            skCircle(sketch, "E699.MirrorC", {"center": v(48.69, 251.68) * mm, "radius": 3.14 * mm, "construction": true});
            skLineSegment(sketch, "E700.MirrorCS", {"start": v(154.5, 15.09) * mm, "end": v(151.37, 16.9) * mm});
            skLineSegment(sketch, "E701.MirrorCS", {"start": v(129.51, 247.03) * mm, "end": v(139.86, 264.96) * mm});
            skLineSegment(sketch, "E702.MirrorCS", {"start": v(44.16, 94.04) * mm, "end": v(71.7, 94.04) * mm});
            skLineSegment(sketch, "E703.MirrorCS", {"start": v(119.16, 264.96) * mm, "end": v(129.51, 247.03) * mm});
            skLineSegment(sketch, "E704.MirrorCS", {"start": v(139.77, 213.25) * mm, "end": v(128.8, 232.26) * mm});
            skLineSegment(sketch, "E705.MirrorCS", {"start": v(48.69, 255.3) * mm, "end": v(45.55, 253.5) * mm});
            skLineSegment(sketch, "E706.MirrorCS", {"start": v(114.05, 111.8) * mm, "end": v(128.56, 111.8) * mm});
            skLineSegment(sketch, "E707.MirrorCS", {"start": v(125.19, 81.86) * mm, "end": v(145.77, 81.86) * mm});
            skLineSegment(sketch, "E708.MirrorCS", {"start": v(57.93, 117.89) * mm, "end": v(44.16, 94.04) * mm});
            skLineSegment(sketch, "E709.MirrorCS", {"start": v(151.37, 9.65) * mm, "end": v(154.5, 11.47) * mm});
            skLineSegment(sketch, "E710.MirrorCS", {"start": v(111.32, 87.04) * mm, "end": v(84.87, 87.04) * mm});
            skCircle(sketch, "E711.MirrorC", {"center": v(153.49, 212.92) * mm, "radius": 3.14 * mm, "construction": true});
            skLineSegment(sketch, "E712.MirrorCS", {"start": v(141.75, 127.97) * mm, "end": v(131.16, 127.97) * mm});
            skCircle(sketch, "E713.MirrorC", {"center": v(92.5, 212) * mm, "radius": 4 * mm, "construction": true});
            skCircle(sketch, "E714.MirrorC", {"center": v(128.8, 219.59) * mm, "radius": 6.33 * mm, "construction": true});
            skLineSegment(sketch, "E715.MirrorCS", {"start": v(34.72, 130.5) * mm, "end": v(44.6, 113.4) * mm});
            skLineSegment(sketch, "E716.MirrorCS", {"start": v(99.45, 216.02) * mm, "end": v(85.57, 216.02) * mm});
            skLineSegment(sketch, "E717.MirrorCS", {"start": v(121.94, 208.7) * mm, "end": v(134.53, 186.9) * mm});
            skLineSegment(sketch, "E718.MirrorCS", {"start": v(140.86, 185.03) * mm, "end": v(156.28, 185.03) * mm});
            skLineSegment(sketch, "E719.MirrorCS", {"start": v(101.37, 243.32) * mm, "end": v(122.3, 243.32) * mm});
            skCircle(sketch, "E720.MirrorC", {"center": v(135.48, 87.8) * mm, "radius": 5.94 * mm, "construction": true});
            skLineSegment(sketch, "E721.MirrorCS", {"start": v(121.97, 235.73) * mm, "end": v(98.68, 235.73) * mm});
            skLineSegment(sketch, "E722.MirrorCS", {"start": v(78.62, 220) * mm, "end": v(101.95, 220) * mm});
            skLineSegment(sketch, "E723.MirrorCS", {"start": v(141.6, 103.53) * mm, "end": v(149.16, 90.45) * mm});
            skLineSegment(sketch, "E724.MirrorCS", {"start": v(134.53, 186.9) * mm, "end": v(147.11, 208.7) * mm});
            skCircle(sketch, "E725.MirrorC", {"center": v(55.62, 208.37) * mm, "radius": 6.34 * mm, "construction": true});
            skCircle(sketch, "E726.MirrorC", {"center": v(48.46, 304.5) * mm, "radius": 3.14 * mm, "construction": true});
            skLineSegment(sketch, "E727.MirrorCS", {"start": v(51.83, 253.5) * mm, "end": v(48.69, 255.3) * mm});
            skLineSegment(sketch, "E728.MirrorCS", {"start": v(101.95, 220) * mm, "end": v(90.28, 240.2) * mm});
            skCircle(sketch, "E729.MirrorC", {"center": v(90.28, 226.73) * mm, "radius": 6.73 * mm, "construction": true});
            skLineSegment(sketch, "E730.MirrorCS", {"start": v(148.57, 198.39) * mm, "end": v(140.86, 185.03) * mm});
            skLineSegment(sketch, "E731.MirrorCS", {"start": v(147.11, 208.7) * mm, "end": v(121.94, 208.7) * mm});
            skLineSegment(sketch, "E732.MirrorCS", {"start": v(153.49, 209.3) * mm, "end": v(156.62, 211.1) * mm});
            skLineSegment(sketch, "E733.MirrorCS", {"start": v(134.46, 38.33) * mm, "end": v(144.93, 20.2) * mm});
            skLineSegment(sketch, "E734.MirrorCS", {"start": v(134.9, 236.6) * mm, "end": v(145.36, 218.47) * mm});
            skLineSegment(sketch, "E735.MirrorCS", {"start": v(66.6, 224.03) * mm, "end": v(55.37, 243.48) * mm});
            skLineSegment(sketch, "E736.MirrorCS", {"start": v(154.5, 11.47) * mm, "end": v(154.5, 15.09) * mm});
            skLineSegment(sketch, "E737.MirrorCS", {"start": v(122.3, 243.32) * mm, "end": v(111.83, 261.45) * mm});
            skCircle(sketch, "E738.MirrorC", {"center": v(136.46, 124.92) * mm, "radius": 3.06 * mm, "construction": true});
            skLineSegment(sketch, "E739.MirrorCS", {"start": v(148.23, 15.09) * mm, "end": v(148.23, 11.47) * mm});
            skLineSegment(sketch, "E740.MirrorCS", {"start": v(135.1, 47.2) * mm, "end": v(156.76, 47.2) * mm});
            skLineSegment(sketch, "E741.MirrorCS", {"start": v(100.15, 256.3) * mm, "end": v(113.07, 278.7) * mm});
            skLineSegment(sketch, "E742.MirrorCS", {"start": v(142.65, 111.13) * mm, "end": v(156.03, 111.13) * mm});
            skLineSegment(sketch, "E743.MirrorCS", {"start": v(53.36, 137.66) * mm, "end": v(45.86, 150.67) * mm});
            skLineSegment(sketch, "E744.MirrorCS", {"start": v(38.35, 137.66) * mm, "end": v(53.36, 137.66) * mm});
            skLineSegment(sketch, "E745.MirrorCS", {"start": v(110.08, 211.18) * mm, "end": v(105.66, 203.52) * mm});
            skLineSegment(sketch, "E746.MirrorCS", {"start": v(146.62, 258.1) * mm, "end": v(137.58, 242.45) * mm});
            skLineSegment(sketch, "E747.MirrorCS", {"start": v(71.81, 223.5) * mm, "end": v(84.4, 245.3) * mm});
            skLineSegment(sketch, "E748.MirrorCS", {"start": v(87.22, 278.7) * mm, "end": v(100.15, 256.3) * mm});
            skLineSegment(sketch, "E749.MirrorCS", {"start": v(84.87, 87.04) * mm, "end": v(98.1, 64.14) * mm});
            skLineSegment(sketch, "E750.MirrorCS", {"start": v(115.12, 73.8) * mm, "end": v(129.19, 49.44) * mm});
            skLineSegment(sketch, "E751.MirrorCS", {"start": v(155.65, 242.45) * mm, "end": v(146.62, 258.1) * mm});
            skLineSegment(sketch, "E752.MirrorCS", {"start": v(155.4, 38.33) * mm, "end": v(134.46, 38.33) * mm});
            skCircle(sketch, "E753.MirrorC", {"center": v(129.19, 65.69) * mm, "radius": 8.12 * mm, "construction": true});
            skCircle(sketch, "E754.MirrorC", {"center": v(48.57, 170.7) * mm, "radius": 2.7 * mm, "construction": true});
            skLineSegment(sketch, "E755.MirrorCS", {"start": v(45.86, 150.67) * mm, "end": v(38.35, 137.66) * mm});
            skCircle(sketch, "E756.MirrorC", {"center": v(146.62, 247.67) * mm, "radius": 5.22 * mm, "construction": true});
            skLineSegment(sketch, "E757.MirrorCS", {"start": v(147.9, 164.75) * mm, "end": v(155.24, 177.46) * mm});
            skCircle(sketch, "E758.MirrorC", {"center": v(149.34, 114.99) * mm, "radius": 3.86 * mm, "construction": true});
            skCircle(sketch, "E759.MirrorC", {"center": v(145.93, 53.46) * mm, "radius": 6.25 * mm, "construction": true});
            skCircle(sketch, "E760.MirrorC", {"center": v(98.1, 79.4) * mm, "radius": 7.63 * mm, "construction": true});
            skLineSegment(sketch, "E761.MirrorCS", {"start": v(60.52, 308.84) * mm, "end": v(46.75, 284.98) * mm});
            skCircle(sketch, "E762.MirrorC", {"center": v(45.86, 142) * mm, "radius": 4.33 * mm, "construction": true});
            skLineSegment(sketch, "E763.MirrorCS", {"start": v(66.6, 214.71) * mm, "end": v(44.65, 214.71) * mm});
            skLineSegment(sketch, "E764.MirrorCS", {"start": v(71.7, 94.04) * mm, "end": v(57.93, 117.89) * mm});
            skLineSegment(sketch, "E765.MirrorCS", {"start": v(65.51, 249.73) * mm, "end": v(95.78, 249.73) * mm});
            skLineSegment(sketch, "E766.MirrorCS", {"start": v(156.28, 185.03) * mm, "end": v(148.57, 198.39) * mm});
            skLineSegment(sketch, "E767.MirrorCS", {"start": v(85.57, 216.02) * mm, "end": v(92.5, 203.99) * mm});
            skLineSegment(sketch, "E768.MirrorCS", {"start": v(155.83, 236.6) * mm, "end": v(134.9, 236.6) * mm});
            skLineSegment(sketch, "E769.MirrorCS", {"start": v(80.65, 275.94) * mm, "end": v(65.51, 249.73) * mm});
            skLineSegment(sketch, "E770.MirrorCS", {"start": v(48.57, 165.31) * mm, "end": v(53.23, 173.4) * mm});
            skCircle(sketch, "E771.MirrorC", {"center": v(49.83, 187.9) * mm, "radius": 3.26 * mm, "construction": true});
            skLineSegment(sketch, "E772.MirrorCS", {"start": v(111.83, 261.45) * mm, "end": v(101.37, 243.32) * mm});
            skCircle(sketch, "E773.MirrorC", {"center": v(134.53, 201.43) * mm, "radius": 7.27 * mm, "construction": true});
            skLineSegment(sketch, "E774.MirrorCS", {"start": v(44.6, 113.4) * mm, "end": v(54.46, 130.5) * mm});
            skCircle(sketch, "E775.MirrorC", {"center": v(149.16, 99.17) * mm, "radius": 4.36 * mm, "construction": true});
            skLineSegment(sketch, "E776.MirrorCS", {"start": v(49.83, 194.42) * mm, "end": v(44.19, 184.64) * mm});
            skLineSegment(sketch, "E777.MirrorCS", {"start": v(55.37, 243.48) * mm, "end": v(44.14, 224.03) * mm});
            skLineSegment(sketch, "E778.MirrorCS", {"start": v(67.58, 308.65) * mm, "end": v(80.17, 286.85) * mm});
            skLineSegment(sketch, "E779.MirrorCS", {"start": v(55.62, 195.7) * mm, "end": v(66.6, 214.71) * mm});
            skLineSegment(sketch, "E780.MirrorCS", {"start": v(106.96, 69.48) * mm, "end": v(94.25, 47.47) * mm});
            skCircle(sketch, "E781.MirrorC", {"center": v(55.37, 230.51) * mm, "radius": 6.48 * mm, "construction": true});
            skCircle(sketch, "E782.MirrorC", {"center": v(71.81, 238.04) * mm, "radius": 7.27 * mm, "construction": true});
            skLineSegment(sketch, "E783.MirrorCS", {"start": v(72.36, 87.57) * mm, "end": v(43, 87.57) * mm});
            skLineSegment(sketch, "E784.MirrorCS", {"start": v(142.23, 11.6) * mm, "end": v(127.1, 37.81) * mm});
            skLineSegment(sketch, "E785.MirrorCS", {"start": v(92.5, 203.99) * mm, "end": v(99.45, 216.02) * mm});
            skCircle(sketch, "E786.MirrorC", {"center": v(98.45, 100.76) * mm, "radius": 7.55 * mm, "construction": true});
            skCircle(sketch, "E787.MirrorC", {"center": v(145.36, 230.56) * mm, "radius": 6.05 * mm, "construction": true});
            skLineSegment(sketch, "E788.MirrorCS", {"start": v(53.23, 173.4) * mm, "end": v(43.9, 173.4) * mm});
            skCircle(sketch, "E789.MirrorC", {"center": v(144.93, 32.28) * mm, "radius": 6.05 * mm, "construction": true});
            skLineSegment(sketch, "E790.MirrorCS", {"start": v(95.78, 249.73) * mm, "end": v(80.65, 275.94) * mm});
            skLineSegment(sketch, "E791.MirrorCS", {"start": v(119.68, 47.47) * mm, "end": v(106.96, 69.48) * mm});
            skLineSegment(sketch, "E792.MirrorCS", {"start": v(94.25, 58.47) * mm, "end": v(79.12, 84.69) * mm});
            skCircle(sketch, "E793.MirrorC", {"center": v(148.57, 189.48) * mm, "radius": 4.45 * mm, "construction": true});
            skLineSegment(sketch, "E794.MirrorCS", {"start": v(44.65, 214.71) * mm, "end": v(55.62, 195.7) * mm});
            skLineSegment(sketch, "E795.MirrorCS", {"start": v(34.05, 89.73) * mm, "end": v(22.38, 69.53) * mm});
            skLineSegment(sketch, "E796.MirrorCS", {"start": v(86.98, 283.34) * mm, "end": v(110.3, 283.34) * mm});
            skCircle(sketch, "E797.MirrorC", {"center": v(129.51, 258.99) * mm, "radius": 5.98 * mm, "construction": true});
            skLineSegment(sketch, "E798.MirrorCS", {"start": v(113.07, 278.7) * mm, "end": v(87.22, 278.7) * mm});
            skLineSegment(sketch, "E799.MirrorCS", {"start": v(156.03, 111.13) * mm, "end": v(149.34, 122.72) * mm});
            skLineSegment(sketch, "E800.MirrorCS", {"start": v(68.6, 116.78) * mm, "end": v(78.32, 99.95) * mm});
            skLineSegment(sketch, "E801.MirrorCS", {"start": v(139.86, 264.96) * mm, "end": v(119.16, 264.96) * mm});
            skLineSegment(sketch, "E802.MirrorCS", {"start": v(85.36, 93.2) * mm, "end": v(111.53, 93.2) * mm});
            skLineSegment(sketch, "E803.MirrorCS", {"start": v(149.16, 90.45) * mm, "end": v(156.71, 103.53) * mm});
            skCircle(sketch, "E804.MirrorC", {"center": v(151.37, 13.28) * mm, "radius": 3.14 * mm, "construction": true});
            skLineSegment(sketch, "E805.MirrorCS", {"start": v(60.27, 253.1) * mm, "end": v(74.95, 278.51) * mm});
            skLineSegment(sketch, "E806.MirrorCS", {"start": v(98.64, 303.55) * mm, "end": v(86.98, 283.34) * mm});
            skCircle(sketch, "E807.MirrorC", {"center": v(111.83, 249.37) * mm, "radius": 6.04 * mm, "construction": true});
            skCircle(sketch, "E808.MirrorC", {"center": v(57.93, 101.99) * mm, "radius": 7.95 * mm, "construction": true});
            skLineSegment(sketch, "E809.MirrorCS", {"start": v(55.48, 184.64) * mm, "end": v(49.83, 194.42) * mm});
            skCircle(sketch, "E810.MirrorC", {"center": v(44.6, 124.8) * mm, "radius": 5.7 * mm, "construction": true});
            skLineSegment(sketch, "E811.MirrorCS", {"start": v(44.14, 224.03) * mm, "end": v(66.6, 224.03) * mm});
            skLineSegment(sketch, "E812.MirrorCS", {"start": v(121.3, 124.37) * mm, "end": v(114.05, 111.8) * mm});
            skLineSegment(sketch, "E813.MirrorCS", {"start": v(54.46, 130.5) * mm, "end": v(34.72, 130.5) * mm});
            skLineSegment(sketch, "E814.MirrorCS", {"start": v(17.95, 106.12) * mm, "end": v(38.3, 106.12) * mm});
            skLineSegment(sketch, "E815.MirrorCS", {"start": v(44.19, 184.64) * mm, "end": v(55.48, 184.64) * mm});
            skLineSegment(sketch, "E816.MirrorCS", {"start": v(105.66, 203.52) * mm, "end": v(114.5, 203.52) * mm});
            skCircle(sketch, "E817.MirrorC", {"center": v(106.71, 31.9) * mm, "radius": 8.47 * mm, "construction": true});
            skLineSegment(sketch, "E818.MirrorCS", {"start": v(92.03, 40.38) * mm, "end": v(106.71, 14.96) * mm});
            skLineSegment(sketch, "E819.MirrorCS", {"start": v(106.71, 14.96) * mm, "end": v(121.4, 40.38) * mm});
            skLineSegment(sketch, "E820.MirrorCS", {"start": v(121.4, 40.38) * mm, "end": v(92.03, 40.38) * mm});
            skCircle(sketch, "E821.MirrorC", {"center": v(127.1, 20.34) * mm, "radius": 8.74 * mm, "construction": true});
            skLineSegment(sketch, "E822.MirrorCS", {"start": v(127.1, 37.81) * mm, "end": v(111.96, 11.6) * mm});
            skCircle(sketch, "E823.MirrorC", {"center": v(100.15, 271.23) * mm, "radius": 7.46 * mm, "construction": true});
            skLineSegment(sketch, "E824.MirrorCS", {"start": v(79.12, 84.69) * mm, "end": v(63.98, 58.47) * mm});
            skLineSegment(sketch, "E825.MirrorCS", {"start": v(45.71, 69.53) * mm, "end": v(34.05, 89.73) * mm});
            skLineSegment(sketch, "E826.MirrorCS", {"start": v(46.75, 284.98) * mm, "end": v(74.3, 284.98) * mm});
            skLineSegment(sketch, "E827.MirrorCS", {"start": v(63.98, 58.47) * mm, "end": v(94.25, 58.47) * mm});
            skCircle(sketch, "E828.MirrorC", {"center": v(78.32, 111.17) * mm, "radius": 5.61 * mm, "construction": true});
            skCircle(sketch, "E829.MirrorC", {"center": v(106.96, 54.8) * mm, "radius": 7.34 * mm, "construction": true});
            skLineSegment(sketch, "E830.MirrorCS", {"start": v(155.24, 177.46) * mm, "end": v(140.57, 177.46) * mm});
            skLineSegment(sketch, "E831.MirrorCS", {"start": v(94.25, 47.47) * mm, "end": v(119.68, 47.47) * mm});
            skLineSegment(sketch, "E832.MirrorCS", {"start": v(80.17, 286.85) * mm, "end": v(92.76, 308.65) * mm});
            skCircle(sketch, "E833.MirrorC", {"center": v(28.12, 112) * mm, "radius": 5.87 * mm, "construction": true});
            skCircle(sketch, "E834.MirrorC", {"center": v(60.27, 270.04) * mm, "radius": 8.47 * mm, "construction": true});
            skLineSegment(sketch, "E835.MirrorCS", {"start": v(92.76, 308.65) * mm, "end": v(67.58, 308.65) * mm});
            skLineSegment(sketch, "E836.MirrorCS", {"start": v(156.76, 47.2) * mm, "end": v(145.93, 65.96) * mm});
            skLineSegment(sketch, "E837.MirrorCS", {"start": v(78.32, 99.95) * mm, "end": v(88.04, 116.78) * mm});
            skCircle(sketch, "E838.MirrorC", {"center": v(34.05, 76.26) * mm, "radius": 6.73 * mm, "construction": true});
            skLineSegment(sketch, "E839.MirrorCS", {"start": v(111.53, 93.2) * mm, "end": v(98.45, 115.86) * mm});
            skCircle(sketch, "E840.MirrorC", {"center": v(80.17, 301.39) * mm, "radius": 7.27 * mm, "construction": true});
            skCircle(sketch, "E841.MirrorC", {"center": v(57.68, 79.1) * mm, "radius": 8.47 * mm, "construction": true});
            skCircle(sketch, "E842.MirrorC", {"center": v(98.64, 290.08) * mm, "radius": 6.73 * mm, "construction": true});
            skLineSegment(sketch, "E843.MirrorCS", {"start": v(28.12, 123.75) * mm, "end": v(17.95, 106.12) * mm});
            skLineSegment(sketch, "E844.MirrorCS", {"start": v(128.56, 111.8) * mm, "end": v(121.3, 124.37) * mm});
            skLineSegment(sketch, "E845.MirrorCS", {"start": v(45.6, 278.51) * mm, "end": v(60.27, 253.1) * mm});
            skLineSegment(sketch, "E846.MirrorCS", {"start": v(98.45, 115.86) * mm, "end": v(85.36, 93.2) * mm});
            skCircle(sketch, "E847.MirrorC", {"center": v(121.3, 116) * mm, "radius": 4.19 * mm, "construction": true});
            skCircle(sketch, "E848.MirrorC", {"center": v(60.52, 292.93) * mm, "radius": 7.95 * mm, "construction": true});
            skLineSegment(sketch, "E849.MirrorCS", {"start": v(74.95, 278.51) * mm, "end": v(45.6, 278.51) * mm});
            skLineSegment(sketch, "E850.MirrorCS", {"start": v(156.71, 103.53) * mm, "end": v(141.6, 103.53) * mm});
            skLineSegment(sketch, "E851.MirrorCS", {"start": v(144.93, 20.2) * mm, "end": v(155.4, 38.33) * mm});
            skLineSegment(sketch, "E852.MirrorCS", {"start": v(145.36, 218.47) * mm, "end": v(155.83, 236.6) * mm});
            skLineSegment(sketch, "E853.MirrorCS", {"start": v(57.68, 62.14) * mm, "end": v(72.36, 87.57) * mm});
            skLineSegment(sketch, "E854.MirrorCS", {"start": v(38.3, 106.12) * mm, "end": v(28.12, 123.75) * mm});
            skCircle(sketch, "E855.MirrorC", {"center": v(80.65, 258.47) * mm, "radius": 8.74 * mm, "construction": true});
            skCircle(sketch, "E856.MirrorC", {"center": v(79.12, 67.21) * mm, "radius": 8.74 * mm, "construction": true});
            skLineSegment(sketch, "E857.MirrorCS", {"start": v(111.96, 11.6) * mm, "end": v(142.23, 11.6) * mm});
            skLineSegment(sketch, "E858.MirrorCS", {"start": v(110.3, 283.34) * mm, "end": v(98.64, 303.55) * mm});
            skLineSegment(sketch, "E859.MirrorCS", {"start": v(74.3, 284.98) * mm, "end": v(60.52, 308.84) * mm});
            skLineSegment(sketch, "E860.MirrorCS", {"start": v(22.38, 69.53) * mm, "end": v(45.71, 69.53) * mm});
            skLineSegment(sketch, "E861.MirrorCS", {"start": v(88.04, 116.78) * mm, "end": v(68.6, 116.78) * mm});
            skLineSegment(sketch, "E862.MirrorCS", {"start": v(43, 87.57) * mm, "end": v(57.68, 62.14) * mm});
            skPoint(sketch, "E863.MirrorP", {"position": v(51.04, 105.96) * mm});
            skPoint(sketch, "E864.MirrorP", {"position": v(138.91, 148.68) * mm});
            skPoint(sketch, "E865.MirrorP", {"position": v(46.23, 169.35) * mm});
            skPoint(sketch, "E866.MirrorP", {"position": v(107.87, 207.35) * mm});
            skPoint(sketch, "E867.MirrorP", {"position": v(125.65, 239.95) * mm});
            skPoint(sketch, "E868.MirrorP", {"position": v(128.23, 197.8) * mm});
            skPoint(sketch, "E869.MirrorP", {"position": v(119.52, 24.7) * mm});
            skPoint(sketch, "E870.MirrorP", {"position": v(73.46, 108.36) * mm});
            skPoint(sketch, "E871.MirrorP", {"position": v(117.68, 118.1) * mm});
            skPoint(sketch, "E872.MirrorP", {"position": v(123.31, 222.75) * mm});
            skPoint(sketch, "E873.MirrorP", {"position": v(91.9, 104.53) * mm});
            skPoint(sketch, "E874.MirrorP", {"position": v(139.7, 29.26) * mm});
            skPoint(sketch, "E875.MirrorP", {"position": v(77.87, 281.42) * mm});
            skPoint(sketch, "E876.MirrorP", {"position": v(144.72, 191.7) * mm});
            skPoint(sketch, "E877.MirrorP", {"position": v(104.5, 225.65) * mm});
            skPoint(sketch, "E878.MirrorP", {"position": v(69.5, 218.08) * mm});
            skPoint(sketch, "E879.MirrorP", {"position": v(39.66, 121.96) * mm});
            skPoint(sketch, "E880.MirrorP", {"position": v(50.14, 205.2) * mm});
            skPoint(sketch, "E881.MirrorP", {"position": v(91.48, 75.6) * mm});
            skPoint(sketch, "E882.MirrorP", {"position": v(149, 67.56) * mm});
            skPoint(sketch, "E883.MirrorP", {"position": v(149.99, 140.6) * mm});
            skPoint(sketch, "E884.MirrorP", {"position": v(150.92, 82) * mm});
            skPoint(sketch, "E885.MirrorP", {"position": v(146, 116.92) * mm});
            skPoint(sketch, "E886.MirrorP", {"position": v(28.22, 79.63) * mm});
            skPoint(sketch, "E887.MirrorP", {"position": v(23.04, 114.93) * mm});
            skPoint(sketch, "E888.MirrorP", {"position": v(75.77, 92.36) * mm});
            skPoint(sketch, "E889.MirrorP", {"position": v(71.55, 71.58) * mm});
            skPoint(sketch, "E890.MirrorP", {"position": v(133.81, 123.39) * mm});
            skPoint(sketch, "E891.MirrorP", {"position": v(53.64, 296.91) * mm});
            skPoint(sketch, "E892.MirrorP", {"position": v(140.13, 227.53) * mm});
            skPoint(sketch, "E893.MirrorP", {"position": v(69.8, 205.83) * mm});
            skPoint(sketch, "E894.MirrorP", {"position": v(47, 189.53) * mm});
            skPoint(sketch, "E895.MirrorP", {"position": v(50.34, 74.85) * mm});
            skPoint(sketch, "E896.MirrorP", {"position": v(115, 96.56) * mm});
            skPoint(sketch, "E897.MirrorP", {"position": v(93.69, 267.5) * mm});
            skPoint(sketch, "E898.MirrorP", {"position": v(65.52, 234.4) * mm});
            skPoint(sketch, "E899.MirrorP", {"position": v(122.16, 61.62) * mm});
            skPoint(sketch, "E900.MirrorP", {"position": v(139.76, 136.98) * mm});
            skPoint(sketch, "E901.MirrorP", {"position": v(150.03, 156.55) * mm});
            skPoint(sketch, "E902.MirrorP", {"position": v(132.26, 108.35) * mm});
            skPoint(sketch, "E903.MirrorP", {"position": v(89.04, 210) * mm});
            skPoint(sketch, "E904.MirrorP", {"position": v(92.8, 293.45) * mm});
            skPoint(sketch, "E905.MirrorP", {"position": v(125.33, 43.5) * mm});
            skPoint(sketch, "E906.MirrorP", {"position": v(49.76, 233.76) * mm});
            skPoint(sketch, "E907.MirrorP", {"position": v(144.24, 171.1) * mm});
            skPoint(sketch, "E908.MirrorP", {"position": v(42.1, 144.17) * mm});
            skPoint(sketch, "E909.MirrorP", {"position": v(140.52, 56.58) * mm});
            skPoint(sketch, "E910.MirrorP", {"position": v(140, 159.08) * mm});
            skPoint(sketch, "E911.MirrorP", {"position": v(124.34, 256) * mm});
            skPoint(sketch, "E912.MirrorP", {"position": v(52.93, 265.8) * mm});
            skPoint(sketch, "E913.MirrorP", {"position": v(145.38, 96.99) * mm});
            skPoint(sketch, "E914.MirrorP", {"position": v(73.88, 297.75) * mm});
            skPoint(sketch, "E915.MirrorP", {"position": v(84.45, 230.1) * mm});
            skPoint(sketch, "E916.MirrorP", {"position": v(100.6, 58.47) * mm});
            skPoint(sketch, "E917.MirrorP", {"position": v(73.08, 262.84) * mm});
            skPoint(sketch, "E918.MirrorP", {"position": v(130.33, 90.77) * mm});
            skPoint(sketch, "E919.MirrorP", {"position": v(99.37, 27.67) * mm});
            skPoint(sketch, "E920.MirrorP", {"position": v(142.1, 250.27) * mm});
            skPoint(sketch, "E921.MirrorP", {"position": v(106.6, 252.39) * mm});
            skCircle(sketch, "E922.cCircle", {"center": v(16.53, 89.46) * mm, "radius": 7.27 * mm, "construction": true});
            skLineSegment(sketch, "E922.0", {"start": v(29.12, 96.73) * mm, "end": v(16.53, 74.93) * mm});
            skLineSegment(sketch, "E922.1", {"start": v(16.53, 74.93) * mm, "end": v(3.94, 96.73) * mm});
            skLineSegment(sketch, "E922.2", {"start": v(3.94, 96.73) * mm, "end": v(29.12, 96.73) * mm});
            skPoint(sketch, "E922.0.midPoint", {"position": v(22.82, 85.83) * mm});
            skCircle(sketch, "E923.cCircle", {"center": v(-35.43, 97.09) * mm, "radius": 2.77 * mm, "construction": true});
            skLineSegment(sketch, "E923.0", {"start": v(-32.33, 97.88) * mm, "end": v(-33.2, 94.8) * mm});
            skLineSegment(sketch, "E923.1", {"start": v(-33.2, 94.8) * mm, "end": v(-36.3, 94) * mm});
            skLineSegment(sketch, "E923.2", {"start": v(-36.3, 94) * mm, "end": v(-38.53, 96.3) * mm});
            skLineSegment(sketch, "E923.3", {"start": v(-38.53, 96.3) * mm, "end": v(-37.67, 99.38) * mm});
            skLineSegment(sketch, "E923.4", {"start": v(-37.67, 99.38) * mm, "end": v(-34.57, 100.17) * mm});
            skLineSegment(sketch, "E923.5", {"start": v(-34.57, 100.17) * mm, "end": v(-32.33, 97.88) * mm});
            skCircle(sketch, "E924.cCircle", {"center": v(37.7, 97.09) * mm, "radius": 2.77 * mm, "construction": true});
            skLineSegment(sketch, "E924.0", {"start": v(40.81, 97.88) * mm, "end": v(39.95, 94.8) * mm});
            skLineSegment(sketch, "E924.1", {"start": v(39.95, 94.8) * mm, "end": v(36.84, 94) * mm});
            skLineSegment(sketch, "E924.2", {"start": v(36.84, 94) * mm, "end": v(34.6, 96.3) * mm});
            skLineSegment(sketch, "E924.3", {"start": v(34.6, 96.3) * mm, "end": v(35.47, 99.38) * mm});
            skLineSegment(sketch, "E924.4", {"start": v(35.47, 99.38) * mm, "end": v(38.57, 100.17) * mm});
            skLineSegment(sketch, "E924.5", {"start": v(38.57, 100.17) * mm, "end": v(40.81, 97.88) * mm});
            skCircle(sketch, "E925.cCircle", {"center": v(-0.59, 108.64) * mm, "radius": 4.23 * mm, "construction": true});
            skLineSegment(sketch, "E925.0", {"start": v(-0.59, 117.1) * mm, "end": v(6.74, 104.41) * mm});
            skLineSegment(sketch, "E925.1", {"start": v(6.74, 104.41) * mm, "end": v(-7.91, 104.41) * mm});
            skLineSegment(sketch, "E925.2", {"start": v(-7.91, 104.41) * mm, "end": v(-0.59, 117.1) * mm});
            skPoint(sketch, "E925.0.midPoint", {"position": v(3.08, 110.76) * mm});
            skCircle(sketch, "E926.cCircle", {"center": v(1.1, 76.45) * mm, "radius": 4.57 * mm, "construction": true});
            skLineSegment(sketch, "E926.0", {"start": v(1.1, 85.59) * mm, "end": v(9.02, 71.88) * mm});
            skLineSegment(sketch, "E926.1", {"start": v(9.02, 71.88) * mm, "end": v(-6.8, 71.88) * mm});
            skLineSegment(sketch, "E926.2", {"start": v(-6.8, 71.88) * mm, "end": v(1.1, 85.59) * mm});
            skPoint(sketch, "E926.0.midPoint", {"position": v(5.07, 78.73) * mm});
            skSolve(sketch);
        }
        {
            var Q0;
            Q0=makeQuery(id+"F10.imprint","IMPRINT",FACE,{"disambiguationData":[TD([[makeQuery(id+"F10.imprint","IMPRINT",EDGE,{"derivedFrom":sQuery(id+"F10.wireOp",EDGE,"E495.0")}),-1.0]])]});
            var Q1;
            Q1=makeQuery(id+"F10.imprint","IMPRINT",FACE,{"disambiguationData":[TD([[makeQuery(id+"F10.imprint","IMPRINT",EDGE,{"derivedFrom":sQuery(id+"F10.wireOp",EDGE,"E496.0")}),-1.0]])]});
            var Q2;
            Q2=makeQuery(id+"F10.imprint","IMPRINT",FACE,{"disambiguationData":[TD([[makeQuery(id+"F10.imprint","IMPRINT",EDGE,{"derivedFrom":sQuery(id+"F10.wireOp",EDGE,"E494.0")}),-1.0]])]});
            var Q3;
            Q3=makeQuery(id+"F10.imprint","IMPRINT",FACE,{"disambiguationData":[TD([[makeQuery(id+"F10.imprint","IMPRINT",EDGE,{"derivedFrom":sQuery(id+"F10.wireOp",EDGE,"E493.0")}),-1.0]])]});
            var Q4;
            Q4=makeQuery(id+"F10.imprint","IMPRINT",FACE,{"disambiguationData":[TD([[makeQuery(id+"F10.imprint","IMPRINT",EDGE,{"derivedFrom":sQuery(id+"F10.wireOp",EDGE,"E492.0")}),-1.0]])]});
            var Q5;
            Q5=makeQuery(id+"F10.imprint","IMPRINT",FACE,{"disambiguationData":[TD([[makeQuery(id+"F10.imprint","IMPRINT",EDGE,{"derivedFrom":sQuery(id+"F10.wireOp",EDGE,"E497.0")}),-1.0]])]});
            var Q6;
            Q6=makeQuery(id+"F10.imprint","IMPRINT",FACE,{"disambiguationData":[TD([[makeQuery(id+"F10.imprint","IMPRINT",EDGE,{"derivedFrom":sQuery(id+"F10.wireOp",EDGE,"E508.0")}),-1.0]])]});
            var Q7;
            Q7=makeQuery(id+"F10.imprint","IMPRINT",FACE,{"disambiguationData":[TD([[makeQuery(id+"F10.imprint","IMPRINT",EDGE,{"derivedFrom":sQuery(id+"F10.wireOp",EDGE,"E542.0")}),-1.0]])]});
            var Q8;
            Q8=makeQuery(id+"F10.imprint","IMPRINT",FACE,{"disambiguationData":[TD([[makeQuery(id+"F10.imprint","IMPRINT",EDGE,{"derivedFrom":sQuery(id+"F10.wireOp",EDGE,"E540.0")}),-1.0]])]});
            var Q9;
            Q9=makeQuery(id+"F10.imprint","IMPRINT",FACE,{"disambiguationData":[TD([[makeQuery(id+"F10.imprint","IMPRINT",EDGE,{"derivedFrom":sQuery(id+"F10.wireOp",EDGE,"E510.0")}),-1.0]])]});
            var Q10;
            Q10=makeQuery(id+"F10.imprint","IMPRINT",FACE,{"disambiguationData":[TD([[makeQuery(id+"F10.imprint","IMPRINT",EDGE,{"derivedFrom":sQuery(id+"F10.wireOp",EDGE,"E512.0")}),-1.0]])]});
            var Q11;
            Q11=makeQuery(id+"F10.imprint","IMPRINT",FACE,{"disambiguationData":[TD([[makeQuery(id+"F10.imprint","IMPRINT",EDGE,{"derivedFrom":sQuery(id+"F10.wireOp",EDGE,"E513.0")}),-1.0]])]});
            var Q12;
            Q12=makeQuery(id+"F10.imprint","IMPRINT",FACE,{"disambiguationData":[TD([[makeQuery(id+"F10.imprint","IMPRINT",EDGE,{"derivedFrom":sQuery(id+"F10.wireOp",EDGE,"E511.0")}),-1.0]])]});
            var Q13;
            Q13=makeQuery(id+"F10.imprint","IMPRINT",FACE,{"disambiguationData":[TD([[makeQuery(id+"F10.imprint","IMPRINT",EDGE,{"derivedFrom":sQuery(id+"F10.wireOp",EDGE,"E523.0")}),-1.0]])]});
            var Q14;
            Q14=makeQuery(id+"F10.imprint","IMPRINT",FACE,{"disambiguationData":[TD([[makeQuery(id+"F10.imprint","IMPRINT",EDGE,{"derivedFrom":sQuery(id+"F10.wireOp",EDGE,"E525.0")}),-1.0]])]});
            var Q15;
            Q15=makeQuery(id+"F10.imprint","IMPRINT",FACE,{"disambiguationData":[TD([[makeQuery(id+"F10.imprint","IMPRINT",EDGE,{"derivedFrom":sQuery(id+"F10.wireOp",EDGE,"E509.0")}),-1.0]])]});
            var Q16;
            Q16=makeQuery(id+"F10.imprint","IMPRINT",FACE,{"disambiguationData":[TD([[makeQuery(id+"F10.imprint","IMPRINT",EDGE,{"derivedFrom":sQuery(id+"F10.wireOp",EDGE,"E541.0")}),-1.0]])]});
            var Q17;
            Q17=makeQuery(id+"F10.imprint","IMPRINT",FACE,{"disambiguationData":[TD([[makeQuery(id+"F10.imprint","IMPRINT",EDGE,{"derivedFrom":sQuery(id+"F10.wireOp",EDGE,"E501.0")}),-1.0]])]});
            var Q18;
            Q18=makeQuery(id+"F10.imprint","IMPRINT",FACE,{"disambiguationData":[TD([[makeQuery(id+"F10.imprint","IMPRINT",EDGE,{"derivedFrom":sQuery(id+"F10.wireOp",EDGE,"E507.0")}),-1.0]])]});
            var Q19;
            Q19=makeQuery(id+"F10.imprint","IMPRINT",FACE,{"disambiguationData":[TD([[makeQuery(id+"F10.imprint","IMPRINT",EDGE,{"derivedFrom":sQuery(id+"F10.wireOp",EDGE,"E503.0")}),-1.0]])]});
            var Q20;
            Q20=makeQuery(id+"F10.imprint","IMPRINT",FACE,{"disambiguationData":[TD([[makeQuery(id+"F10.imprint","IMPRINT",EDGE,{"derivedFrom":sQuery(id+"F10.wireOp",EDGE,"E498.0")}),-1.0]])]});
            var Q21;
            Q21=makeQuery(id+"F10.imprint","IMPRINT",FACE,{"disambiguationData":[TD([[makeQuery(id+"F10.imprint","IMPRINT",EDGE,{"derivedFrom":sQuery(id+"F10.wireOp",EDGE,"E499.0")}),-1.0]])]});
            var Q22;
            Q22=makeQuery(id+"F10.imprint","IMPRINT",FACE,{"disambiguationData":[TD([[makeQuery(id+"F10.imprint","IMPRINT",EDGE,{"derivedFrom":sQuery(id+"F10.wireOp",EDGE,"E524.0")}),-1.0]])]});
            var Q23;
            Q23=makeQuery(id+"F10.imprint","IMPRINT",FACE,{"disambiguationData":[TD([[makeQuery(id+"F10.imprint","IMPRINT",EDGE,{"derivedFrom":sQuery(id+"F10.wireOp",EDGE,"E533.0")}),-1.0]])]});
            var Q24;
            Q24=makeQuery(id+"F10.imprint","IMPRINT",FACE,{"disambiguationData":[TD([[makeQuery(id+"F10.imprint","IMPRINT",EDGE,{"derivedFrom":sQuery(id+"F10.wireOp",EDGE,"E532.0")}),-1.0]])]});
            var Q25;
            Q25=makeQuery(id+"F10.imprint","IMPRINT",FACE,{"disambiguationData":[TD([[makeQuery(id+"F10.imprint","IMPRINT",EDGE,{"derivedFrom":sQuery(id+"F10.wireOp",EDGE,"E591.MirrorCS")}),1.0]])]});
            var Q26;
            Q26=makeQuery(id+"F10.imprint","IMPRINT",FACE,{"disambiguationData":[TD([[makeQuery(id+"F10.imprint","IMPRINT",EDGE,{"derivedFrom":sQuery(id+"F10.wireOp",EDGE,"E761.MirrorCS")}),1.0]])]});
            var Q27;
            Q27=makeQuery(id+"F10.imprint","IMPRINT",FACE,{"disambiguationData":[TD([[makeQuery(id+"F10.imprint","IMPRINT",EDGE,{"derivedFrom":sQuery(id+"F10.wireOp",EDGE,"E778.MirrorCS")}),1.0]])]});
            var Q28;
            Q28=makeQuery(id+"F10.imprint","IMPRINT",FACE,{"disambiguationData":[TD([[makeQuery(id+"F10.imprint","IMPRINT",EDGE,{"derivedFrom":sQuery(id+"F10.wireOp",EDGE,"E543.MirrorCS")}),1.0]])]});
            var Q29;
            Q29=makeQuery(id+"F10.imprint","IMPRINT",FACE,{"disambiguationData":[TD([[makeQuery(id+"F10.imprint","IMPRINT",EDGE,{"derivedFrom":sQuery(id+"F10.wireOp",EDGE,"E805.MirrorCS")}),1.0]])]});
            var Q30;
            Q30=makeQuery(id+"F10.imprint","IMPRINT",FACE,{"disambiguationData":[TD([[makeQuery(id+"F10.imprint","IMPRINT",EDGE,{"derivedFrom":sQuery(id+"F10.wireOp",EDGE,"E765.MirrorCS")}),1.0]])]});
            var Q31;
            Q31=makeQuery(id+"F10.imprint","IMPRINT",FACE,{"disambiguationData":[TD([[makeQuery(id+"F10.imprint","IMPRINT",EDGE,{"derivedFrom":sQuery(id+"F10.wireOp",EDGE,"E741.MirrorCS")}),1.0]])]});
            var Q32;
            Q32=makeQuery(id+"F10.imprint","IMPRINT",FACE,{"disambiguationData":[TD([[makeQuery(id+"F10.imprint","IMPRINT",EDGE,{"derivedFrom":sQuery(id+"F10.wireOp",EDGE,"E796.MirrorCS")}),1.0]])]});
            var Q33;
            Q33=makeQuery(id+"F10.imprint","IMPRINT",FACE,{"disambiguationData":[TD([[makeQuery(id+"F10.imprint","IMPRINT",EDGE,{"derivedFrom":sQuery(id+"F10.wireOp",EDGE,"E624.MirrorCS")}),1.0]])]});
            var Q34;
            Q34=makeQuery(id+"F10.imprint","IMPRINT",FACE,{"disambiguationData":[TD([[makeQuery(id+"F10.imprint","IMPRINT",EDGE,{"derivedFrom":sQuery(id+"F10.wireOp",EDGE,"E735.MirrorCS")}),1.0]])]});
            var Q35;
            Q35=makeQuery(id+"F10.imprint","IMPRINT",FACE,{"disambiguationData":[TD([[makeQuery(id+"F10.imprint","IMPRINT",EDGE,{"derivedFrom":sQuery(id+"F10.wireOp",EDGE,"E683.MirrorCS")}),1.0]])]});
            var Q36;
            Q36=makeQuery(id+"F10.imprint","IMPRINT",FACE,{"disambiguationData":[TD([[makeQuery(id+"F10.imprint","IMPRINT",EDGE,{"derivedFrom":sQuery(id+"F10.wireOp",EDGE,"E693.MirrorCS")}),1.0]])]});
            var Q37;
            Q37=makeQuery(id+"F10.imprint","IMPRINT",FACE,{"disambiguationData":[TD([[makeQuery(id+"F10.imprint","IMPRINT",EDGE,{"derivedFrom":sQuery(id+"F10.wireOp",EDGE,"E561.MirrorCS")}),1.0]])]});
            var Q38;
            Q38=makeQuery(id+"F10.imprint","IMPRINT",FACE,{"disambiguationData":[TD([[makeQuery(id+"F10.imprint","IMPRINT",EDGE,{"derivedFrom":sQuery(id+"F10.wireOp",EDGE,"E763.MirrorCS")}),1.0]])]});
            var Q39;
            Q39=makeQuery(id+"F10.imprint","IMPRINT",FACE,{"disambiguationData":[TD([[makeQuery(id+"F10.imprint","IMPRINT",EDGE,{"derivedFrom":sQuery(id+"F10.wireOp",EDGE,"E592.MirrorCS")}),1.0]])]});
            var Q40;
            Q40=makeQuery(id+"F10.imprint","IMPRINT",FACE,{"disambiguationData":[TD([[makeQuery(id+"F10.imprint","IMPRINT",EDGE,{"derivedFrom":sQuery(id+"F10.wireOp",EDGE,"E776.MirrorCS")}),1.0]])]});
            var Q41;
            Q41=makeQuery(id+"F10.imprint","IMPRINT",FACE,{"disambiguationData":[TD([[makeQuery(id+"F10.imprint","IMPRINT",EDGE,{"derivedFrom":sQuery(id+"F10.wireOp",EDGE,"E695.MirrorCS")}),1.0]])]});
            var Q42;
            Q42=makeQuery(id+"F10.imprint","IMPRINT",FACE,{"disambiguationData":[TD([[makeQuery(id+"F10.imprint","IMPRINT",EDGE,{"derivedFrom":sQuery(id+"F10.wireOp",EDGE,"E716.MirrorCS")}),1.0]])]});
            var Q43;
            Q43=makeQuery(id+"F10.imprint","IMPRINT",FACE,{"disambiguationData":[TD([[makeQuery(id+"F10.imprint","IMPRINT",EDGE,{"derivedFrom":sQuery(id+"F10.wireOp",EDGE,"E619.MirrorCS")}),1.0]])]});
            var Q44;
            Q44=makeQuery(id+"F10.imprint","IMPRINT",FACE,{"disambiguationData":[TD([[makeQuery(id+"F10.imprint","IMPRINT",EDGE,{"derivedFrom":sQuery(id+"F10.wireOp",EDGE,"E719.MirrorCS")}),1.0]])]});
            var Q45;
            Q45=makeQuery(id+"F10.imprint","IMPRINT",FACE,{"disambiguationData":[TD([[makeQuery(id+"F10.imprint","IMPRINT",EDGE,{"derivedFrom":sQuery(id+"F10.wireOp",EDGE,"E515.0")}),-1.0]])]});
            var Q46;
            Q46=makeQuery(id+"F10.imprint","IMPRINT",FACE,{"disambiguationData":[TD([[makeQuery(id+"F10.imprint","IMPRINT",EDGE,{"derivedFrom":sQuery(id+"F10.wireOp",EDGE,"E514.0")}),-1.0]])]});
            var Q47;
            Q47=makeQuery(id+"F10.imprint","IMPRINT",FACE,{"disambiguationData":[TD([[makeQuery(id+"F10.imprint","IMPRINT",EDGE,{"derivedFrom":sQuery(id+"F10.wireOp",EDGE,"E573.MirrorCS")}),1.0]])]});
            var Q48;
            Q48=makeQuery(id+"F10.imprint","IMPRINT",FACE,{"disambiguationData":[TD([[makeQuery(id+"F10.imprint","IMPRINT",EDGE,{"derivedFrom":sQuery(id+"F10.wireOp",EDGE,"E701.MirrorCS")}),1.0]])]});
            var Q49;
            Q49=makeQuery(id+"F10.imprint","IMPRINT",FACE,{"disambiguationData":[TD([[makeQuery(id+"F10.imprint","IMPRINT",EDGE,{"derivedFrom":sQuery(id+"F10.wireOp",EDGE,"E500.0")}),-1.0]])]});
            var Q50;
            Q50=makeQuery(id+"F10.imprint","IMPRINT",FACE,{"disambiguationData":[TD([[makeQuery(id+"F10.imprint","IMPRINT",EDGE,{"derivedFrom":sQuery(id+"F10.wireOp",EDGE,"E502.0")}),-1.0]])]});
            var Q51;
            Q51=makeQuery(id+"F10.imprint","IMPRINT",FACE,{"disambiguationData":[TD([[makeQuery(id+"F10.imprint","IMPRINT",EDGE,{"derivedFrom":sQuery(id+"F10.wireOp",EDGE,"E539.0")}),-1.0]])]});
            var Q52;
            Q52=makeQuery(id+"F10.imprint","IMPRINT",FACE,{"disambiguationData":[TD([[makeQuery(id+"F10.imprint","IMPRINT",EDGE,{"derivedFrom":sQuery(id+"F10.wireOp",EDGE,"E516.0")}),-1.0]])]});
            var Q53;
            Q53=makeQuery(id+"F10.imprint","IMPRINT",FACE,{"disambiguationData":[TD([[makeQuery(id+"F10.imprint","IMPRINT",EDGE,{"derivedFrom":sQuery(id+"F10.wireOp",EDGE,"E519.0")}),-1.0]])]});
            var Q54;
            Q54=makeQuery(id+"F10.imprint","IMPRINT",FACE,{"disambiguationData":[TD([[makeQuery(id+"F10.imprint","IMPRINT",EDGE,{"derivedFrom":sQuery(id+"F10.wireOp",EDGE,"E518.0")}),-1.0]])]});
            var Q55;
            Q55=makeQuery(id+"F10.imprint","IMPRINT",FACE,{"disambiguationData":[TD([[makeQuery(id+"F10.imprint","IMPRINT",EDGE,{"derivedFrom":sQuery(id+"F10.wireOp",EDGE,"E521.0")}),-1.0]])]});
            var Q56;
            {var subQ0=sQuery(id+"F10.wireOp",EDGE,"E517.2");Q56=makeQuery(id+"F10.imprint","IMPRINT",FACE,{"disambiguationData":[TD([[makeQuery(id+"F10.imprint","IMPRINT",EDGE,{"derivedFrom":subQ0}),-1.0]])]});}
            var Q57;
            Q57=makeQuery(id+"F10.imprint","IMPRINT",FACE,{"disambiguationData":[TD([[makeQuery(id+"F10.imprint","IMPRINT",EDGE,{"derivedFrom":sQuery(id+"F10.wireOp",EDGE,"E531.0")}),-1.0]])]});
            var Q58;
            Q58=makeQuery(id+"F10.imprint","IMPRINT",FACE,{"disambiguationData":[TD([[makeQuery(id+"F10.imprint","IMPRINT",EDGE,{"derivedFrom":sQuery(id+"F10.wireOp",EDGE,"E520.0")}),-1.0]])]});
            var Q59;
            Q59=makeQuery(id+"F10.imprint","IMPRINT",FACE,{"disambiguationData":[TD([[makeQuery(id+"F10.imprint","IMPRINT",EDGE,{"derivedFrom":sQuery(id+"F10.wireOp",EDGE,"E522.0")}),-1.0]])]});
            var Q60;
            Q60=makeQuery(id+"F10.imprint","IMPRINT",FACE,{"disambiguationData":[TD([[makeQuery(id+"F10.imprint","IMPRINT",EDGE,{"derivedFrom":sQuery(id+"F10.wireOp",EDGE,"E490.0")}),-1.0]])]});
            var Q61;
            Q61=makeQuery(id+"F10.imprint","IMPRINT",FACE,{"disambiguationData":[TD([[makeQuery(id+"F10.imprint","IMPRINT",EDGE,{"derivedFrom":sQuery(id+"F10.wireOp",EDGE,"E489.0")}),-1.0]])]});
            var Q62;
            Q62=makeQuery(id+"F10.imprint","IMPRINT",FACE,{"disambiguationData":[TD([[makeQuery(id+"F10.imprint","IMPRINT",EDGE,{"derivedFrom":sQuery(id+"F10.wireOp",EDGE,"E506.0")}),-1.0]])]});
            var Q63;
            Q63=makeQuery(id+"F10.imprint","IMPRINT",FACE,{"disambiguationData":[TD([[makeQuery(id+"F10.imprint","IMPRINT",EDGE,{"derivedFrom":sQuery(id+"F10.wireOp",EDGE,"E491.0")}),-1.0]])]});
            var Q64;
            Q64=makeQuery(id+"F10.imprint","IMPRINT",FACE,{"disambiguationData":[TD([[makeQuery(id+"F10.imprint","IMPRINT",EDGE,{"derivedFrom":sQuery(id+"F10.wireOp",EDGE,"E486.0")}),-1.0]])]});
            var Q65;
            Q65=makeQuery(id+"F10.imprint","IMPRINT",FACE,{"disambiguationData":[TD([[makeQuery(id+"F10.imprint","IMPRINT",EDGE,{"derivedFrom":sQuery(id+"F10.wireOp",EDGE,"E484.0")}),-1.0]])]});
            var Q66;
            Q66=makeQuery(id+"F10.imprint","IMPRINT",FACE,{"disambiguationData":[TD([[makeQuery(id+"F10.imprint","IMPRINT",EDGE,{"derivedFrom":sQuery(id+"F10.wireOp",EDGE,"E482.0")}),-1.0]])]});
            var Q67;
            Q67=makeQuery(id+"F10.imprint","IMPRINT",FACE,{"disambiguationData":[TD([[makeQuery(id+"F10.imprint","IMPRINT",EDGE,{"derivedFrom":sQuery(id+"F10.wireOp",EDGE,"E487.0")}),-1.0]])]});
            var Q68;
            Q68=makeQuery(id+"F10.imprint","IMPRINT",FACE,{"disambiguationData":[TD([[makeQuery(id+"F10.imprint","IMPRINT",EDGE,{"derivedFrom":sQuery(id+"F10.wireOp",EDGE,"E488.0")}),-1.0]])]});
            var Q69;
            Q69=makeQuery(id+"F10.imprint","IMPRINT",FACE,{"disambiguationData":[TD([[makeQuery(id+"F10.imprint","IMPRINT",EDGE,{"derivedFrom":sQuery(id+"F10.wireOp",EDGE,"E535.0")}),-1.0]])]});
            var Q70;
            Q70=makeQuery(id+"F10.imprint","IMPRINT",FACE,{"disambiguationData":[TD([[makeQuery(id+"F10.imprint","IMPRINT",EDGE,{"derivedFrom":sQuery(id+"F10.wireOp",EDGE,"E534.0")}),-1.0]])]});
            var Q71;
            Q71=makeQuery(id+"F10.imprint","IMPRINT",FACE,{"disambiguationData":[TD([[makeQuery(id+"F10.imprint","IMPRINT",EDGE,{"derivedFrom":sQuery(id+"F10.wireOp",EDGE,"E477.0")}),-1.0]])]});
            var Q72;
            Q72=makeQuery(id+"F10.imprint","IMPRINT",FACE,{"disambiguationData":[TD([[makeQuery(id+"F10.imprint","IMPRINT",EDGE,{"derivedFrom":sQuery(id+"F10.wireOp",EDGE,"E536.0")}),-1.0]])]});
            var Q73;
            Q73=makeQuery(id+"F10.imprint","IMPRINT",FACE,{"disambiguationData":[TD([[makeQuery(id+"F10.imprint","IMPRINT",EDGE,{"derivedFrom":sQuery(id+"F10.wireOp",EDGE,"E478.0")}),-1.0]])]});
            var Q74;
            Q74=makeQuery(id+"F10.imprint","IMPRINT",FACE,{"disambiguationData":[TD([[makeQuery(id+"F10.imprint","IMPRINT",EDGE,{"derivedFrom":sQuery(id+"F10.wireOp",EDGE,"E476.0")}),-1.0]])]});
            var Q75;
            Q75=makeQuery(id+"F10.imprint","IMPRINT",FACE,{"disambiguationData":[TD([[makeQuery(id+"F10.imprint","IMPRINT",EDGE,{"derivedFrom":sQuery(id+"F10.wireOp",EDGE,"E537.0")}),-1.0]])]});
            var Q76;
            Q76=makeQuery(id+"F10.imprint","IMPRINT",FACE,{"disambiguationData":[TD([[makeQuery(id+"F10.imprint","IMPRINT",EDGE,{"derivedFrom":sQuery(id+"F10.wireOp",EDGE,"E475.0")}),-1.0]])]});
            var Q77;
            Q77=makeQuery(id+"F10.imprint","IMPRINT",FACE,{"disambiguationData":[TD([[makeQuery(id+"F10.imprint","IMPRINT",EDGE,{"derivedFrom":sQuery(id+"F10.wireOp",EDGE,"E504.0")}),-1.0]])]});
            var Q78;
            Q78=makeQuery(id+"F10.imprint","IMPRINT",FACE,{"disambiguationData":[TD([[makeQuery(id+"F10.imprint","IMPRINT",EDGE,{"derivedFrom":sQuery(id+"F10.wireOp",EDGE,"E479.0")}),-1.0]])]});
            var Q79;
            Q79=makeQuery(id+"F10.imprint","IMPRINT",FACE,{"disambiguationData":[TD([[makeQuery(id+"F10.imprint","IMPRINT",EDGE,{"derivedFrom":sQuery(id+"F10.wireOp",EDGE,"E476.0")}),-1.0]])]});
            var Q80;
            Q80=makeQuery(id+"F10.imprint","IMPRINT",FACE,{"disambiguationData":[TD([[makeQuery(id+"F10.imprint","IMPRINT",EDGE,{"derivedFrom":sQuery(id+"F10.wireOp",EDGE,"E474.0")}),-1.0]])]});
            var Q81;
            Q81=makeQuery(id+"F10.imprint","IMPRINT",FACE,{"disambiguationData":[TD([[makeQuery(id+"F10.imprint","IMPRINT",EDGE,{"derivedFrom":sQuery(id+"F10.wireOp",EDGE,"E481.0")}),-1.0]])]});
            var Q82;
            Q82=makeQuery(id+"F10.imprint","IMPRINT",FACE,{"disambiguationData":[TD([[makeQuery(id+"F10.imprint","IMPRINT",EDGE,{"derivedFrom":sQuery(id+"F10.wireOp",EDGE,"E505.0")}),-1.0]])]});
            var Q83;
            Q83=makeQuery(id+"F10.imprint","IMPRINT",FACE,{"disambiguationData":[TD([[makeQuery(id+"F10.imprint","IMPRINT",EDGE,{"derivedFrom":sQuery(id+"F10.wireOp",EDGE,"E483.0")}),-1.0]])]});
            var Q84;
            Q84=makeQuery(id+"F10.imprint","IMPRINT",FACE,{"disambiguationData":[TD([[makeQuery(id+"F10.imprint","IMPRINT",EDGE,{"derivedFrom":sQuery(id+"F10.wireOp",EDGE,"E538.0")}),-1.0]])]});
            var Q85;
            Q85=makeQuery(id+"F10.imprint","IMPRINT",FACE,{"disambiguationData":[TD([[makeQuery(id+"F10.imprint","IMPRINT",EDGE,{"derivedFrom":sQuery(id+"F10.wireOp",EDGE,"E480.0")}),-1.0]])]});
            var Q86;
            Q86=makeQuery(id+"F10.imprint","IMPRINT",FACE,{"disambiguationData":[TD([[makeQuery(id+"F10.imprint","IMPRINT",EDGE,{"derivedFrom":sQuery(id+"F10.wireOp",EDGE,"E485.0")}),-1.0]])]});
            var Q87;
            Q87=makeQuery(id+"F10.imprint","IMPRINT",FACE,{"disambiguationData":[TD([[makeQuery(id+"F10.imprint","IMPRINT",EDGE,{"derivedFrom":sQuery(id+"F10.wireOp",EDGE,"E530.0")}),-1.0]])]});
            var Q88;
            Q88=makeQuery(id+"F10.imprint","IMPRINT",FACE,{"disambiguationData":[TD([[makeQuery(id+"F10.imprint","IMPRINT",EDGE,{"derivedFrom":sQuery(id+"F10.wireOp",EDGE,"E529.0")}),-1.0]])]});
            var Q89;
            Q89=makeQuery(id+"F10.imprint","IMPRINT",FACE,{"disambiguationData":[TD([[makeQuery(id+"F10.imprint","IMPRINT",EDGE,{"derivedFrom":sQuery(id+"F10.wireOp",EDGE,"E923.0")}),-1.0]])]});
            var Q90;
            Q90=makeQuery(id+"F10.imprint","IMPRINT",FACE,{"disambiguationData":[TD([[makeQuery(id+"F10.imprint","IMPRINT",EDGE,{"derivedFrom":sQuery(id+"F10.wireOp",EDGE,"E527.0")}),-1.0]])]});
            var Q91;
            Q91=makeQuery(id+"F10.imprint","IMPRINT",FACE,{"disambiguationData":[TD([[makeQuery(id+"F10.imprint","IMPRINT",EDGE,{"derivedFrom":sQuery(id+"F10.wireOp",EDGE,"E526.0")}),-1.0]])]});
            var Q92;
            Q92=makeQuery(id+"F10.imprint","IMPRINT",FACE,{"disambiguationData":[TD([[makeQuery(id+"F10.imprint","IMPRINT",EDGE,{"derivedFrom":sQuery(id+"F10.wireOp",EDGE,"E528.0")}),-1.0]])]});
            var Q93;
            Q93=makeQuery(id+"F10.imprint","IMPRINT",FACE,{"disambiguationData":[TD([[makeQuery(id+"F10.imprint","IMPRINT",EDGE,{"derivedFrom":sQuery(id+"F10.wireOp",EDGE,"E538.0")}),-1.0]])]});
            var Q94;
            Q94=makeQuery(id+"F10.imprint","IMPRINT",FACE,{"disambiguationData":[TD([[makeQuery(id+"F10.imprint","IMPRINT",EDGE,{"derivedFrom":sQuery(id+"F10.wireOp",EDGE,"E926.0")}),-1.0]])]});
            var Q95;
            Q95=makeQuery(id+"F10.imprint","IMPRINT",FACE,{"disambiguationData":[TD([[makeQuery(id+"F10.imprint","IMPRINT",EDGE,{"derivedFrom":sQuery(id+"F10.wireOp",EDGE,"E925.0")}),-1.0]])]});
            var Q96;
            Q96=makeQuery(id+"F10.imprint","IMPRINT",FACE,{"disambiguationData":[TD([[makeQuery(id+"F10.imprint","IMPRINT",EDGE,{"derivedFrom":sQuery(id+"F10.wireOp",EDGE,"E922.0")}),-1.0]])]});
            var Q97;
            Q97=makeQuery(id+"F10.imprint","IMPRINT",FACE,{"disambiguationData":[TD([[makeQuery(id+"F10.imprint","IMPRINT",EDGE,{"derivedFrom":sQuery(id+"F10.wireOp",EDGE,"E584.MirrorCS")}),1.0]])]});
            var Q98;
            Q98=makeQuery(id+"F10.imprint","IMPRINT",FACE,{"disambiguationData":[TD([[makeQuery(id+"F10.imprint","IMPRINT",EDGE,{"derivedFrom":sQuery(id+"F10.wireOp",EDGE,"E795.MirrorCS")}),1.0]])]});
            var Q99;
            Q99=makeQuery(id+"F10.imprint","IMPRINT",FACE,{"disambiguationData":[TD([[makeQuery(id+"F10.imprint","IMPRINT",EDGE,{"derivedFrom":sQuery(id+"F10.wireOp",EDGE,"E814.MirrorCS")}),1.0]])]});
            var Q100;
            Q100=makeQuery(id+"F10.imprint","IMPRINT",FACE,{"disambiguationData":[TD([[makeQuery(id+"F10.imprint","IMPRINT",EDGE,{"derivedFrom":sQuery(id+"F10.wireOp",EDGE,"E715.MirrorCS")}),1.0]])]});
            var Q101;
            Q101=makeQuery(id+"F10.imprint","IMPRINT",FACE,{"disambiguationData":[TD([[makeQuery(id+"F10.imprint","IMPRINT",EDGE,{"derivedFrom":sQuery(id+"F10.wireOp",EDGE,"E924.0")}),-1.0]])]});
            var Q102;
            Q102=makeQuery(id+"F10.imprint","IMPRINT",FACE,{"disambiguationData":[TD([[makeQuery(id+"F10.imprint","IMPRINT",EDGE,{"derivedFrom":sQuery(id+"F10.wireOp",EDGE,"E702.MirrorCS")}),1.0]])]});
            var Q103;
            Q103=makeQuery(id+"F10.imprint","IMPRINT",FACE,{"disambiguationData":[TD([[makeQuery(id+"F10.imprint","IMPRINT",EDGE,{"derivedFrom":sQuery(id+"F10.wireOp",EDGE,"E783.MirrorCS")}),1.0]])]});
            var Q104;
            Q104=makeQuery(id+"F10.imprint","IMPRINT",FACE,{"disambiguationData":[TD([[makeQuery(id+"F10.imprint","IMPRINT",EDGE,{"derivedFrom":sQuery(id+"F10.wireOp",EDGE,"E630.MirrorCS")}),1.0]])]});
            var Q105;
            Q105=makeQuery(id+"F10.imprint","IMPRINT",FACE,{"disambiguationData":[TD([[makeQuery(id+"F10.imprint","IMPRINT",EDGE,{"derivedFrom":sQuery(id+"F10.wireOp",EDGE,"E647.MirrorCS")}),1.0]])]});
            var Q106;
            Q106=makeQuery(id+"F10.imprint","IMPRINT",FACE,{"disambiguationData":[TD([[makeQuery(id+"F10.imprint","IMPRINT",EDGE,{"derivedFrom":sQuery(id+"F10.wireOp",EDGE,"E684.MirrorCS")}),1.0]])]});
            var Q107;
            Q107=makeQuery(id+"F10.imprint","IMPRINT",FACE,{"disambiguationData":[TD([[makeQuery(id+"F10.imprint","IMPRINT",EDGE,{"derivedFrom":sQuery(id+"F10.wireOp",EDGE,"E734.MirrorCS")}),1.0]])]});
            var Q108;
            Q108=makeQuery(id+"F10.imprint","IMPRINT",FACE,{"disambiguationData":[TD([[makeQuery(id+"F10.imprint","IMPRINT",EDGE,{"derivedFrom":sQuery(id+"F10.wireOp",EDGE,"E618.MirrorCS")}),1.0]])]});
            var Q109;
            Q109=makeQuery(id+"F10.imprint","IMPRINT",FACE,{"disambiguationData":[TD([[makeQuery(id+"F10.imprint","IMPRINT",EDGE,{"derivedFrom":sQuery(id+"F10.wireOp",EDGE,"E717.MirrorCS")}),1.0]])]});
            var Q110;
            Q110=makeQuery(id+"F10.imprint","IMPRINT",FACE,{"disambiguationData":[TD([[makeQuery(id+"F10.imprint","IMPRINT",EDGE,{"derivedFrom":sQuery(id+"F10.wireOp",EDGE,"E590.MirrorCS")}),1.0]])]});
            var Q111;
            Q111=makeQuery(id+"F10.imprint","IMPRINT",FACE,{"disambiguationData":[TD([[makeQuery(id+"F10.imprint","IMPRINT",EDGE,{"derivedFrom":sQuery(id+"F10.wireOp",EDGE,"E562.MirrorCS")}),1.0]])]});
            var Q112;
            Q112=makeQuery(id+"F10.imprint","IMPRINT",FACE,{"disambiguationData":[TD([[makeQuery(id+"F10.imprint","IMPRINT",EDGE,{"derivedFrom":sQuery(id+"F10.wireOp",EDGE,"E718.MirrorCS")}),1.0]])]});
            var Q113;
            Q113=makeQuery(id+"F10.imprint","IMPRINT",FACE,{"disambiguationData":[TD([[makeQuery(id+"F10.imprint","IMPRINT",EDGE,{"derivedFrom":sQuery(id+"F10.wireOp",EDGE,"E631.MirrorCS")}),1.0]])]});
            var Q114;
            Q114=makeQuery(id+"F10.imprint","IMPRINT",FACE,{"disambiguationData":[TD([[makeQuery(id+"F10.imprint","IMPRINT",EDGE,{"derivedFrom":sQuery(id+"F10.wireOp",EDGE,"E548.MirrorCS")}),1.0]])]});
            var Q115;
            Q115=makeQuery(id+"F10.imprint","IMPRINT",FACE,{"disambiguationData":[TD([[makeQuery(id+"F10.imprint","IMPRINT",EDGE,{"derivedFrom":sQuery(id+"F10.wireOp",EDGE,"E575.MirrorCS")}),1.0]])]});
            var Q116;
            Q116=makeQuery(id+"F10.imprint","IMPRINT",FACE,{"disambiguationData":[TD([[makeQuery(id+"F10.imprint","IMPRINT",EDGE,{"derivedFrom":sQuery(id+"F10.wireOp",EDGE,"E743.MirrorCS")}),1.0]])]});
            var Q117;
            Q117=makeQuery(id+"F10.imprint","IMPRINT",FACE,{"disambiguationData":[TD([[makeQuery(id+"F10.imprint","IMPRINT",EDGE,{"derivedFrom":sQuery(id+"F10.wireOp",EDGE,"E800.MirrorCS")}),1.0]])]});
            var Q118;
            Q118=makeQuery(id+"F10.imprint","IMPRINT",FACE,{"disambiguationData":[TD([[makeQuery(id+"F10.imprint","IMPRINT",EDGE,{"derivedFrom":sQuery(id+"F10.wireOp",EDGE,"E792.MirrorCS")}),1.0]])]});
            var Q119;
            Q119=makeQuery(id+"F10.imprint","IMPRINT",FACE,{"disambiguationData":[TD([[makeQuery(id+"F10.imprint","IMPRINT",EDGE,{"derivedFrom":sQuery(id+"F10.wireOp",EDGE,"E580.MirrorCS")}),1.0]])]});
            var Q120;
            Q120=makeQuery(id+"F10.imprint","IMPRINT",FACE,{"disambiguationData":[TD([[makeQuery(id+"F10.imprint","IMPRINT",EDGE,{"derivedFrom":sQuery(id+"F10.wireOp",EDGE,"E802.MirrorCS")}),1.0]])]});
            var Q121;
            Q121=makeQuery(id+"F10.imprint","IMPRINT",FACE,{"disambiguationData":[TD([[makeQuery(id+"F10.imprint","IMPRINT",EDGE,{"derivedFrom":sQuery(id+"F10.wireOp",EDGE,"E682.MirrorCS")}),1.0]])]});
            var Q122;
            Q122=makeQuery(id+"F10.imprint","IMPRINT",FACE,{"disambiguationData":[TD([[makeQuery(id+"F10.imprint","IMPRINT",EDGE,{"derivedFrom":sQuery(id+"F10.wireOp",EDGE,"E582.MirrorCS")}),1.0]])]});
            var Q123;
            Q123=makeQuery(id+"F10.imprint","IMPRINT",FACE,{"disambiguationData":[TD([[makeQuery(id+"F10.imprint","IMPRINT",EDGE,{"derivedFrom":sQuery(id+"F10.wireOp",EDGE,"E780.MirrorCS")}),1.0]])]});
            var Q124;
            Q124=makeQuery(id+"F10.imprint","IMPRINT",FACE,{"disambiguationData":[TD([[makeQuery(id+"F10.imprint","IMPRINT",EDGE,{"derivedFrom":sQuery(id+"F10.wireOp",EDGE,"E818.MirrorCS")}),1.0]])]});
            var Q125;
            Q125=makeQuery(id+"F10.imprint","IMPRINT",FACE,{"disambiguationData":[TD([[makeQuery(id+"F10.imprint","IMPRINT",EDGE,{"derivedFrom":sQuery(id+"F10.wireOp",EDGE,"E780.MirrorCS")}),1.0]])]});
            var Q126;
            Q126=makeQuery(id+"F10.imprint","IMPRINT",FACE,{"disambiguationData":[TD([[makeQuery(id+"F10.imprint","IMPRINT",EDGE,{"derivedFrom":sQuery(id+"F10.wireOp",EDGE,"E691.MirrorCS")}),1.0]])]});
            var Q127;
            Q127=makeQuery(id+"F10.imprint","IMPRINT",FACE,{"disambiguationData":[TD([[makeQuery(id+"F10.imprint","IMPRINT",EDGE,{"derivedFrom":sQuery(id+"F10.wireOp",EDGE,"E784.MirrorCS")}),1.0]])]});
            var Q128;
            Q128=makeQuery(id+"F10.imprint","IMPRINT",FACE,{"disambiguationData":[TD([[makeQuery(id+"F10.imprint","IMPRINT",EDGE,{"derivedFrom":sQuery(id+"F10.wireOp",EDGE,"E560.MirrorCS")}),1.0]])]});
            var Q129;
            Q129=makeQuery(id+"F10.imprint","IMPRINT",FACE,{"disambiguationData":[TD([[makeQuery(id+"F10.imprint","IMPRINT",EDGE,{"derivedFrom":sQuery(id+"F10.wireOp",EDGE,"E690.MirrorCS")}),1.0]])]});
            var Q130;
            Q130=makeQuery(id+"F10.imprint","IMPRINT",FACE,{"disambiguationData":[TD([[makeQuery(id+"F10.imprint","IMPRINT",EDGE,{"derivedFrom":sQuery(id+"F10.wireOp",EDGE,"E733.MirrorCS")}),1.0]])]});
            var Q131;
            Q131=makeQuery(id+"F10.imprint","IMPRINT",FACE,{"disambiguationData":[TD([[makeQuery(id+"F10.imprint","IMPRINT",EDGE,{"derivedFrom":sQuery(id+"F10.wireOp",EDGE,"E653.MirrorCS")}),1.0]])]});
            var Q132;
            Q132=makeQuery(id+"F10.imprint","IMPRINT",FACE,{"disambiguationData":[TD([[makeQuery(id+"F10.imprint","IMPRINT",EDGE,{"derivedFrom":sQuery(id+"F10.wireOp",EDGE,"E655.MirrorCS")}),1.0]])]});
            var Q133;
            Q133=makeQuery(id+"F10.imprint","IMPRINT",FACE,{"disambiguationData":[TD([[makeQuery(id+"F10.imprint","IMPRINT",EDGE,{"derivedFrom":sQuery(id+"F10.wireOp",EDGE,"E733.MirrorCS")}),1.0]])]});
            var Q134;
            Q134=makeQuery(id+"F10.imprint","IMPRINT",FACE,{"disambiguationData":[TD([[makeQuery(id+"F10.imprint","IMPRINT",EDGE,{"derivedFrom":sQuery(id+"F10.wireOp",EDGE,"E569.MirrorCS")}),1.0]])]});
            var Q135;
            Q135=makeQuery(id+"F10.imprint","IMPRINT",FACE,{"disambiguationData":[TD([[makeQuery(id+"F10.imprint","IMPRINT",EDGE,{"derivedFrom":sQuery(id+"F10.wireOp",EDGE,"E620.MirrorCS")}),1.0]])]});
            var Q136;
            Q136=makeQuery(id+"F10.imprint","IMPRINT",FACE,{"disambiguationData":[TD([[makeQuery(id+"F10.imprint","IMPRINT",EDGE,{"derivedFrom":sQuery(id+"F10.wireOp",EDGE,"E706.MirrorCS")}),1.0]])]});
            var Q137;
            Q137=makeQuery(id+"F10.imprint","IMPRINT",FACE,{"disambiguationData":[TD([[makeQuery(id+"F10.imprint","IMPRINT",EDGE,{"derivedFrom":sQuery(id+"F10.wireOp",EDGE,"E644.MirrorCS")}),1.0]])]});
            var Q138;
            Q138=makeQuery(id+"F10.imprint","IMPRINT",FACE,{"disambiguationData":[TD([[makeQuery(id+"F10.imprint","IMPRINT",EDGE,{"derivedFrom":sQuery(id+"F10.wireOp",EDGE,"E671.MirrorCS")}),1.0]])]});
            var Q139;
            Q139=makeQuery(id+"F10.imprint","IMPRINT",FACE,{"disambiguationData":[TD([[makeQuery(id+"F10.imprint","IMPRINT",EDGE,{"derivedFrom":sQuery(id+"F10.wireOp",EDGE,"E547.MirrorCS")}),1.0]])]});
            var Q140;
            Q140=makeQuery(id+"F10.imprint","IMPRINT",FACE,{"disambiguationData":[TD([[makeQuery(id+"F10.imprint","IMPRINT",EDGE,{"derivedFrom":sQuery(id+"F10.wireOp",EDGE,"E570.MirrorCS")}),1.0]])]});
            var Q141;
            Q141=makeQuery(id+"F10.imprint","IMPRINT",FACE,{"disambiguationData":[TD([[makeQuery(id+"F10.imprint","IMPRINT",EDGE,{"derivedFrom":sQuery(id+"F10.wireOp",EDGE,"E628.MirrorCS")}),1.0]])]});
            var Q142;
            Q142=makeQuery(id+"F10.imprint","IMPRINT",FACE,{"disambiguationData":[TD([[makeQuery(id+"F10.imprint","IMPRINT",EDGE,{"derivedFrom":sQuery(id+"F10.wireOp",EDGE,"E597.MirrorCS")}),1.0]])]});
            var Q143;
            Q143=makeQuery(id+"F10.imprint","IMPRINT",FACE,{"disambiguationData":[TD([[makeQuery(id+"F10.imprint","IMPRINT",EDGE,{"derivedFrom":sQuery(id+"F10.wireOp",EDGE,"E659.MirrorCS")}),1.0]])]});
            var Q144;
            Q144=makeQuery(id+"F10.imprint","IMPRINT",FACE,{"disambiguationData":[TD([[makeQuery(id+"F10.imprint","IMPRINT",EDGE,{"derivedFrom":sQuery(id+"F10.wireOp",EDGE,"E723.MirrorCS")}),1.0]])]});
            var Q145;
            Q145=makeQuery(id+"F10.imprint","IMPRINT",FACE,{"disambiguationData":[TD([[makeQuery(id+"F10.imprint","IMPRINT",EDGE,{"derivedFrom":sQuery(id+"F10.wireOp",EDGE,"E583.MirrorCS")}),1.0]])]});
            extrude(context, id + "F11", {"entities" : qUnion([Q0, Q1, Q2, Q3, Q4, Q5, Q6, Q7, Q8, Q9, Q10, Q11, Q12, Q13, Q14, Q15, Q16, Q17, Q18, Q19, Q20, Q21, Q22, Q23, Q24, Q25, Q26, Q27, Q28, Q29, Q30, Q31, Q32, Q33, Q34, Q35, Q36, Q37, Q38, Q39, Q40, Q41, Q42, Q43, Q44, Q45, Q46, Q47, Q48, Q49, Q50, Q51, Q52, Q53, Q54, Q55, Q56, Q57, Q58, Q59, Q60, Q61, Q62, Q63, Q64, Q65, Q66, Q67, Q68, Q69, Q70, Q71, Q72, Q73, Q74, Q75, Q76, Q77, Q78, Q79, Q80, Q81, Q82, Q83, Q84, Q85, Q86, Q87, Q88, Q89, Q90, Q91, Q92, Q93, Q94, Q95, Q96, Q97, Q98, Q99, Q100, Q101, Q102, Q103, Q104, Q105, Q106, Q107, Q108, Q109, Q110, Q111, Q112, Q113, Q114, Q115, Q116, Q117, Q118, Q119, Q120, Q121, Q122, Q123, Q124, Q125, Q126, Q127, Q128, Q129, Q130, Q131, Q132, Q133, Q134, Q135, Q136, Q137, Q138, Q139, Q140, Q141, Q142, Q143, Q144, Q145]), "operationType" : NewBodyOperationType.REMOVE, "oppositeDirection" : true, "depth" : 111.76 * mm});
        }
    });
